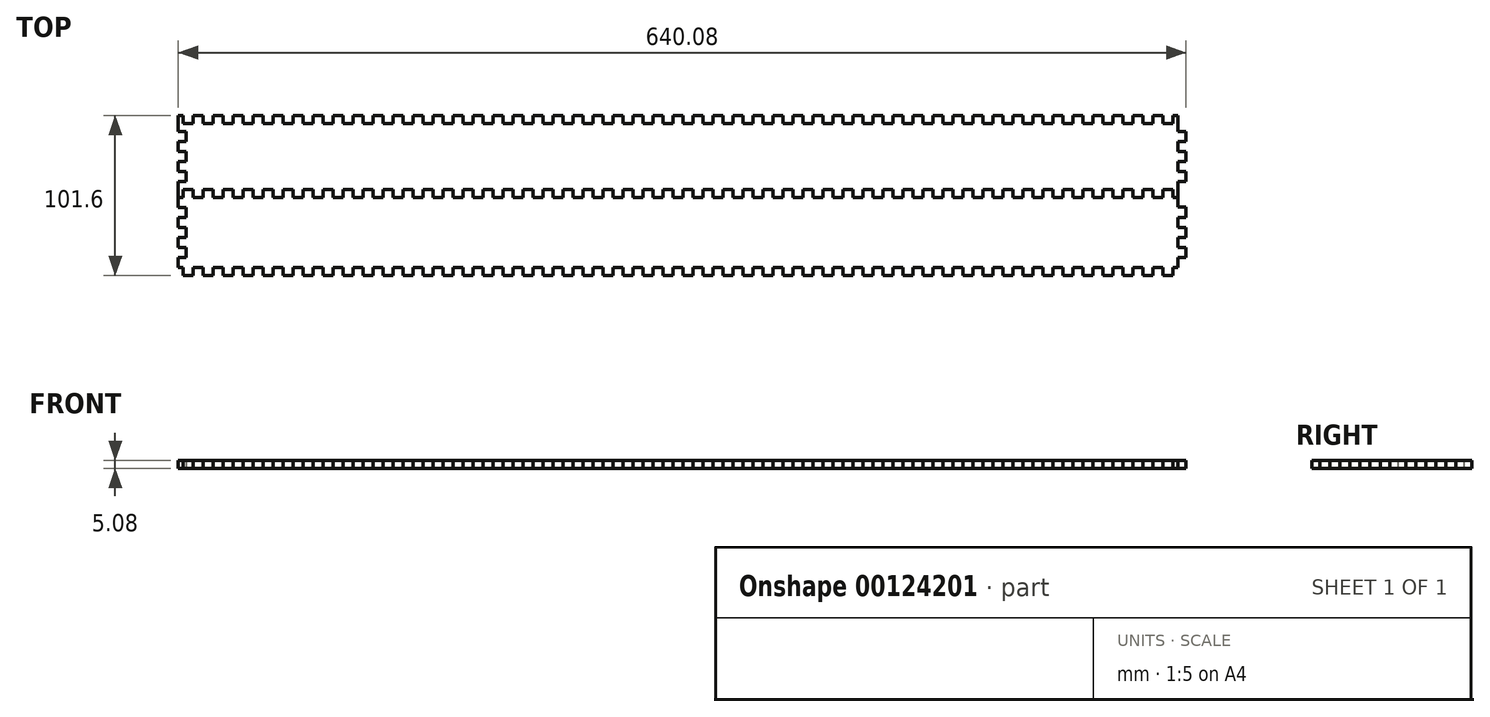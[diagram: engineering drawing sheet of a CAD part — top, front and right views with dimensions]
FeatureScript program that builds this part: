
annotation { "Feature Type Name" : "Feature", "Feature Type Description" : "" }
export const myFeature = defineFeature(function(context is Context, id is Id, definition is map)
    precondition{}
    {
        {
            var Q0;
            Q0=qCreatedBy(makeId("Top.planeOp"),FACE);
            var sketch = newSketch(context, id + "F0", { "sketchPlane" : qUnion([Q0])});
            skLineSegment(sketch, "E0.bottom", {"start": v(-432.26, 259.44) * mm, "end": v(380.54, 259.44) * mm});
            skLineSegment(sketch, "E0.top", {"start": v(-432.26, -197.76) * mm, "end": v(380.54, -197.76) * mm});
            skLineSegment(sketch, "E0.right", {"start": v(380.54, 259.44) * mm, "end": v(380.54, -197.76) * mm});
            skLineSegment(sketch, "E1.bottom", {"start": v(-418.93, 255.63) * mm, "end": v(-412.58, 255.63) * mm});
            skLineSegment(sketch, "E1.left", {"start": v(-418.93, 255.63) * mm, "end": v(-418.93, 250.55) * mm});
            skLineSegment(sketch, "E1.right", {"start": v(-412.58, 255.63) * mm, "end": v(-412.58, 250.55) * mm});
            skLineSegment(sketch, "E2", {"start": v(-412.58, 250.55) * mm, "end": v(-406.23, 250.55) * mm});
            skLineSegment(sketch, "E3.1.0.0", {"start": v(-406.23, 255.63) * mm, "end": v(-406.23, 250.55) * mm});
            skLineSegment(sketch, "E3.1.0.1", {"start": v(-406.23, 255.63) * mm, "end": v(-399.88, 255.63) * mm});
            skLineSegment(sketch, "E3.1.0.2", {"start": v(-399.88, 255.63) * mm, "end": v(-399.88, 250.55) * mm});
            skLineSegment(sketch, "E3.1.0.3", {"start": v(-399.88, 250.55) * mm, "end": v(-393.53, 250.55) * mm});
            skLineSegment(sketch, "E3.2.0.0", {"start": v(-393.53, 255.63) * mm, "end": v(-393.53, 250.55) * mm});
            skLineSegment(sketch, "E3.2.0.1", {"start": v(-393.53, 255.63) * mm, "end": v(-387.18, 255.63) * mm});
            skLineSegment(sketch, "E3.2.0.2", {"start": v(-387.18, 255.63) * mm, "end": v(-387.18, 250.55) * mm});
            skLineSegment(sketch, "E3.2.0.3", {"start": v(-387.18, 250.55) * mm, "end": v(-380.83, 250.55) * mm});
            skLineSegment(sketch, "E3.3.0.0", {"start": v(-380.83, 255.63) * mm, "end": v(-380.83, 250.55) * mm});
            skLineSegment(sketch, "E3.3.0.1", {"start": v(-380.83, 255.63) * mm, "end": v(-374.48, 255.63) * mm});
            skLineSegment(sketch, "E3.3.0.2", {"start": v(-374.48, 255.63) * mm, "end": v(-374.48, 250.55) * mm});
            skLineSegment(sketch, "E3.3.0.3", {"start": v(-374.48, 250.55) * mm, "end": v(-368.13, 250.55) * mm});
            skLineSegment(sketch, "E3.4.0.0", {"start": v(-368.13, 255.63) * mm, "end": v(-368.13, 250.55) * mm});
            skLineSegment(sketch, "E3.4.0.1", {"start": v(-368.13, 255.63) * mm, "end": v(-361.78, 255.63) * mm});
            skLineSegment(sketch, "E3.4.0.2", {"start": v(-361.78, 255.63) * mm, "end": v(-361.78, 250.55) * mm});
            skLineSegment(sketch, "E3.4.0.3", {"start": v(-361.78, 250.55) * mm, "end": v(-355.43, 250.55) * mm});
            skLineSegment(sketch, "E3.5.0.0", {"start": v(-355.43, 255.63) * mm, "end": v(-355.43, 250.55) * mm});
            skLineSegment(sketch, "E3.5.0.1", {"start": v(-355.43, 255.63) * mm, "end": v(-349.08, 255.63) * mm});
            skLineSegment(sketch, "E3.5.0.2", {"start": v(-349.08, 255.63) * mm, "end": v(-349.08, 250.55) * mm});
            skLineSegment(sketch, "E3.5.0.3", {"start": v(-349.08, 250.55) * mm, "end": v(-342.73, 250.55) * mm});
            skLineSegment(sketch, "E3.6.0.0", {"start": v(-342.73, 255.63) * mm, "end": v(-342.73, 250.55) * mm});
            skLineSegment(sketch, "E3.6.0.1", {"start": v(-342.73, 255.63) * mm, "end": v(-336.38, 255.63) * mm});
            skLineSegment(sketch, "E3.6.0.2", {"start": v(-336.38, 255.63) * mm, "end": v(-336.38, 250.55) * mm});
            skLineSegment(sketch, "E3.6.0.3", {"start": v(-336.38, 250.55) * mm, "end": v(-330.03, 250.55) * mm});
            skLineSegment(sketch, "E3.7.0.0", {"start": v(-330.03, 255.63) * mm, "end": v(-330.03, 250.55) * mm});
            skLineSegment(sketch, "E3.7.0.1", {"start": v(-330.03, 255.63) * mm, "end": v(-323.68, 255.63) * mm});
            skLineSegment(sketch, "E3.7.0.2", {"start": v(-323.68, 255.63) * mm, "end": v(-323.68, 250.55) * mm});
            skLineSegment(sketch, "E3.7.0.3", {"start": v(-323.68, 250.55) * mm, "end": v(-317.33, 250.55) * mm});
            skLineSegment(sketch, "E3.8.0.0", {"start": v(-317.33, 255.63) * mm, "end": v(-317.33, 250.55) * mm});
            skLineSegment(sketch, "E3.8.0.1", {"start": v(-317.33, 255.63) * mm, "end": v(-310.98, 255.63) * mm});
            skLineSegment(sketch, "E3.8.0.2", {"start": v(-310.98, 255.63) * mm, "end": v(-310.98, 250.55) * mm});
            skLineSegment(sketch, "E3.8.0.3", {"start": v(-310.98, 250.55) * mm, "end": v(-304.63, 250.55) * mm});
            skLineSegment(sketch, "E3.9.0.0", {"start": v(-304.63, 255.63) * mm, "end": v(-304.63, 250.55) * mm});
            skLineSegment(sketch, "E3.9.0.1", {"start": v(-304.63, 255.63) * mm, "end": v(-298.28, 255.63) * mm});
            skLineSegment(sketch, "E3.9.0.2", {"start": v(-298.28, 255.63) * mm, "end": v(-298.28, 250.55) * mm});
            skLineSegment(sketch, "E3.9.0.3", {"start": v(-298.28, 250.55) * mm, "end": v(-291.93, 250.55) * mm});
            skLineSegment(sketch, "E3.10.0.0", {"start": v(-291.93, 255.63) * mm, "end": v(-291.93, 250.55) * mm});
            skLineSegment(sketch, "E3.10.0.1", {"start": v(-291.93, 255.63) * mm, "end": v(-285.58, 255.63) * mm});
            skLineSegment(sketch, "E3.10.0.2", {"start": v(-285.58, 255.63) * mm, "end": v(-285.58, 250.55) * mm});
            skLineSegment(sketch, "E3.10.0.3", {"start": v(-285.58, 250.55) * mm, "end": v(-279.23, 250.55) * mm});
            skLineSegment(sketch, "E3.11.0.0", {"start": v(-279.23, 255.63) * mm, "end": v(-279.23, 250.55) * mm});
            skLineSegment(sketch, "E3.11.0.1", {"start": v(-279.23, 255.63) * mm, "end": v(-272.88, 255.63) * mm});
            skLineSegment(sketch, "E3.11.0.2", {"start": v(-272.88, 255.63) * mm, "end": v(-272.88, 250.55) * mm});
            skLineSegment(sketch, "E3.11.0.3", {"start": v(-272.88, 250.55) * mm, "end": v(-266.53, 250.55) * mm});
            skLineSegment(sketch, "E3.12.0.0", {"start": v(-266.53, 255.63) * mm, "end": v(-266.53, 250.55) * mm});
            skLineSegment(sketch, "E3.12.0.1", {"start": v(-266.53, 255.63) * mm, "end": v(-260.18, 255.63) * mm});
            skLineSegment(sketch, "E3.12.0.2", {"start": v(-260.18, 255.63) * mm, "end": v(-260.18, 250.55) * mm});
            skLineSegment(sketch, "E3.12.0.3", {"start": v(-260.18, 250.55) * mm, "end": v(-253.83, 250.55) * mm});
            skLineSegment(sketch, "E3.13.0.0", {"start": v(-253.83, 255.63) * mm, "end": v(-253.83, 250.55) * mm});
            skLineSegment(sketch, "E3.13.0.1", {"start": v(-253.83, 255.63) * mm, "end": v(-247.48, 255.63) * mm});
            skLineSegment(sketch, "E3.13.0.2", {"start": v(-247.48, 255.63) * mm, "end": v(-247.48, 250.55) * mm});
            skLineSegment(sketch, "E3.13.0.3", {"start": v(-247.48, 250.55) * mm, "end": v(-241.13, 250.55) * mm});
            skLineSegment(sketch, "E3.14.0.0", {"start": v(-241.13, 255.63) * mm, "end": v(-241.13, 250.55) * mm});
            skLineSegment(sketch, "E3.14.0.1", {"start": v(-241.13, 255.63) * mm, "end": v(-234.78, 255.63) * mm});
            skLineSegment(sketch, "E3.14.0.2", {"start": v(-234.78, 255.63) * mm, "end": v(-234.78, 250.55) * mm});
            skLineSegment(sketch, "E3.14.0.3", {"start": v(-234.78, 250.55) * mm, "end": v(-228.43, 250.55) * mm});
            skLineSegment(sketch, "E3.15.0.0", {"start": v(-228.43, 255.63) * mm, "end": v(-228.43, 250.55) * mm});
            skLineSegment(sketch, "E3.15.0.1", {"start": v(-228.43, 255.63) * mm, "end": v(-222.08, 255.63) * mm});
            skLineSegment(sketch, "E3.15.0.2", {"start": v(-222.08, 255.63) * mm, "end": v(-222.08, 250.55) * mm});
            skLineSegment(sketch, "E3.15.0.3", {"start": v(-222.08, 250.55) * mm, "end": v(-215.73, 250.55) * mm});
            skLineSegment(sketch, "E3.16.0.0", {"start": v(-215.73, 255.63) * mm, "end": v(-215.73, 250.55) * mm});
            skLineSegment(sketch, "E3.16.0.1", {"start": v(-215.73, 255.63) * mm, "end": v(-209.38, 255.63) * mm});
            skLineSegment(sketch, "E3.16.0.2", {"start": v(-209.38, 255.63) * mm, "end": v(-209.38, 250.55) * mm});
            skLineSegment(sketch, "E3.16.0.3", {"start": v(-209.38, 250.55) * mm, "end": v(-203.03, 250.55) * mm});
            skLineSegment(sketch, "E3.17.0.0", {"start": v(-203.03, 255.63) * mm, "end": v(-203.03, 250.55) * mm});
            skLineSegment(sketch, "E3.17.0.1", {"start": v(-203.03, 255.63) * mm, "end": v(-196.68, 255.63) * mm});
            skLineSegment(sketch, "E3.17.0.2", {"start": v(-196.68, 255.63) * mm, "end": v(-196.68, 250.55) * mm});
            skLineSegment(sketch, "E3.17.0.3", {"start": v(-196.68, 250.55) * mm, "end": v(-190.33, 250.55) * mm});
            skLineSegment(sketch, "E3.18.0.0", {"start": v(-190.33, 255.63) * mm, "end": v(-190.33, 250.55) * mm});
            skLineSegment(sketch, "E3.18.0.1", {"start": v(-190.33, 255.63) * mm, "end": v(-183.98, 255.63) * mm});
            skLineSegment(sketch, "E3.18.0.2", {"start": v(-183.98, 255.63) * mm, "end": v(-183.98, 250.55) * mm});
            skLineSegment(sketch, "E3.18.0.3", {"start": v(-183.98, 250.55) * mm, "end": v(-177.63, 250.55) * mm});
            skLineSegment(sketch, "E3.19.0.0", {"start": v(-177.63, 255.63) * mm, "end": v(-177.63, 250.55) * mm});
            skLineSegment(sketch, "E3.19.0.1", {"start": v(-177.63, 255.63) * mm, "end": v(-171.28, 255.63) * mm});
            skLineSegment(sketch, "E3.19.0.2", {"start": v(-171.28, 255.63) * mm, "end": v(-171.28, 250.55) * mm});
            skLineSegment(sketch, "E3.19.0.3", {"start": v(-171.28, 250.55) * mm, "end": v(-164.93, 250.55) * mm});
            skLineSegment(sketch, "E3.20.0.0", {"start": v(-164.93, 255.63) * mm, "end": v(-164.93, 250.55) * mm});
            skLineSegment(sketch, "E3.20.0.1", {"start": v(-164.93, 255.63) * mm, "end": v(-158.58, 255.63) * mm});
            skLineSegment(sketch, "E3.20.0.2", {"start": v(-158.58, 255.63) * mm, "end": v(-158.58, 250.55) * mm});
            skLineSegment(sketch, "E3.20.0.3", {"start": v(-158.58, 250.55) * mm, "end": v(-152.23, 250.55) * mm});
            skLineSegment(sketch, "E3.21.0.0", {"start": v(-152.23, 255.63) * mm, "end": v(-152.23, 250.55) * mm});
            skLineSegment(sketch, "E3.21.0.1", {"start": v(-152.23, 255.63) * mm, "end": v(-145.88, 255.63) * mm});
            skLineSegment(sketch, "E3.21.0.2", {"start": v(-145.88, 255.63) * mm, "end": v(-145.88, 250.55) * mm});
            skLineSegment(sketch, "E3.21.0.3", {"start": v(-145.88, 250.55) * mm, "end": v(-139.53, 250.55) * mm});
            skLineSegment(sketch, "E3.22.0.0", {"start": v(-139.53, 255.63) * mm, "end": v(-139.53, 250.55) * mm});
            skLineSegment(sketch, "E3.22.0.1", {"start": v(-139.53, 255.63) * mm, "end": v(-133.18, 255.63) * mm});
            skLineSegment(sketch, "E3.22.0.2", {"start": v(-133.18, 255.63) * mm, "end": v(-133.18, 250.55) * mm});
            skLineSegment(sketch, "E3.22.0.3", {"start": v(-133.18, 250.55) * mm, "end": v(-126.83, 250.55) * mm});
            skLineSegment(sketch, "E3.23.0.0", {"start": v(-126.83, 255.63) * mm, "end": v(-126.83, 250.55) * mm});
            skLineSegment(sketch, "E3.23.0.1", {"start": v(-126.83, 255.63) * mm, "end": v(-120.48, 255.63) * mm});
            skLineSegment(sketch, "E3.23.0.2", {"start": v(-120.48, 255.63) * mm, "end": v(-120.48, 250.55) * mm});
            skLineSegment(sketch, "E3.23.0.3", {"start": v(-120.48, 250.55) * mm, "end": v(-114.13, 250.55) * mm});
            skLineSegment(sketch, "E3.24.0.0", {"start": v(-114.13, 255.63) * mm, "end": v(-114.13, 250.55) * mm});
            skLineSegment(sketch, "E3.24.0.1", {"start": v(-114.13, 255.63) * mm, "end": v(-107.78, 255.63) * mm});
            skLineSegment(sketch, "E3.24.0.2", {"start": v(-107.78, 255.63) * mm, "end": v(-107.78, 250.55) * mm});
            skLineSegment(sketch, "E3.24.0.3", {"start": v(-107.78, 250.55) * mm, "end": v(-101.43, 250.55) * mm});
            skLineSegment(sketch, "E3.25.0.0", {"start": v(-101.43, 255.63) * mm, "end": v(-101.43, 250.55) * mm});
            skLineSegment(sketch, "E3.25.0.1", {"start": v(-101.43, 255.63) * mm, "end": v(-95.08, 255.63) * mm});
            skLineSegment(sketch, "E3.25.0.2", {"start": v(-95.08, 255.63) * mm, "end": v(-95.08, 250.55) * mm});
            skLineSegment(sketch, "E3.25.0.3", {"start": v(-95.08, 250.55) * mm, "end": v(-88.73, 250.55) * mm});
            skLineSegment(sketch, "E3.26.0.0", {"start": v(-88.73, 255.63) * mm, "end": v(-88.73, 250.55) * mm});
            skLineSegment(sketch, "E3.26.0.1", {"start": v(-88.73, 255.63) * mm, "end": v(-82.38, 255.63) * mm});
            skLineSegment(sketch, "E3.26.0.2", {"start": v(-82.38, 255.63) * mm, "end": v(-82.38, 250.55) * mm});
            skLineSegment(sketch, "E3.26.0.3", {"start": v(-82.38, 250.55) * mm, "end": v(-76.03, 250.55) * mm});
            skLineSegment(sketch, "E3.27.0.0", {"start": v(-76.03, 255.63) * mm, "end": v(-76.03, 250.55) * mm});
            skLineSegment(sketch, "E3.27.0.1", {"start": v(-76.03, 255.63) * mm, "end": v(-69.68, 255.63) * mm});
            skLineSegment(sketch, "E3.27.0.2", {"start": v(-69.68, 255.63) * mm, "end": v(-69.68, 250.55) * mm});
            skLineSegment(sketch, "E3.27.0.3", {"start": v(-69.68, 250.55) * mm, "end": v(-63.33, 250.55) * mm});
            skLineSegment(sketch, "E3.28.0.0", {"start": v(-63.33, 255.63) * mm, "end": v(-63.33, 250.55) * mm});
            skLineSegment(sketch, "E3.28.0.1", {"start": v(-63.33, 255.63) * mm, "end": v(-56.98, 255.63) * mm});
            skLineSegment(sketch, "E3.28.0.2", {"start": v(-56.98, 255.63) * mm, "end": v(-56.98, 250.55) * mm});
            skLineSegment(sketch, "E3.28.0.3", {"start": v(-56.98, 250.55) * mm, "end": v(-50.63, 250.55) * mm});
            skLineSegment(sketch, "E3.29.0.0", {"start": v(-50.63, 255.63) * mm, "end": v(-50.63, 250.55) * mm});
            skLineSegment(sketch, "E3.29.0.1", {"start": v(-50.63, 255.63) * mm, "end": v(-44.28, 255.63) * mm});
            skLineSegment(sketch, "E3.29.0.2", {"start": v(-44.28, 255.63) * mm, "end": v(-44.28, 250.55) * mm});
            skLineSegment(sketch, "E3.29.0.3", {"start": v(-44.28, 250.55) * mm, "end": v(-37.93, 250.55) * mm});
            skLineSegment(sketch, "E3.30.0.0", {"start": v(-37.93, 255.63) * mm, "end": v(-37.93, 250.55) * mm});
            skLineSegment(sketch, "E3.30.0.1", {"start": v(-37.93, 255.63) * mm, "end": v(-31.58, 255.63) * mm});
            skLineSegment(sketch, "E3.30.0.2", {"start": v(-31.58, 255.63) * mm, "end": v(-31.58, 250.55) * mm});
            skLineSegment(sketch, "E3.30.0.3", {"start": v(-31.58, 250.55) * mm, "end": v(-25.23, 250.55) * mm});
            skLineSegment(sketch, "E3.31.0.0", {"start": v(-25.23, 255.63) * mm, "end": v(-25.23, 250.55) * mm});
            skLineSegment(sketch, "E3.31.0.1", {"start": v(-25.23, 255.63) * mm, "end": v(-18.88, 255.63) * mm});
            skLineSegment(sketch, "E3.31.0.2", {"start": v(-18.88, 255.63) * mm, "end": v(-18.88, 250.55) * mm});
            skLineSegment(sketch, "E3.31.0.3", {"start": v(-18.88, 250.55) * mm, "end": v(-12.53, 250.55) * mm});
            skLineSegment(sketch, "E3.32.0.0", {"start": v(-12.53, 255.63) * mm, "end": v(-12.53, 250.55) * mm});
            skLineSegment(sketch, "E3.32.0.1", {"start": v(-12.53, 255.63) * mm, "end": v(-6.18, 255.63) * mm});
            skLineSegment(sketch, "E3.32.0.2", {"start": v(-6.18, 255.63) * mm, "end": v(-6.18, 250.55) * mm});
            skLineSegment(sketch, "E3.32.0.3", {"start": v(-6.18, 250.55) * mm, "end": v(0.17, 250.55) * mm});
            skLineSegment(sketch, "E3.33.0.0", {"start": v(0.17, 255.63) * mm, "end": v(0.17, 250.55) * mm});
            skLineSegment(sketch, "E3.33.0.1", {"start": v(0.17, 255.63) * mm, "end": v(6.52, 255.63) * mm});
            skLineSegment(sketch, "E3.33.0.2", {"start": v(6.52, 255.63) * mm, "end": v(6.52, 250.55) * mm});
            skLineSegment(sketch, "E3.33.0.3", {"start": v(6.52, 250.55) * mm, "end": v(12.87, 250.55) * mm});
            skLineSegment(sketch, "E3.34.0.0", {"start": v(12.87, 255.63) * mm, "end": v(12.87, 250.55) * mm});
            skLineSegment(sketch, "E3.34.0.1", {"start": v(12.87, 255.63) * mm, "end": v(19.22, 255.63) * mm});
            skLineSegment(sketch, "E3.34.0.2", {"start": v(19.22, 255.63) * mm, "end": v(19.22, 250.55) * mm});
            skLineSegment(sketch, "E3.34.0.3", {"start": v(19.22, 250.55) * mm, "end": v(25.57, 250.55) * mm});
            skLineSegment(sketch, "E3.35.0.0", {"start": v(25.57, 255.63) * mm, "end": v(25.57, 250.55) * mm});
            skLineSegment(sketch, "E3.35.0.1", {"start": v(25.57, 255.63) * mm, "end": v(31.92, 255.63) * mm});
            skLineSegment(sketch, "E3.35.0.2", {"start": v(31.92, 255.63) * mm, "end": v(31.92, 250.55) * mm});
            skLineSegment(sketch, "E3.35.0.3", {"start": v(31.92, 250.55) * mm, "end": v(38.27, 250.55) * mm});
            skLineSegment(sketch, "E3.36.0.0", {"start": v(38.27, 255.63) * mm, "end": v(38.27, 250.55) * mm});
            skLineSegment(sketch, "E3.36.0.1", {"start": v(38.27, 255.63) * mm, "end": v(44.62, 255.63) * mm});
            skLineSegment(sketch, "E3.36.0.2", {"start": v(44.62, 255.63) * mm, "end": v(44.62, 250.55) * mm});
            skLineSegment(sketch, "E3.36.0.3", {"start": v(44.62, 250.55) * mm, "end": v(50.97, 250.55) * mm});
            skLineSegment(sketch, "E3.37.0.0", {"start": v(50.97, 255.63) * mm, "end": v(50.97, 250.55) * mm});
            skLineSegment(sketch, "E3.37.0.1", {"start": v(50.97, 255.63) * mm, "end": v(57.32, 255.63) * mm});
            skLineSegment(sketch, "E3.37.0.2", {"start": v(57.32, 255.63) * mm, "end": v(57.32, 250.55) * mm});
            skLineSegment(sketch, "E3.37.0.3", {"start": v(57.32, 250.55) * mm, "end": v(63.67, 250.55) * mm});
            skLineSegment(sketch, "E3.38.0.0", {"start": v(63.67, 255.63) * mm, "end": v(63.67, 250.55) * mm});
            skLineSegment(sketch, "E3.38.0.1", {"start": v(63.67, 255.63) * mm, "end": v(70.02, 255.63) * mm});
            skLineSegment(sketch, "E3.38.0.2", {"start": v(70.02, 255.63) * mm, "end": v(70.02, 250.55) * mm});
            skLineSegment(sketch, "E3.38.0.3", {"start": v(70.02, 250.55) * mm, "end": v(76.37, 250.55) * mm});
            skLineSegment(sketch, "E3.39.0.0", {"start": v(76.37, 255.63) * mm, "end": v(76.37, 250.55) * mm});
            skLineSegment(sketch, "E3.39.0.1", {"start": v(76.37, 255.63) * mm, "end": v(82.72, 255.63) * mm});
            skLineSegment(sketch, "E3.39.0.2", {"start": v(82.72, 255.63) * mm, "end": v(82.72, 250.55) * mm});
            skLineSegment(sketch, "E3.39.0.3", {"start": v(82.72, 250.55) * mm, "end": v(89.07, 250.55) * mm});
            skLineSegment(sketch, "E3.40.0.0", {"start": v(89.07, 255.63) * mm, "end": v(89.07, 250.55) * mm});
            skLineSegment(sketch, "E3.40.0.1", {"start": v(89.07, 255.63) * mm, "end": v(95.42, 255.63) * mm});
            skLineSegment(sketch, "E3.40.0.2", {"start": v(95.42, 255.63) * mm, "end": v(95.42, 250.55) * mm});
            skLineSegment(sketch, "E3.40.0.3", {"start": v(95.42, 250.55) * mm, "end": v(101.77, 250.55) * mm});
            skLineSegment(sketch, "E3.41.0.0", {"start": v(101.77, 255.63) * mm, "end": v(101.77, 250.55) * mm});
            skLineSegment(sketch, "E3.41.0.1", {"start": v(101.77, 255.63) * mm, "end": v(108.12, 255.63) * mm});
            skLineSegment(sketch, "E3.41.0.2", {"start": v(108.12, 255.63) * mm, "end": v(108.12, 250.55) * mm});
            skLineSegment(sketch, "E3.41.0.3", {"start": v(108.12, 250.55) * mm, "end": v(114.47, 250.55) * mm});
            skLineSegment(sketch, "E3.42.0.0", {"start": v(114.47, 255.63) * mm, "end": v(114.47, 250.55) * mm});
            skLineSegment(sketch, "E3.42.0.1", {"start": v(114.47, 255.63) * mm, "end": v(120.82, 255.63) * mm});
            skLineSegment(sketch, "E3.42.0.2", {"start": v(120.82, 255.63) * mm, "end": v(120.82, 250.55) * mm});
            skLineSegment(sketch, "E3.42.0.3", {"start": v(120.82, 250.55) * mm, "end": v(127.17, 250.55) * mm});
            skLineSegment(sketch, "E3.43.0.0", {"start": v(127.17, 255.63) * mm, "end": v(127.17, 250.55) * mm});
            skLineSegment(sketch, "E3.43.0.1", {"start": v(127.17, 255.63) * mm, "end": v(133.52, 255.63) * mm});
            skLineSegment(sketch, "E3.43.0.2", {"start": v(133.52, 255.63) * mm, "end": v(133.52, 250.55) * mm});
            skLineSegment(sketch, "E3.43.0.3", {"start": v(133.52, 250.55) * mm, "end": v(139.87, 250.55) * mm});
            skLineSegment(sketch, "E3.44.0.0", {"start": v(139.87, 255.63) * mm, "end": v(139.87, 250.55) * mm});
            skLineSegment(sketch, "E3.44.0.1", {"start": v(139.87, 255.63) * mm, "end": v(146.22, 255.63) * mm});
            skLineSegment(sketch, "E3.44.0.2", {"start": v(146.22, 255.63) * mm, "end": v(146.22, 250.55) * mm});
            skLineSegment(sketch, "E3.44.0.3", {"start": v(146.22, 250.55) * mm, "end": v(152.57, 250.55) * mm});
            skLineSegment(sketch, "E3.45.0.0", {"start": v(152.57, 255.63) * mm, "end": v(152.57, 250.55) * mm});
            skLineSegment(sketch, "E3.45.0.1", {"start": v(152.57, 255.63) * mm, "end": v(158.92, 255.63) * mm});
            skLineSegment(sketch, "E3.45.0.2", {"start": v(158.92, 255.63) * mm, "end": v(158.92, 250.55) * mm});
            skLineSegment(sketch, "E3.45.0.3", {"start": v(158.92, 250.55) * mm, "end": v(165.27, 250.55) * mm});
            skLineSegment(sketch, "E3.46.0.0", {"start": v(165.27, 255.63) * mm, "end": v(165.27, 250.55) * mm});
            skLineSegment(sketch, "E3.46.0.1", {"start": v(165.27, 255.63) * mm, "end": v(171.62, 255.63) * mm});
            skLineSegment(sketch, "E3.46.0.2", {"start": v(171.62, 255.63) * mm, "end": v(171.62, 250.55) * mm});
            skLineSegment(sketch, "E3.46.0.3", {"start": v(171.62, 250.55) * mm, "end": v(177.97, 250.55) * mm});
            skLineSegment(sketch, "E3.47.0.0", {"start": v(177.97, 255.63) * mm, "end": v(177.97, 250.55) * mm});
            skLineSegment(sketch, "E3.47.0.1", {"start": v(177.97, 255.63) * mm, "end": v(184.32, 255.63) * mm});
            skLineSegment(sketch, "E3.47.0.2", {"start": v(184.32, 255.63) * mm, "end": v(184.32, 250.55) * mm});
            skLineSegment(sketch, "E3.47.0.3", {"start": v(184.32, 250.55) * mm, "end": v(190.67, 250.55) * mm});
            skLineSegment(sketch, "E3.48.0.0", {"start": v(190.67, 255.63) * mm, "end": v(190.67, 250.55) * mm});
            skLineSegment(sketch, "E3.48.0.1", {"start": v(190.67, 255.63) * mm, "end": v(197.02, 255.63) * mm});
            skLineSegment(sketch, "E3.48.0.2", {"start": v(197.02, 255.63) * mm, "end": v(197.02, 250.55) * mm});
            skLineSegment(sketch, "E3.48.0.3", {"start": v(197.02, 250.55) * mm, "end": v(203.37, 250.55) * mm});
            skLineSegment(sketch, "E3.49.0.0", {"start": v(203.37, 255.63) * mm, "end": v(203.37, 250.55) * mm});
            skLineSegment(sketch, "E3.direction1", {"start": v(-418.93, 250.55) * mm, "end": v(-406.23, 250.55) * mm, "construction": true});
            skLineSegment(sketch, "E4.bottom", {"start": v(-418.93, 203.56) * mm, "end": v(-412.58, 203.56) * mm});
            skLineSegment(sketch, "E4.left", {"start": v(-418.93, 208.64) * mm, "end": v(-418.93, 203.56) * mm});
            skLineSegment(sketch, "E4.right", {"start": v(-412.58, 208.64) * mm, "end": v(-412.58, 203.56) * mm});
            skLineSegment(sketch, "E5", {"start": v(-412.58, 208.64) * mm, "end": v(-406.23, 208.64) * mm});
            skLineSegment(sketch, "E6.1.0.0", {"start": v(-406.23, 208.64) * mm, "end": v(-406.23, 203.56) * mm});
            skLineSegment(sketch, "E6.1.0.1", {"start": v(-406.23, 203.56) * mm, "end": v(-399.88, 203.56) * mm});
            skLineSegment(sketch, "E6.1.0.2", {"start": v(-399.88, 208.64) * mm, "end": v(-399.88, 203.56) * mm});
            skLineSegment(sketch, "E6.1.0.3", {"start": v(-399.88, 208.64) * mm, "end": v(-393.53, 208.64) * mm});
            skLineSegment(sketch, "E6.2.0.0", {"start": v(-393.53, 208.64) * mm, "end": v(-393.53, 203.56) * mm});
            skLineSegment(sketch, "E6.2.0.1", {"start": v(-393.53, 203.56) * mm, "end": v(-387.18, 203.56) * mm});
            skLineSegment(sketch, "E6.2.0.2", {"start": v(-387.18, 208.64) * mm, "end": v(-387.18, 203.56) * mm});
            skLineSegment(sketch, "E6.2.0.3", {"start": v(-387.18, 208.64) * mm, "end": v(-380.83, 208.64) * mm});
            skLineSegment(sketch, "E6.3.0.0", {"start": v(-380.83, 208.64) * mm, "end": v(-380.83, 203.56) * mm});
            skLineSegment(sketch, "E6.3.0.1", {"start": v(-380.83, 203.56) * mm, "end": v(-374.48, 203.56) * mm});
            skLineSegment(sketch, "E6.3.0.2", {"start": v(-374.48, 208.64) * mm, "end": v(-374.48, 203.56) * mm});
            skLineSegment(sketch, "E6.3.0.3", {"start": v(-374.48, 208.64) * mm, "end": v(-368.13, 208.64) * mm});
            skLineSegment(sketch, "E6.4.0.0", {"start": v(-368.13, 208.64) * mm, "end": v(-368.13, 203.56) * mm});
            skLineSegment(sketch, "E6.4.0.1", {"start": v(-368.13, 203.56) * mm, "end": v(-361.78, 203.56) * mm});
            skLineSegment(sketch, "E6.4.0.2", {"start": v(-361.78, 208.64) * mm, "end": v(-361.78, 203.56) * mm});
            skLineSegment(sketch, "E6.4.0.3", {"start": v(-361.78, 208.64) * mm, "end": v(-355.43, 208.64) * mm});
            skLineSegment(sketch, "E6.5.0.0", {"start": v(-355.43, 208.64) * mm, "end": v(-355.43, 203.56) * mm});
            skLineSegment(sketch, "E6.5.0.1", {"start": v(-355.43, 203.56) * mm, "end": v(-349.08, 203.56) * mm});
            skLineSegment(sketch, "E6.5.0.2", {"start": v(-349.08, 208.64) * mm, "end": v(-349.08, 203.56) * mm});
            skLineSegment(sketch, "E6.5.0.3", {"start": v(-349.08, 208.64) * mm, "end": v(-342.73, 208.64) * mm});
            skLineSegment(sketch, "E6.6.0.0", {"start": v(-342.73, 208.64) * mm, "end": v(-342.73, 203.56) * mm});
            skLineSegment(sketch, "E6.6.0.1", {"start": v(-342.73, 203.56) * mm, "end": v(-336.38, 203.56) * mm});
            skLineSegment(sketch, "E6.6.0.2", {"start": v(-336.38, 208.64) * mm, "end": v(-336.38, 203.56) * mm});
            skLineSegment(sketch, "E6.6.0.3", {"start": v(-336.38, 208.64) * mm, "end": v(-330.03, 208.64) * mm});
            skLineSegment(sketch, "E6.7.0.0", {"start": v(-330.03, 208.64) * mm, "end": v(-330.03, 203.56) * mm});
            skLineSegment(sketch, "E6.7.0.1", {"start": v(-330.03, 203.56) * mm, "end": v(-323.68, 203.56) * mm});
            skLineSegment(sketch, "E6.7.0.2", {"start": v(-323.68, 208.64) * mm, "end": v(-323.68, 203.56) * mm});
            skLineSegment(sketch, "E6.7.0.3", {"start": v(-323.68, 208.64) * mm, "end": v(-317.33, 208.64) * mm});
            skLineSegment(sketch, "E6.8.0.0", {"start": v(-317.33, 208.64) * mm, "end": v(-317.33, 203.56) * mm});
            skLineSegment(sketch, "E6.8.0.1", {"start": v(-317.33, 203.56) * mm, "end": v(-310.98, 203.56) * mm});
            skLineSegment(sketch, "E6.8.0.2", {"start": v(-310.98, 208.64) * mm, "end": v(-310.98, 203.56) * mm});
            skLineSegment(sketch, "E6.8.0.3", {"start": v(-310.98, 208.64) * mm, "end": v(-304.63, 208.64) * mm});
            skLineSegment(sketch, "E6.9.0.0", {"start": v(-304.63, 208.64) * mm, "end": v(-304.63, 203.56) * mm});
            skLineSegment(sketch, "E6.9.0.1", {"start": v(-304.63, 203.56) * mm, "end": v(-298.28, 203.56) * mm});
            skLineSegment(sketch, "E6.9.0.2", {"start": v(-298.28, 208.64) * mm, "end": v(-298.28, 203.56) * mm});
            skLineSegment(sketch, "E6.9.0.3", {"start": v(-298.28, 208.64) * mm, "end": v(-291.93, 208.64) * mm});
            skLineSegment(sketch, "E6.10.0.0", {"start": v(-291.93, 208.64) * mm, "end": v(-291.93, 203.56) * mm});
            skLineSegment(sketch, "E6.10.0.1", {"start": v(-291.93, 203.56) * mm, "end": v(-285.58, 203.56) * mm});
            skLineSegment(sketch, "E6.10.0.2", {"start": v(-285.58, 208.64) * mm, "end": v(-285.58, 203.56) * mm});
            skLineSegment(sketch, "E6.10.0.3", {"start": v(-285.58, 208.64) * mm, "end": v(-279.23, 208.64) * mm});
            skLineSegment(sketch, "E6.11.0.0", {"start": v(-279.23, 208.64) * mm, "end": v(-279.23, 203.56) * mm});
            skLineSegment(sketch, "E6.11.0.1", {"start": v(-279.23, 203.56) * mm, "end": v(-272.88, 203.56) * mm});
            skLineSegment(sketch, "E6.11.0.2", {"start": v(-272.88, 208.64) * mm, "end": v(-272.88, 203.56) * mm});
            skLineSegment(sketch, "E6.11.0.3", {"start": v(-272.88, 208.64) * mm, "end": v(-266.53, 208.64) * mm});
            skLineSegment(sketch, "E6.12.0.0", {"start": v(-266.53, 208.64) * mm, "end": v(-266.53, 203.56) * mm});
            skLineSegment(sketch, "E6.12.0.1", {"start": v(-266.53, 203.56) * mm, "end": v(-260.18, 203.56) * mm});
            skLineSegment(sketch, "E6.12.0.2", {"start": v(-260.18, 208.64) * mm, "end": v(-260.18, 203.56) * mm});
            skLineSegment(sketch, "E6.12.0.3", {"start": v(-260.18, 208.64) * mm, "end": v(-253.83, 208.64) * mm});
            skLineSegment(sketch, "E6.13.0.0", {"start": v(-253.83, 208.64) * mm, "end": v(-253.83, 203.56) * mm});
            skLineSegment(sketch, "E6.13.0.1", {"start": v(-253.83, 203.56) * mm, "end": v(-247.48, 203.56) * mm});
            skLineSegment(sketch, "E6.13.0.2", {"start": v(-247.48, 208.64) * mm, "end": v(-247.48, 203.56) * mm});
            skLineSegment(sketch, "E6.13.0.3", {"start": v(-247.48, 208.64) * mm, "end": v(-241.13, 208.64) * mm});
            skLineSegment(sketch, "E6.14.0.0", {"start": v(-241.13, 208.64) * mm, "end": v(-241.13, 203.56) * mm});
            skLineSegment(sketch, "E6.14.0.1", {"start": v(-241.13, 203.56) * mm, "end": v(-234.78, 203.56) * mm});
            skLineSegment(sketch, "E6.14.0.2", {"start": v(-234.78, 208.64) * mm, "end": v(-234.78, 203.56) * mm});
            skLineSegment(sketch, "E6.14.0.3", {"start": v(-234.78, 208.64) * mm, "end": v(-228.43, 208.64) * mm});
            skLineSegment(sketch, "E6.15.0.0", {"start": v(-228.43, 208.64) * mm, "end": v(-228.43, 203.56) * mm});
            skLineSegment(sketch, "E6.15.0.1", {"start": v(-228.43, 203.56) * mm, "end": v(-222.08, 203.56) * mm});
            skLineSegment(sketch, "E6.15.0.2", {"start": v(-222.08, 208.64) * mm, "end": v(-222.08, 203.56) * mm});
            skLineSegment(sketch, "E6.15.0.3", {"start": v(-222.08, 208.64) * mm, "end": v(-215.73, 208.64) * mm});
            skLineSegment(sketch, "E6.16.0.0", {"start": v(-215.73, 208.64) * mm, "end": v(-215.73, 203.56) * mm});
            skLineSegment(sketch, "E6.16.0.1", {"start": v(-215.73, 203.56) * mm, "end": v(-209.38, 203.56) * mm});
            skLineSegment(sketch, "E6.16.0.2", {"start": v(-209.38, 208.64) * mm, "end": v(-209.38, 203.56) * mm});
            skLineSegment(sketch, "E6.16.0.3", {"start": v(-209.38, 208.64) * mm, "end": v(-203.03, 208.64) * mm});
            skLineSegment(sketch, "E6.17.0.0", {"start": v(-203.03, 208.64) * mm, "end": v(-203.03, 203.56) * mm});
            skLineSegment(sketch, "E6.17.0.1", {"start": v(-203.03, 203.56) * mm, "end": v(-196.68, 203.56) * mm});
            skLineSegment(sketch, "E6.17.0.2", {"start": v(-196.68, 208.64) * mm, "end": v(-196.68, 203.56) * mm});
            skLineSegment(sketch, "E6.17.0.3", {"start": v(-196.68, 208.64) * mm, "end": v(-190.33, 208.64) * mm});
            skLineSegment(sketch, "E6.18.0.0", {"start": v(-190.33, 208.64) * mm, "end": v(-190.33, 203.56) * mm});
            skLineSegment(sketch, "E6.18.0.1", {"start": v(-190.33, 203.56) * mm, "end": v(-183.98, 203.56) * mm});
            skLineSegment(sketch, "E6.18.0.2", {"start": v(-183.98, 208.64) * mm, "end": v(-183.98, 203.56) * mm});
            skLineSegment(sketch, "E6.18.0.3", {"start": v(-183.98, 208.64) * mm, "end": v(-177.63, 208.64) * mm});
            skLineSegment(sketch, "E6.19.0.0", {"start": v(-177.63, 208.64) * mm, "end": v(-177.63, 203.56) * mm});
            skLineSegment(sketch, "E6.19.0.1", {"start": v(-177.63, 203.56) * mm, "end": v(-171.28, 203.56) * mm});
            skLineSegment(sketch, "E6.19.0.2", {"start": v(-171.28, 208.64) * mm, "end": v(-171.28, 203.56) * mm});
            skLineSegment(sketch, "E6.19.0.3", {"start": v(-171.28, 208.64) * mm, "end": v(-164.93, 208.64) * mm});
            skLineSegment(sketch, "E6.20.0.0", {"start": v(-164.93, 208.64) * mm, "end": v(-164.93, 203.56) * mm});
            skLineSegment(sketch, "E6.20.0.1", {"start": v(-164.93, 203.56) * mm, "end": v(-158.58, 203.56) * mm});
            skLineSegment(sketch, "E6.20.0.2", {"start": v(-158.58, 208.64) * mm, "end": v(-158.58, 203.56) * mm});
            skLineSegment(sketch, "E6.20.0.3", {"start": v(-158.58, 208.64) * mm, "end": v(-152.23, 208.64) * mm});
            skLineSegment(sketch, "E6.21.0.0", {"start": v(-152.23, 208.64) * mm, "end": v(-152.23, 203.56) * mm});
            skLineSegment(sketch, "E6.21.0.1", {"start": v(-152.23, 203.56) * mm, "end": v(-145.88, 203.56) * mm});
            skLineSegment(sketch, "E6.21.0.2", {"start": v(-145.88, 208.64) * mm, "end": v(-145.88, 203.56) * mm});
            skLineSegment(sketch, "E6.21.0.3", {"start": v(-145.88, 208.64) * mm, "end": v(-139.53, 208.64) * mm});
            skLineSegment(sketch, "E6.22.0.0", {"start": v(-139.53, 208.64) * mm, "end": v(-139.53, 203.56) * mm});
            skLineSegment(sketch, "E6.22.0.1", {"start": v(-139.53, 203.56) * mm, "end": v(-133.18, 203.56) * mm});
            skLineSegment(sketch, "E6.22.0.2", {"start": v(-133.18, 208.64) * mm, "end": v(-133.18, 203.56) * mm});
            skLineSegment(sketch, "E6.22.0.3", {"start": v(-133.18, 208.64) * mm, "end": v(-126.83, 208.64) * mm});
            skLineSegment(sketch, "E6.23.0.0", {"start": v(-126.83, 208.64) * mm, "end": v(-126.83, 203.56) * mm});
            skLineSegment(sketch, "E6.23.0.1", {"start": v(-126.83, 203.56) * mm, "end": v(-120.48, 203.56) * mm});
            skLineSegment(sketch, "E6.23.0.2", {"start": v(-120.48, 208.64) * mm, "end": v(-120.48, 203.56) * mm});
            skLineSegment(sketch, "E6.23.0.3", {"start": v(-120.48, 208.64) * mm, "end": v(-114.13, 208.64) * mm});
            skLineSegment(sketch, "E6.24.0.0", {"start": v(-114.13, 208.64) * mm, "end": v(-114.13, 203.56) * mm});
            skLineSegment(sketch, "E6.24.0.1", {"start": v(-114.13, 203.56) * mm, "end": v(-107.78, 203.56) * mm});
            skLineSegment(sketch, "E6.24.0.2", {"start": v(-107.78, 208.64) * mm, "end": v(-107.78, 203.56) * mm});
            skLineSegment(sketch, "E6.24.0.3", {"start": v(-107.78, 208.64) * mm, "end": v(-101.43, 208.64) * mm});
            skLineSegment(sketch, "E6.25.0.0", {"start": v(-101.43, 208.64) * mm, "end": v(-101.43, 203.56) * mm});
            skLineSegment(sketch, "E6.25.0.1", {"start": v(-101.43, 203.56) * mm, "end": v(-95.08, 203.56) * mm});
            skLineSegment(sketch, "E6.25.0.2", {"start": v(-95.08, 208.64) * mm, "end": v(-95.08, 203.56) * mm});
            skLineSegment(sketch, "E6.25.0.3", {"start": v(-95.08, 208.64) * mm, "end": v(-88.73, 208.64) * mm});
            skLineSegment(sketch, "E6.26.0.0", {"start": v(-88.73, 208.64) * mm, "end": v(-88.73, 203.56) * mm});
            skLineSegment(sketch, "E6.26.0.1", {"start": v(-88.73, 203.56) * mm, "end": v(-82.38, 203.56) * mm});
            skLineSegment(sketch, "E6.26.0.2", {"start": v(-82.38, 208.64) * mm, "end": v(-82.38, 203.56) * mm});
            skLineSegment(sketch, "E6.26.0.3", {"start": v(-82.38, 208.64) * mm, "end": v(-76.03, 208.64) * mm});
            skLineSegment(sketch, "E6.27.0.0", {"start": v(-76.03, 208.64) * mm, "end": v(-76.03, 203.56) * mm});
            skLineSegment(sketch, "E6.27.0.1", {"start": v(-76.03, 203.56) * mm, "end": v(-69.68, 203.56) * mm});
            skLineSegment(sketch, "E6.27.0.2", {"start": v(-69.68, 208.64) * mm, "end": v(-69.68, 203.56) * mm});
            skLineSegment(sketch, "E6.27.0.3", {"start": v(-69.68, 208.64) * mm, "end": v(-63.33, 208.64) * mm});
            skLineSegment(sketch, "E6.28.0.0", {"start": v(-63.33, 208.64) * mm, "end": v(-63.33, 203.56) * mm});
            skLineSegment(sketch, "E6.28.0.1", {"start": v(-63.33, 203.56) * mm, "end": v(-56.98, 203.56) * mm});
            skLineSegment(sketch, "E6.28.0.2", {"start": v(-56.98, 208.64) * mm, "end": v(-56.98, 203.56) * mm});
            skLineSegment(sketch, "E6.28.0.3", {"start": v(-56.98, 208.64) * mm, "end": v(-50.63, 208.64) * mm});
            skLineSegment(sketch, "E6.29.0.0", {"start": v(-50.63, 208.64) * mm, "end": v(-50.63, 203.56) * mm});
            skLineSegment(sketch, "E6.29.0.1", {"start": v(-50.63, 203.56) * mm, "end": v(-44.28, 203.56) * mm});
            skLineSegment(sketch, "E6.29.0.2", {"start": v(-44.28, 208.64) * mm, "end": v(-44.28, 203.56) * mm});
            skLineSegment(sketch, "E6.29.0.3", {"start": v(-44.28, 208.64) * mm, "end": v(-37.93, 208.64) * mm});
            skLineSegment(sketch, "E6.30.0.0", {"start": v(-37.93, 208.64) * mm, "end": v(-37.93, 203.56) * mm});
            skLineSegment(sketch, "E6.30.0.1", {"start": v(-37.93, 203.56) * mm, "end": v(-31.58, 203.56) * mm});
            skLineSegment(sketch, "E6.30.0.2", {"start": v(-31.58, 208.64) * mm, "end": v(-31.58, 203.56) * mm});
            skLineSegment(sketch, "E6.30.0.3", {"start": v(-31.58, 208.64) * mm, "end": v(-25.23, 208.64) * mm});
            skLineSegment(sketch, "E6.31.0.0", {"start": v(-25.23, 208.64) * mm, "end": v(-25.23, 203.56) * mm});
            skLineSegment(sketch, "E6.31.0.1", {"start": v(-25.23, 203.56) * mm, "end": v(-18.88, 203.56) * mm});
            skLineSegment(sketch, "E6.31.0.2", {"start": v(-18.88, 208.64) * mm, "end": v(-18.88, 203.56) * mm});
            skLineSegment(sketch, "E6.31.0.3", {"start": v(-18.88, 208.64) * mm, "end": v(-12.53, 208.64) * mm});
            skLineSegment(sketch, "E6.32.0.0", {"start": v(-12.53, 208.64) * mm, "end": v(-12.53, 203.56) * mm});
            skLineSegment(sketch, "E6.32.0.1", {"start": v(-12.53, 203.56) * mm, "end": v(-6.18, 203.56) * mm});
            skLineSegment(sketch, "E6.32.0.2", {"start": v(-6.18, 208.64) * mm, "end": v(-6.18, 203.56) * mm});
            skLineSegment(sketch, "E6.32.0.3", {"start": v(-6.18, 208.64) * mm, "end": v(0.17, 208.64) * mm});
            skLineSegment(sketch, "E6.33.0.0", {"start": v(0.17, 208.64) * mm, "end": v(0.17, 203.56) * mm});
            skLineSegment(sketch, "E6.33.0.1", {"start": v(0.17, 203.56) * mm, "end": v(6.52, 203.56) * mm});
            skLineSegment(sketch, "E6.33.0.2", {"start": v(6.52, 208.64) * mm, "end": v(6.52, 203.56) * mm});
            skLineSegment(sketch, "E6.33.0.3", {"start": v(6.52, 208.64) * mm, "end": v(12.87, 208.64) * mm});
            skLineSegment(sketch, "E6.34.0.0", {"start": v(12.87, 208.64) * mm, "end": v(12.87, 203.56) * mm});
            skLineSegment(sketch, "E6.34.0.1", {"start": v(12.87, 203.56) * mm, "end": v(19.22, 203.56) * mm});
            skLineSegment(sketch, "E6.34.0.2", {"start": v(19.22, 208.64) * mm, "end": v(19.22, 203.56) * mm});
            skLineSegment(sketch, "E6.34.0.3", {"start": v(19.22, 208.64) * mm, "end": v(25.57, 208.64) * mm});
            skLineSegment(sketch, "E6.35.0.0", {"start": v(25.57, 208.64) * mm, "end": v(25.57, 203.56) * mm});
            skLineSegment(sketch, "E6.35.0.1", {"start": v(25.57, 203.56) * mm, "end": v(31.92, 203.56) * mm});
            skLineSegment(sketch, "E6.35.0.2", {"start": v(31.92, 208.64) * mm, "end": v(31.92, 203.56) * mm});
            skLineSegment(sketch, "E6.35.0.3", {"start": v(31.92, 208.64) * mm, "end": v(38.27, 208.64) * mm});
            skLineSegment(sketch, "E6.36.0.0", {"start": v(38.27, 208.64) * mm, "end": v(38.27, 203.56) * mm});
            skLineSegment(sketch, "E6.36.0.1", {"start": v(38.27, 203.56) * mm, "end": v(44.62, 203.56) * mm});
            skLineSegment(sketch, "E6.36.0.2", {"start": v(44.62, 208.64) * mm, "end": v(44.62, 203.56) * mm});
            skLineSegment(sketch, "E6.36.0.3", {"start": v(44.62, 208.64) * mm, "end": v(50.97, 208.64) * mm});
            skLineSegment(sketch, "E6.37.0.0", {"start": v(50.97, 208.64) * mm, "end": v(50.97, 203.56) * mm});
            skLineSegment(sketch, "E6.37.0.1", {"start": v(50.97, 203.56) * mm, "end": v(57.32, 203.56) * mm});
            skLineSegment(sketch, "E6.37.0.2", {"start": v(57.32, 208.64) * mm, "end": v(57.32, 203.56) * mm});
            skLineSegment(sketch, "E6.37.0.3", {"start": v(57.32, 208.64) * mm, "end": v(63.67, 208.64) * mm});
            skLineSegment(sketch, "E6.38.0.0", {"start": v(63.67, 208.64) * mm, "end": v(63.67, 203.56) * mm});
            skLineSegment(sketch, "E6.38.0.1", {"start": v(63.67, 203.56) * mm, "end": v(70.02, 203.56) * mm});
            skLineSegment(sketch, "E6.38.0.2", {"start": v(70.02, 208.64) * mm, "end": v(70.02, 203.56) * mm});
            skLineSegment(sketch, "E6.38.0.3", {"start": v(70.02, 208.64) * mm, "end": v(76.37, 208.64) * mm});
            skLineSegment(sketch, "E6.39.0.0", {"start": v(76.37, 208.64) * mm, "end": v(76.37, 203.56) * mm});
            skLineSegment(sketch, "E6.39.0.1", {"start": v(76.37, 203.56) * mm, "end": v(82.72, 203.56) * mm});
            skLineSegment(sketch, "E6.39.0.2", {"start": v(82.72, 208.64) * mm, "end": v(82.72, 203.56) * mm});
            skLineSegment(sketch, "E6.39.0.3", {"start": v(82.72, 208.64) * mm, "end": v(89.07, 208.64) * mm});
            skLineSegment(sketch, "E6.40.0.0", {"start": v(89.07, 208.64) * mm, "end": v(89.07, 203.56) * mm});
            skLineSegment(sketch, "E6.40.0.1", {"start": v(89.07, 203.56) * mm, "end": v(95.42, 203.56) * mm});
            skLineSegment(sketch, "E6.40.0.2", {"start": v(95.42, 208.64) * mm, "end": v(95.42, 203.56) * mm});
            skLineSegment(sketch, "E6.40.0.3", {"start": v(95.42, 208.64) * mm, "end": v(101.77, 208.64) * mm});
            skLineSegment(sketch, "E6.41.0.0", {"start": v(101.77, 208.64) * mm, "end": v(101.77, 203.56) * mm});
            skLineSegment(sketch, "E6.41.0.1", {"start": v(101.77, 203.56) * mm, "end": v(108.12, 203.56) * mm});
            skLineSegment(sketch, "E6.41.0.2", {"start": v(108.12, 208.64) * mm, "end": v(108.12, 203.56) * mm});
            skLineSegment(sketch, "E6.41.0.3", {"start": v(108.12, 208.64) * mm, "end": v(114.47, 208.64) * mm});
            skLineSegment(sketch, "E6.42.0.0", {"start": v(114.47, 208.64) * mm, "end": v(114.47, 203.56) * mm});
            skLineSegment(sketch, "E6.42.0.1", {"start": v(114.47, 203.56) * mm, "end": v(120.82, 203.56) * mm});
            skLineSegment(sketch, "E6.42.0.2", {"start": v(120.82, 208.64) * mm, "end": v(120.82, 203.56) * mm});
            skLineSegment(sketch, "E6.42.0.3", {"start": v(120.82, 208.64) * mm, "end": v(127.17, 208.64) * mm});
            skLineSegment(sketch, "E6.43.0.0", {"start": v(127.17, 208.64) * mm, "end": v(127.17, 203.56) * mm});
            skLineSegment(sketch, "E6.43.0.1", {"start": v(127.17, 203.56) * mm, "end": v(133.52, 203.56) * mm});
            skLineSegment(sketch, "E6.43.0.2", {"start": v(133.52, 208.64) * mm, "end": v(133.52, 203.56) * mm});
            skLineSegment(sketch, "E6.43.0.3", {"start": v(133.52, 208.64) * mm, "end": v(139.87, 208.64) * mm});
            skLineSegment(sketch, "E6.44.0.0", {"start": v(139.87, 208.64) * mm, "end": v(139.87, 203.56) * mm});
            skLineSegment(sketch, "E6.44.0.1", {"start": v(139.87, 203.56) * mm, "end": v(146.22, 203.56) * mm});
            skLineSegment(sketch, "E6.44.0.2", {"start": v(146.22, 208.64) * mm, "end": v(146.22, 203.56) * mm});
            skLineSegment(sketch, "E6.44.0.3", {"start": v(146.22, 208.64) * mm, "end": v(152.57, 208.64) * mm});
            skLineSegment(sketch, "E6.45.0.0", {"start": v(152.57, 208.64) * mm, "end": v(152.57, 203.56) * mm});
            skLineSegment(sketch, "E6.45.0.1", {"start": v(152.57, 203.56) * mm, "end": v(158.92, 203.56) * mm});
            skLineSegment(sketch, "E6.45.0.2", {"start": v(158.92, 208.64) * mm, "end": v(158.92, 203.56) * mm});
            skLineSegment(sketch, "E6.45.0.3", {"start": v(158.92, 208.64) * mm, "end": v(165.27, 208.64) * mm});
            skLineSegment(sketch, "E6.46.0.0", {"start": v(165.27, 208.64) * mm, "end": v(165.27, 203.56) * mm});
            skLineSegment(sketch, "E6.46.0.1", {"start": v(165.27, 203.56) * mm, "end": v(171.62, 203.56) * mm});
            skLineSegment(sketch, "E6.46.0.2", {"start": v(171.62, 208.64) * mm, "end": v(171.62, 203.56) * mm});
            skLineSegment(sketch, "E6.46.0.3", {"start": v(171.62, 208.64) * mm, "end": v(177.97, 208.64) * mm});
            skLineSegment(sketch, "E6.47.0.0", {"start": v(177.97, 208.64) * mm, "end": v(177.97, 203.56) * mm});
            skLineSegment(sketch, "E6.47.0.1", {"start": v(177.97, 203.56) * mm, "end": v(184.32, 203.56) * mm});
            skLineSegment(sketch, "E6.47.0.2", {"start": v(184.32, 208.64) * mm, "end": v(184.32, 203.56) * mm});
            skLineSegment(sketch, "E6.47.0.3", {"start": v(184.32, 208.64) * mm, "end": v(190.67, 208.64) * mm});
            skLineSegment(sketch, "E6.48.0.0", {"start": v(190.67, 208.64) * mm, "end": v(190.67, 203.56) * mm});
            skLineSegment(sketch, "E6.48.0.1", {"start": v(190.67, 203.56) * mm, "end": v(197.02, 203.56) * mm});
            skLineSegment(sketch, "E6.48.0.2", {"start": v(197.02, 208.64) * mm, "end": v(197.02, 203.56) * mm});
            skLineSegment(sketch, "E6.48.0.3", {"start": v(197.02, 208.64) * mm, "end": v(203.37, 208.64) * mm});
            skLineSegment(sketch, "E6.49.0.0", {"start": v(203.37, 208.64) * mm, "end": v(203.37, 203.56) * mm});
            skLineSegment(sketch, "E6.direction1", {"start": v(-418.93, 208.64) * mm, "end": v(-406.23, 208.64) * mm, "construction": true});
            skLineSegment(sketch, "E7", {"start": v(206.55, 245.47) * mm, "end": v(211.63, 245.47) * mm});
            skLineSegment(sketch, "E8", {"start": v(211.63, 245.47) * mm, "end": v(211.63, 239.12) * mm});
            skLineSegment(sketch, "E9", {"start": v(206.55, 239.12) * mm, "end": v(211.63, 239.12) * mm});
            skLineSegment(sketch, "E10", {"start": v(206.55, 239.12) * mm, "end": v(206.55, 232.77) * mm});
            skLineSegment(sketch, "E11", {"start": v(211.63, 232.77) * mm, "end": v(206.55, 232.77) * mm});
            skLineSegment(sketch, "E12", {"start": v(211.63, 232.77) * mm, "end": v(211.63, 226.42) * mm});
            skLineSegment(sketch, "E13", {"start": v(206.55, 226.42) * mm, "end": v(211.63, 226.42) * mm});
            skLineSegment(sketch, "E14", {"start": v(206.55, 226.42) * mm, "end": v(206.55, 220.07) * mm});
            skLineSegment(sketch, "E15", {"start": v(211.63, 220.07) * mm, "end": v(206.55, 220.07) * mm});
            skLineSegment(sketch, "E16", {"start": v(211.63, 220.07) * mm, "end": v(211.63, 213.72) * mm});
            skLineSegment(sketch, "E17", {"start": v(206.55, 213.72) * mm, "end": v(211.63, 213.72) * mm});
            skLineSegment(sketch, "E18", {"start": v(206.55, 213.72) * mm, "end": v(206.55, 203.56) * mm});
            skLineSegment(sketch, "E19", {"start": v(-423.37, 245.47) * mm, "end": v(-428.45, 245.47) * mm});
            skLineSegment(sketch, "E20", {"start": v(-423.37, 245.47) * mm, "end": v(-423.37, 239.12) * mm});
            skLineSegment(sketch, "E21", {"start": v(-428.45, 239.12) * mm, "end": v(-423.37, 239.12) * mm});
            skLineSegment(sketch, "E22", {"start": v(-428.45, 239.12) * mm, "end": v(-428.45, 232.77) * mm});
            skLineSegment(sketch, "E23", {"start": v(-423.37, 232.77) * mm, "end": v(-428.45, 232.77) * mm});
            skLineSegment(sketch, "E24", {"start": v(-423.37, 232.77) * mm, "end": v(-423.37, 226.42) * mm});
            skLineSegment(sketch, "E25", {"start": v(-428.45, 226.42) * mm, "end": v(-423.37, 226.42) * mm});
            skLineSegment(sketch, "E26", {"start": v(-428.45, 226.42) * mm, "end": v(-428.45, 220.07) * mm});
            skLineSegment(sketch, "E27", {"start": v(-423.37, 220.07) * mm, "end": v(-428.45, 220.07) * mm});
            skLineSegment(sketch, "E28", {"start": v(-423.37, 220.07) * mm, "end": v(-423.37, 213.72) * mm});
            skLineSegment(sketch, "E29", {"start": v(-428.45, 213.72) * mm, "end": v(-423.37, 213.72) * mm});
            skLineSegment(sketch, "E30", {"start": v(206.55, 255.63) * mm, "end": v(206.55, 245.47) * mm});
            skLineSegment(sketch, "E31", {"start": v(-428.45, 213.72) * mm, "end": v(-428.45, 203.56) * mm});
            skLineSegment(sketch, "E32", {"start": v(203.37, 255.63) * mm, "end": v(206.55, 255.63) * mm});
            skLineSegment(sketch, "E33", {"start": v(203.37, 203.56) * mm, "end": v(206.55, 203.56) * mm});
            skLineSegment(sketch, "E34", {"start": v(-418.93, 250.55) * mm, "end": v(-425.28, 250.55) * mm});
            skLineSegment(sketch, "E35", {"start": v(-425.28, 250.55) * mm, "end": v(-425.28, 255.63) * mm});
            skLineSegment(sketch, "E36", {"start": v(-425.28, 255.63) * mm, "end": v(-428.45, 255.63) * mm});
            skLineSegment(sketch, "E37", {"start": v(-428.45, 255.63) * mm, "end": v(-428.45, 245.47) * mm});
            skLineSegment(sketch, "E38", {"start": v(-428.45, 203.56) * mm, "end": v(-425.28, 203.56) * mm});
            skLineSegment(sketch, "E39", {"start": v(-425.28, 203.56) * mm, "end": v(-425.28, 208.64) * mm});
            skLineSegment(sketch, "E40", {"start": v(-425.28, 208.64) * mm, "end": v(-418.93, 208.64) * mm});
            skLineSegment(sketch, "E41", {"start": v(-428.45, 203.56) * mm, "end": v(-428.45, 197.2) * mm});
            skLineSegment(sketch, "E42", {"start": v(-428.45, 197.2) * mm, "end": v(-423.37, 197.2) * mm});
            skLineSegment(sketch, "E43", {"start": v(-423.37, 197.2) * mm, "end": v(-423.37, 190.86) * mm});
            skLineSegment(sketch, "E44", {"start": v(-423.37, 190.86) * mm, "end": v(-428.45, 190.86) * mm});
            skLineSegment(sketch, "E45", {"start": v(-428.45, 190.86) * mm, "end": v(-428.45, 184.5) * mm});
            skLineSegment(sketch, "E46", {"start": v(-428.45, 184.5) * mm, "end": v(-423.37, 184.5) * mm});
            skLineSegment(sketch, "E47", {"start": v(-423.37, 184.5) * mm, "end": v(-423.37, 178.16) * mm});
            skLineSegment(sketch, "E48", {"start": v(-423.37, 178.16) * mm, "end": v(-428.45, 178.16) * mm});
            skLineSegment(sketch, "E49", {"start": v(-428.45, 178.16) * mm, "end": v(-428.45, 171.8) * mm});
            skLineSegment(sketch, "E50", {"start": v(-428.45, 171.8) * mm, "end": v(-423.37, 171.8) * mm});
            skLineSegment(sketch, "E51", {"start": v(-423.37, 171.8) * mm, "end": v(-423.37, 165.46) * mm});
            skLineSegment(sketch, "E52", {"start": v(-423.37, 165.46) * mm, "end": v(-428.45, 165.46) * mm});
            skLineSegment(sketch, "E53", {"start": v(-428.45, 165.46) * mm, "end": v(-428.45, 159.1) * mm});
            skLineSegment(sketch, "E54", {"start": v(-428.45, 159.1) * mm, "end": v(-425.28, 159.1) * mm});
            skLineSegment(sketch, "E55", {"start": v(-425.28, 159.1) * mm, "end": v(-425.28, 154.03) * mm});
            skLineSegment(sketch, "E56", {"start": v(-425.28, 154.03) * mm, "end": v(-418.93, 154.03) * mm});
            skLineSegment(sketch, "E57", {"start": v(-418.93, 154.03) * mm, "end": v(-418.93, 159.1) * mm});
            skLineSegment(sketch, "E58", {"start": v(-418.93, 159.1) * mm, "end": v(-412.58, 159.1) * mm});
            skLineSegment(sketch, "E59.1.0.0", {"start": v(-412.58, 159.1) * mm, "end": v(-412.58, 154.03) * mm});
            skLineSegment(sketch, "E59.1.0.1", {"start": v(-412.58, 154.03) * mm, "end": v(-406.23, 154.03) * mm});
            skLineSegment(sketch, "E59.1.0.2", {"start": v(-406.23, 154.03) * mm, "end": v(-406.23, 159.1) * mm});
            skLineSegment(sketch, "E59.1.0.3", {"start": v(-406.23, 159.1) * mm, "end": v(-399.88, 159.1) * mm});
            skLineSegment(sketch, "E59.2.0.0", {"start": v(-399.88, 159.1) * mm, "end": v(-399.88, 154.03) * mm});
            skLineSegment(sketch, "E59.2.0.1", {"start": v(-399.88, 154.03) * mm, "end": v(-393.53, 154.03) * mm});
            skLineSegment(sketch, "E59.2.0.2", {"start": v(-393.53, 154.03) * mm, "end": v(-393.53, 159.1) * mm});
            skLineSegment(sketch, "E59.2.0.3", {"start": v(-393.53, 159.1) * mm, "end": v(-387.18, 159.1) * mm});
            skLineSegment(sketch, "E59.3.0.0", {"start": v(-387.18, 159.1) * mm, "end": v(-387.18, 154.03) * mm});
            skLineSegment(sketch, "E59.3.0.1", {"start": v(-387.18, 154.03) * mm, "end": v(-380.83, 154.03) * mm});
            skLineSegment(sketch, "E59.3.0.2", {"start": v(-380.83, 154.03) * mm, "end": v(-380.83, 159.1) * mm});
            skLineSegment(sketch, "E59.3.0.3", {"start": v(-380.83, 159.1) * mm, "end": v(-374.48, 159.1) * mm});
            skLineSegment(sketch, "E59.4.0.0", {"start": v(-374.48, 159.1) * mm, "end": v(-374.48, 154.03) * mm});
            skLineSegment(sketch, "E59.4.0.1", {"start": v(-374.48, 154.03) * mm, "end": v(-368.13, 154.03) * mm});
            skLineSegment(sketch, "E59.4.0.2", {"start": v(-368.13, 154.03) * mm, "end": v(-368.13, 159.1) * mm});
            skLineSegment(sketch, "E59.4.0.3", {"start": v(-368.13, 159.1) * mm, "end": v(-361.78, 159.1) * mm});
            skLineSegment(sketch, "E59.5.0.0", {"start": v(-361.78, 159.1) * mm, "end": v(-361.78, 154.03) * mm});
            skLineSegment(sketch, "E59.5.0.1", {"start": v(-361.78, 154.03) * mm, "end": v(-355.43, 154.03) * mm});
            skLineSegment(sketch, "E59.5.0.2", {"start": v(-355.43, 154.03) * mm, "end": v(-355.43, 159.1) * mm});
            skLineSegment(sketch, "E59.5.0.3", {"start": v(-355.43, 159.1) * mm, "end": v(-349.08, 159.1) * mm});
            skLineSegment(sketch, "E59.6.0.0", {"start": v(-349.08, 159.1) * mm, "end": v(-349.08, 154.03) * mm});
            skLineSegment(sketch, "E59.6.0.1", {"start": v(-349.08, 154.03) * mm, "end": v(-342.73, 154.03) * mm});
            skLineSegment(sketch, "E59.6.0.2", {"start": v(-342.73, 154.03) * mm, "end": v(-342.73, 159.1) * mm});
            skLineSegment(sketch, "E59.6.0.3", {"start": v(-342.73, 159.1) * mm, "end": v(-336.38, 159.1) * mm});
            skLineSegment(sketch, "E59.7.0.0", {"start": v(-336.38, 159.1) * mm, "end": v(-336.38, 154.03) * mm});
            skLineSegment(sketch, "E59.7.0.1", {"start": v(-336.38, 154.03) * mm, "end": v(-330.03, 154.03) * mm});
            skLineSegment(sketch, "E59.7.0.2", {"start": v(-330.03, 154.03) * mm, "end": v(-330.03, 159.1) * mm});
            skLineSegment(sketch, "E59.7.0.3", {"start": v(-330.03, 159.1) * mm, "end": v(-323.68, 159.1) * mm});
            skLineSegment(sketch, "E59.8.0.0", {"start": v(-323.68, 159.1) * mm, "end": v(-323.68, 154.03) * mm});
            skLineSegment(sketch, "E59.8.0.1", {"start": v(-323.68, 154.03) * mm, "end": v(-317.33, 154.03) * mm});
            skLineSegment(sketch, "E59.8.0.2", {"start": v(-317.33, 154.03) * mm, "end": v(-317.33, 159.1) * mm});
            skLineSegment(sketch, "E59.8.0.3", {"start": v(-317.33, 159.1) * mm, "end": v(-310.98, 159.1) * mm});
            skLineSegment(sketch, "E59.9.0.0", {"start": v(-310.98, 159.1) * mm, "end": v(-310.98, 154.03) * mm});
            skLineSegment(sketch, "E59.9.0.1", {"start": v(-310.98, 154.03) * mm, "end": v(-304.63, 154.03) * mm});
            skLineSegment(sketch, "E59.9.0.2", {"start": v(-304.63, 154.03) * mm, "end": v(-304.63, 159.1) * mm});
            skLineSegment(sketch, "E59.9.0.3", {"start": v(-304.63, 159.1) * mm, "end": v(-298.28, 159.1) * mm});
            skLineSegment(sketch, "E59.10.0.0", {"start": v(-298.28, 159.1) * mm, "end": v(-298.28, 154.03) * mm});
            skLineSegment(sketch, "E59.10.0.1", {"start": v(-298.28, 154.03) * mm, "end": v(-291.93, 154.03) * mm});
            skLineSegment(sketch, "E59.10.0.2", {"start": v(-291.93, 154.03) * mm, "end": v(-291.93, 159.1) * mm});
            skLineSegment(sketch, "E59.10.0.3", {"start": v(-291.93, 159.1) * mm, "end": v(-285.58, 159.1) * mm});
            skLineSegment(sketch, "E59.11.0.0", {"start": v(-285.58, 159.1) * mm, "end": v(-285.58, 154.03) * mm});
            skLineSegment(sketch, "E59.11.0.1", {"start": v(-285.58, 154.03) * mm, "end": v(-279.23, 154.03) * mm});
            skLineSegment(sketch, "E59.11.0.2", {"start": v(-279.23, 154.03) * mm, "end": v(-279.23, 159.1) * mm});
            skLineSegment(sketch, "E59.11.0.3", {"start": v(-279.23, 159.1) * mm, "end": v(-272.88, 159.1) * mm});
            skLineSegment(sketch, "E59.12.0.0", {"start": v(-272.88, 159.1) * mm, "end": v(-272.88, 154.03) * mm});
            skLineSegment(sketch, "E59.12.0.1", {"start": v(-272.88, 154.03) * mm, "end": v(-266.53, 154.03) * mm});
            skLineSegment(sketch, "E59.12.0.2", {"start": v(-266.53, 154.03) * mm, "end": v(-266.53, 159.1) * mm});
            skLineSegment(sketch, "E59.12.0.3", {"start": v(-266.53, 159.1) * mm, "end": v(-260.18, 159.1) * mm});
            skLineSegment(sketch, "E59.13.0.0", {"start": v(-260.18, 159.1) * mm, "end": v(-260.18, 154.03) * mm});
            skLineSegment(sketch, "E59.13.0.1", {"start": v(-260.18, 154.03) * mm, "end": v(-253.83, 154.03) * mm});
            skLineSegment(sketch, "E59.13.0.2", {"start": v(-253.83, 154.03) * mm, "end": v(-253.83, 159.1) * mm});
            skLineSegment(sketch, "E59.13.0.3", {"start": v(-253.83, 159.1) * mm, "end": v(-247.48, 159.1) * mm});
            skLineSegment(sketch, "E59.14.0.0", {"start": v(-247.48, 159.1) * mm, "end": v(-247.48, 154.03) * mm});
            skLineSegment(sketch, "E59.14.0.1", {"start": v(-247.48, 154.03) * mm, "end": v(-241.13, 154.03) * mm});
            skLineSegment(sketch, "E59.14.0.2", {"start": v(-241.13, 154.03) * mm, "end": v(-241.13, 159.1) * mm});
            skLineSegment(sketch, "E59.14.0.3", {"start": v(-241.13, 159.1) * mm, "end": v(-234.78, 159.1) * mm});
            skLineSegment(sketch, "E59.15.0.0", {"start": v(-234.78, 159.1) * mm, "end": v(-234.78, 154.03) * mm});
            skLineSegment(sketch, "E59.15.0.1", {"start": v(-234.78, 154.03) * mm, "end": v(-228.43, 154.03) * mm});
            skLineSegment(sketch, "E59.15.0.2", {"start": v(-228.43, 154.03) * mm, "end": v(-228.43, 159.1) * mm});
            skLineSegment(sketch, "E59.15.0.3", {"start": v(-228.43, 159.1) * mm, "end": v(-222.08, 159.1) * mm});
            skLineSegment(sketch, "E59.16.0.0", {"start": v(-222.08, 159.1) * mm, "end": v(-222.08, 154.03) * mm});
            skLineSegment(sketch, "E59.16.0.1", {"start": v(-222.08, 154.03) * mm, "end": v(-215.73, 154.03) * mm});
            skLineSegment(sketch, "E59.16.0.2", {"start": v(-215.73, 154.03) * mm, "end": v(-215.73, 159.1) * mm});
            skLineSegment(sketch, "E59.16.0.3", {"start": v(-215.73, 159.1) * mm, "end": v(-209.38, 159.1) * mm});
            skLineSegment(sketch, "E59.17.0.0", {"start": v(-209.38, 159.1) * mm, "end": v(-209.38, 154.03) * mm});
            skLineSegment(sketch, "E59.17.0.1", {"start": v(-209.38, 154.03) * mm, "end": v(-203.03, 154.03) * mm});
            skLineSegment(sketch, "E59.17.0.2", {"start": v(-203.03, 154.03) * mm, "end": v(-203.03, 159.1) * mm});
            skLineSegment(sketch, "E59.17.0.3", {"start": v(-203.03, 159.1) * mm, "end": v(-196.68, 159.1) * mm});
            skLineSegment(sketch, "E59.18.0.0", {"start": v(-196.68, 159.1) * mm, "end": v(-196.68, 154.03) * mm});
            skLineSegment(sketch, "E59.18.0.1", {"start": v(-196.68, 154.03) * mm, "end": v(-190.33, 154.03) * mm});
            skLineSegment(sketch, "E59.18.0.2", {"start": v(-190.33, 154.03) * mm, "end": v(-190.33, 159.1) * mm});
            skLineSegment(sketch, "E59.18.0.3", {"start": v(-190.33, 159.1) * mm, "end": v(-183.98, 159.1) * mm});
            skLineSegment(sketch, "E59.19.0.0", {"start": v(-183.98, 159.1) * mm, "end": v(-183.98, 154.03) * mm});
            skLineSegment(sketch, "E59.19.0.1", {"start": v(-183.98, 154.03) * mm, "end": v(-177.63, 154.03) * mm});
            skLineSegment(sketch, "E59.19.0.2", {"start": v(-177.63, 154.03) * mm, "end": v(-177.63, 159.1) * mm});
            skLineSegment(sketch, "E59.19.0.3", {"start": v(-177.63, 159.1) * mm, "end": v(-171.28, 159.1) * mm});
            skLineSegment(sketch, "E59.20.0.0", {"start": v(-171.28, 159.1) * mm, "end": v(-171.28, 154.03) * mm});
            skLineSegment(sketch, "E59.20.0.1", {"start": v(-171.28, 154.03) * mm, "end": v(-164.93, 154.03) * mm});
            skLineSegment(sketch, "E59.20.0.2", {"start": v(-164.93, 154.03) * mm, "end": v(-164.93, 159.1) * mm});
            skLineSegment(sketch, "E59.20.0.3", {"start": v(-164.93, 159.1) * mm, "end": v(-158.58, 159.1) * mm});
            skLineSegment(sketch, "E59.21.0.0", {"start": v(-158.58, 159.1) * mm, "end": v(-158.58, 154.03) * mm});
            skLineSegment(sketch, "E59.21.0.1", {"start": v(-158.58, 154.03) * mm, "end": v(-152.23, 154.03) * mm});
            skLineSegment(sketch, "E59.21.0.2", {"start": v(-152.23, 154.03) * mm, "end": v(-152.23, 159.1) * mm});
            skLineSegment(sketch, "E59.21.0.3", {"start": v(-152.23, 159.1) * mm, "end": v(-145.88, 159.1) * mm});
            skLineSegment(sketch, "E59.22.0.0", {"start": v(-145.88, 159.1) * mm, "end": v(-145.88, 154.03) * mm});
            skLineSegment(sketch, "E59.22.0.1", {"start": v(-145.88, 154.03) * mm, "end": v(-139.53, 154.03) * mm});
            skLineSegment(sketch, "E59.22.0.2", {"start": v(-139.53, 154.03) * mm, "end": v(-139.53, 159.1) * mm});
            skLineSegment(sketch, "E59.22.0.3", {"start": v(-139.53, 159.1) * mm, "end": v(-133.18, 159.1) * mm});
            skLineSegment(sketch, "E59.23.0.0", {"start": v(-133.18, 159.1) * mm, "end": v(-133.18, 154.03) * mm});
            skLineSegment(sketch, "E59.23.0.1", {"start": v(-133.18, 154.03) * mm, "end": v(-126.83, 154.03) * mm});
            skLineSegment(sketch, "E59.23.0.2", {"start": v(-126.83, 154.03) * mm, "end": v(-126.83, 159.1) * mm});
            skLineSegment(sketch, "E59.23.0.3", {"start": v(-126.83, 159.1) * mm, "end": v(-120.48, 159.1) * mm});
            skLineSegment(sketch, "E59.24.0.0", {"start": v(-120.48, 159.1) * mm, "end": v(-120.48, 154.03) * mm});
            skLineSegment(sketch, "E59.24.0.1", {"start": v(-120.48, 154.03) * mm, "end": v(-114.13, 154.03) * mm});
            skLineSegment(sketch, "E59.24.0.2", {"start": v(-114.13, 154.03) * mm, "end": v(-114.13, 159.1) * mm});
            skLineSegment(sketch, "E59.24.0.3", {"start": v(-114.13, 159.1) * mm, "end": v(-107.78, 159.1) * mm});
            skLineSegment(sketch, "E59.25.0.0", {"start": v(-107.78, 159.1) * mm, "end": v(-107.78, 154.03) * mm});
            skLineSegment(sketch, "E59.25.0.1", {"start": v(-107.78, 154.03) * mm, "end": v(-101.43, 154.03) * mm});
            skLineSegment(sketch, "E59.25.0.2", {"start": v(-101.43, 154.03) * mm, "end": v(-101.43, 159.1) * mm});
            skLineSegment(sketch, "E59.25.0.3", {"start": v(-101.43, 159.1) * mm, "end": v(-95.08, 159.1) * mm});
            skLineSegment(sketch, "E59.26.0.0", {"start": v(-95.08, 159.1) * mm, "end": v(-95.08, 154.03) * mm});
            skLineSegment(sketch, "E59.26.0.1", {"start": v(-95.08, 154.03) * mm, "end": v(-88.73, 154.03) * mm});
            skLineSegment(sketch, "E59.26.0.2", {"start": v(-88.73, 154.03) * mm, "end": v(-88.73, 159.1) * mm});
            skLineSegment(sketch, "E59.26.0.3", {"start": v(-88.73, 159.1) * mm, "end": v(-82.38, 159.1) * mm});
            skLineSegment(sketch, "E59.27.0.0", {"start": v(-82.38, 159.1) * mm, "end": v(-82.38, 154.03) * mm});
            skLineSegment(sketch, "E59.27.0.1", {"start": v(-82.38, 154.03) * mm, "end": v(-76.03, 154.03) * mm});
            skLineSegment(sketch, "E59.27.0.2", {"start": v(-76.03, 154.03) * mm, "end": v(-76.03, 159.1) * mm});
            skLineSegment(sketch, "E59.27.0.3", {"start": v(-76.03, 159.1) * mm, "end": v(-69.68, 159.1) * mm});
            skLineSegment(sketch, "E59.28.0.0", {"start": v(-69.68, 159.1) * mm, "end": v(-69.68, 154.03) * mm});
            skLineSegment(sketch, "E59.28.0.1", {"start": v(-69.68, 154.03) * mm, "end": v(-63.33, 154.03) * mm});
            skLineSegment(sketch, "E59.28.0.2", {"start": v(-63.33, 154.03) * mm, "end": v(-63.33, 159.1) * mm});
            skLineSegment(sketch, "E59.28.0.3", {"start": v(-63.33, 159.1) * mm, "end": v(-56.98, 159.1) * mm});
            skLineSegment(sketch, "E59.29.0.0", {"start": v(-56.98, 159.1) * mm, "end": v(-56.98, 154.03) * mm});
            skLineSegment(sketch, "E59.29.0.1", {"start": v(-56.98, 154.03) * mm, "end": v(-50.63, 154.03) * mm});
            skLineSegment(sketch, "E59.29.0.2", {"start": v(-50.63, 154.03) * mm, "end": v(-50.63, 159.1) * mm});
            skLineSegment(sketch, "E59.29.0.3", {"start": v(-50.63, 159.1) * mm, "end": v(-44.28, 159.1) * mm});
            skLineSegment(sketch, "E59.30.0.0", {"start": v(-44.28, 159.1) * mm, "end": v(-44.28, 154.03) * mm});
            skLineSegment(sketch, "E59.30.0.1", {"start": v(-44.28, 154.03) * mm, "end": v(-37.93, 154.03) * mm});
            skLineSegment(sketch, "E59.30.0.2", {"start": v(-37.93, 154.03) * mm, "end": v(-37.93, 159.1) * mm});
            skLineSegment(sketch, "E59.30.0.3", {"start": v(-37.93, 159.1) * mm, "end": v(-31.58, 159.1) * mm});
            skLineSegment(sketch, "E59.31.0.0", {"start": v(-31.58, 159.1) * mm, "end": v(-31.58, 154.03) * mm});
            skLineSegment(sketch, "E59.31.0.1", {"start": v(-31.58, 154.03) * mm, "end": v(-25.23, 154.03) * mm});
            skLineSegment(sketch, "E59.31.0.2", {"start": v(-25.23, 154.03) * mm, "end": v(-25.23, 159.1) * mm});
            skLineSegment(sketch, "E59.31.0.3", {"start": v(-25.23, 159.1) * mm, "end": v(-18.88, 159.1) * mm});
            skLineSegment(sketch, "E59.32.0.0", {"start": v(-18.88, 159.1) * mm, "end": v(-18.88, 154.03) * mm});
            skLineSegment(sketch, "E59.32.0.1", {"start": v(-18.88, 154.03) * mm, "end": v(-12.53, 154.03) * mm});
            skLineSegment(sketch, "E59.32.0.2", {"start": v(-12.53, 154.03) * mm, "end": v(-12.53, 159.1) * mm});
            skLineSegment(sketch, "E59.32.0.3", {"start": v(-12.53, 159.1) * mm, "end": v(-6.18, 159.1) * mm});
            skLineSegment(sketch, "E59.33.0.0", {"start": v(-6.18, 159.1) * mm, "end": v(-6.18, 154.03) * mm});
            skLineSegment(sketch, "E59.33.0.1", {"start": v(-6.18, 154.03) * mm, "end": v(0.17, 154.03) * mm});
            skLineSegment(sketch, "E59.33.0.2", {"start": v(0.17, 154.03) * mm, "end": v(0.17, 159.1) * mm});
            skLineSegment(sketch, "E59.33.0.3", {"start": v(0.17, 159.1) * mm, "end": v(6.52, 159.1) * mm});
            skLineSegment(sketch, "E59.34.0.0", {"start": v(6.52, 159.1) * mm, "end": v(6.52, 154.03) * mm});
            skLineSegment(sketch, "E59.34.0.1", {"start": v(6.52, 154.03) * mm, "end": v(12.87, 154.03) * mm});
            skLineSegment(sketch, "E59.34.0.2", {"start": v(12.87, 154.03) * mm, "end": v(12.87, 159.1) * mm});
            skLineSegment(sketch, "E59.34.0.3", {"start": v(12.87, 159.1) * mm, "end": v(19.22, 159.1) * mm});
            skLineSegment(sketch, "E59.35.0.0", {"start": v(19.22, 159.1) * mm, "end": v(19.22, 154.03) * mm});
            skLineSegment(sketch, "E59.35.0.1", {"start": v(19.22, 154.03) * mm, "end": v(25.57, 154.03) * mm});
            skLineSegment(sketch, "E59.35.0.2", {"start": v(25.57, 154.03) * mm, "end": v(25.57, 159.1) * mm});
            skLineSegment(sketch, "E59.35.0.3", {"start": v(25.57, 159.1) * mm, "end": v(31.92, 159.1) * mm});
            skLineSegment(sketch, "E59.36.0.0", {"start": v(31.92, 159.1) * mm, "end": v(31.92, 154.03) * mm});
            skLineSegment(sketch, "E59.36.0.1", {"start": v(31.92, 154.03) * mm, "end": v(38.27, 154.03) * mm});
            skLineSegment(sketch, "E59.36.0.2", {"start": v(38.27, 154.03) * mm, "end": v(38.27, 159.1) * mm});
            skLineSegment(sketch, "E59.36.0.3", {"start": v(38.27, 159.1) * mm, "end": v(44.62, 159.1) * mm});
            skLineSegment(sketch, "E59.37.0.0", {"start": v(44.62, 159.1) * mm, "end": v(44.62, 154.03) * mm});
            skLineSegment(sketch, "E59.37.0.1", {"start": v(44.62, 154.03) * mm, "end": v(50.97, 154.03) * mm});
            skLineSegment(sketch, "E59.37.0.2", {"start": v(50.97, 154.03) * mm, "end": v(50.97, 159.1) * mm});
            skLineSegment(sketch, "E59.37.0.3", {"start": v(50.97, 159.1) * mm, "end": v(57.32, 159.1) * mm});
            skLineSegment(sketch, "E59.38.0.0", {"start": v(57.32, 159.1) * mm, "end": v(57.32, 154.03) * mm});
            skLineSegment(sketch, "E59.38.0.1", {"start": v(57.32, 154.03) * mm, "end": v(63.67, 154.03) * mm});
            skLineSegment(sketch, "E59.38.0.2", {"start": v(63.67, 154.03) * mm, "end": v(63.67, 159.1) * mm});
            skLineSegment(sketch, "E59.38.0.3", {"start": v(63.67, 159.1) * mm, "end": v(70.02, 159.1) * mm});
            skLineSegment(sketch, "E59.39.0.0", {"start": v(70.02, 159.1) * mm, "end": v(70.02, 154.03) * mm});
            skLineSegment(sketch, "E59.39.0.1", {"start": v(70.02, 154.03) * mm, "end": v(76.37, 154.03) * mm});
            skLineSegment(sketch, "E59.39.0.2", {"start": v(76.37, 154.03) * mm, "end": v(76.37, 159.1) * mm});
            skLineSegment(sketch, "E59.39.0.3", {"start": v(76.37, 159.1) * mm, "end": v(82.72, 159.1) * mm});
            skLineSegment(sketch, "E59.40.0.0", {"start": v(82.72, 159.1) * mm, "end": v(82.72, 154.03) * mm});
            skLineSegment(sketch, "E59.40.0.1", {"start": v(82.72, 154.03) * mm, "end": v(89.07, 154.03) * mm});
            skLineSegment(sketch, "E59.40.0.2", {"start": v(89.07, 154.03) * mm, "end": v(89.07, 159.1) * mm});
            skLineSegment(sketch, "E59.40.0.3", {"start": v(89.07, 159.1) * mm, "end": v(95.42, 159.1) * mm});
            skLineSegment(sketch, "E59.41.0.0", {"start": v(95.42, 159.1) * mm, "end": v(95.42, 154.03) * mm});
            skLineSegment(sketch, "E59.41.0.1", {"start": v(95.42, 154.03) * mm, "end": v(101.77, 154.03) * mm});
            skLineSegment(sketch, "E59.41.0.2", {"start": v(101.77, 154.03) * mm, "end": v(101.77, 159.1) * mm});
            skLineSegment(sketch, "E59.41.0.3", {"start": v(101.77, 159.1) * mm, "end": v(108.12, 159.1) * mm});
            skLineSegment(sketch, "E59.42.0.0", {"start": v(108.12, 159.1) * mm, "end": v(108.12, 154.03) * mm});
            skLineSegment(sketch, "E59.42.0.1", {"start": v(108.12, 154.03) * mm, "end": v(114.47, 154.03) * mm});
            skLineSegment(sketch, "E59.42.0.2", {"start": v(114.47, 154.03) * mm, "end": v(114.47, 159.1) * mm});
            skLineSegment(sketch, "E59.42.0.3", {"start": v(114.47, 159.1) * mm, "end": v(120.82, 159.1) * mm});
            skLineSegment(sketch, "E59.43.0.0", {"start": v(120.82, 159.1) * mm, "end": v(120.82, 154.03) * mm});
            skLineSegment(sketch, "E59.43.0.1", {"start": v(120.82, 154.03) * mm, "end": v(127.17, 154.03) * mm});
            skLineSegment(sketch, "E59.43.0.2", {"start": v(127.17, 154.03) * mm, "end": v(127.17, 159.1) * mm});
            skLineSegment(sketch, "E59.43.0.3", {"start": v(127.17, 159.1) * mm, "end": v(133.52, 159.1) * mm});
            skLineSegment(sketch, "E59.44.0.0", {"start": v(133.52, 159.1) * mm, "end": v(133.52, 154.03) * mm});
            skLineSegment(sketch, "E59.44.0.1", {"start": v(133.52, 154.03) * mm, "end": v(139.87, 154.03) * mm});
            skLineSegment(sketch, "E59.44.0.2", {"start": v(139.87, 154.03) * mm, "end": v(139.87, 159.1) * mm});
            skLineSegment(sketch, "E59.44.0.3", {"start": v(139.87, 159.1) * mm, "end": v(146.22, 159.1) * mm});
            skLineSegment(sketch, "E59.45.0.0", {"start": v(146.22, 159.1) * mm, "end": v(146.22, 154.03) * mm});
            skLineSegment(sketch, "E59.45.0.1", {"start": v(146.22, 154.03) * mm, "end": v(152.57, 154.03) * mm});
            skLineSegment(sketch, "E59.45.0.2", {"start": v(152.57, 154.03) * mm, "end": v(152.57, 159.1) * mm});
            skLineSegment(sketch, "E59.45.0.3", {"start": v(152.57, 159.1) * mm, "end": v(158.92, 159.1) * mm});
            skLineSegment(sketch, "E59.46.0.0", {"start": v(158.92, 159.1) * mm, "end": v(158.92, 154.03) * mm});
            skLineSegment(sketch, "E59.46.0.1", {"start": v(158.92, 154.03) * mm, "end": v(165.27, 154.03) * mm});
            skLineSegment(sketch, "E59.46.0.2", {"start": v(165.27, 154.03) * mm, "end": v(165.27, 159.1) * mm});
            skLineSegment(sketch, "E59.46.0.3", {"start": v(165.27, 159.1) * mm, "end": v(171.62, 159.1) * mm});
            skLineSegment(sketch, "E59.47.0.0", {"start": v(171.62, 159.1) * mm, "end": v(171.62, 154.03) * mm});
            skLineSegment(sketch, "E59.47.0.1", {"start": v(171.62, 154.03) * mm, "end": v(177.97, 154.03) * mm});
            skLineSegment(sketch, "E59.47.0.2", {"start": v(177.97, 154.03) * mm, "end": v(177.97, 159.1) * mm});
            skLineSegment(sketch, "E59.47.0.3", {"start": v(177.97, 159.1) * mm, "end": v(184.32, 159.1) * mm});
            skLineSegment(sketch, "E59.48.0.0", {"start": v(184.32, 159.1) * mm, "end": v(184.32, 154.03) * mm});
            skLineSegment(sketch, "E59.48.0.1", {"start": v(184.32, 154.03) * mm, "end": v(190.67, 154.03) * mm});
            skLineSegment(sketch, "E59.48.0.2", {"start": v(190.67, 154.03) * mm, "end": v(190.67, 159.1) * mm});
            skLineSegment(sketch, "E59.48.0.3", {"start": v(190.67, 159.1) * mm, "end": v(197.02, 159.1) * mm});
            skLineSegment(sketch, "E59.direction1", {"start": v(-425.28, 154.03) * mm, "end": v(-412.58, 154.03) * mm, "construction": true});
            skLineSegment(sketch, "E60", {"start": v(197.02, 159.1) * mm, "end": v(197.02, 154.03) * mm});
            skLineSegment(sketch, "E61", {"start": v(197.02, 154.03) * mm, "end": v(203.37, 154.03) * mm});
            skLineSegment(sketch, "E62", {"start": v(203.37, 154.03) * mm, "end": v(203.37, 159.1) * mm});
            skLineSegment(sketch, "E63", {"start": v(203.37, 159.1) * mm, "end": v(206.55, 159.1) * mm});
            skLineSegment(sketch, "E64", {"start": v(206.55, 159.1) * mm, "end": v(206.55, 165.46) * mm});
            skLineSegment(sketch, "E65", {"start": v(206.55, 165.46) * mm, "end": v(211.63, 165.46) * mm});
            skLineSegment(sketch, "E66", {"start": v(211.63, 165.46) * mm, "end": v(211.63, 171.8) * mm});
            skLineSegment(sketch, "E67", {"start": v(211.63, 171.8) * mm, "end": v(206.55, 171.8) * mm});
            skLineSegment(sketch, "E68", {"start": v(206.55, 171.8) * mm, "end": v(206.55, 178.16) * mm});
            skLineSegment(sketch, "E69", {"start": v(206.55, 178.16) * mm, "end": v(211.63, 178.16) * mm});
            skLineSegment(sketch, "E70", {"start": v(211.63, 178.16) * mm, "end": v(211.63, 184.5) * mm});
            skLineSegment(sketch, "E71", {"start": v(211.63, 184.5) * mm, "end": v(206.55, 184.5) * mm});
            skLineSegment(sketch, "E72", {"start": v(206.55, 184.5) * mm, "end": v(206.55, 190.86) * mm});
            skLineSegment(sketch, "E73", {"start": v(206.55, 190.86) * mm, "end": v(211.63, 190.86) * mm});
            skLineSegment(sketch, "E74", {"start": v(211.63, 190.86) * mm, "end": v(211.63, 197.42) * mm});
            skLineSegment(sketch, "E75", {"start": v(211.63, 197.42) * mm, "end": v(206.55, 197.42) * mm});
            skLineSegment(sketch, "E76", {"start": v(206.55, 197.42) * mm, "end": v(206.55, 204) * mm});
            skLineSegment(sketch, "E77.1.0.1", {"start": v(-705.64, 74.3) * mm, "end": v(-699.3, 74.3) * mm});
            skLineSegment(sketch, "E77.1.0.2", {"start": v(-699.3, 79.38) * mm, "end": v(-699.3, 74.3) * mm});
            skLineSegment(sketch, "E77.1.0.3", {"start": v(-699.3, 79.38) * mm, "end": v(-692.94, 79.38) * mm});
            skLineSegment(sketch, "E77.2.0.0", {"start": v(-692.94, 79.38) * mm, "end": v(-692.94, 74.3) * mm});
            skLineSegment(sketch, "E77.2.0.1", {"start": v(-692.94, 74.3) * mm, "end": v(-686.6, 74.3) * mm});
            skLineSegment(sketch, "E77.2.0.2", {"start": v(-686.6, 79.38) * mm, "end": v(-686.6, 74.3) * mm});
            skLineSegment(sketch, "E77.2.0.3", {"start": v(-686.6, 79.38) * mm, "end": v(-680.24, 79.38) * mm});
            skLineSegment(sketch, "E77.3.0.0", {"start": v(-680.24, 79.38) * mm, "end": v(-680.24, 74.3) * mm});
            skLineSegment(sketch, "E77.3.0.1", {"start": v(-680.24, 74.3) * mm, "end": v(-673.9, 74.3) * mm});
            skLineSegment(sketch, "E77.3.0.2", {"start": v(-673.9, 79.38) * mm, "end": v(-673.9, 74.3) * mm});
            skLineSegment(sketch, "E77.3.0.3", {"start": v(-673.9, 79.38) * mm, "end": v(-667.54, 79.38) * mm});
            skLineSegment(sketch, "E77.4.0.0", {"start": v(-667.54, 79.38) * mm, "end": v(-667.54, 74.3) * mm});
            skLineSegment(sketch, "E77.4.0.1", {"start": v(-667.54, 74.3) * mm, "end": v(-661.2, 74.3) * mm});
            skLineSegment(sketch, "E77.4.0.2", {"start": v(-661.2, 79.38) * mm, "end": v(-661.2, 74.3) * mm});
            skLineSegment(sketch, "E77.4.0.3", {"start": v(-661.2, 79.38) * mm, "end": v(-654.84, 79.38) * mm});
            skLineSegment(sketch, "E77.5.0.0", {"start": v(-654.84, 79.38) * mm, "end": v(-654.84, 74.3) * mm});
            skLineSegment(sketch, "E77.5.0.1", {"start": v(-654.84, 74.3) * mm, "end": v(-648.5, 74.3) * mm});
            skLineSegment(sketch, "E77.5.0.2", {"start": v(-648.5, 79.38) * mm, "end": v(-648.5, 74.3) * mm});
            skLineSegment(sketch, "E77.5.0.3", {"start": v(-648.5, 79.38) * mm, "end": v(-642.14, 79.38) * mm});
            skLineSegment(sketch, "E77.6.0.0", {"start": v(-642.14, 79.38) * mm, "end": v(-642.14, 74.3) * mm});
            skLineSegment(sketch, "E77.6.0.1", {"start": v(-642.14, 74.3) * mm, "end": v(-635.8, 74.3) * mm});
            skLineSegment(sketch, "E77.6.0.2", {"start": v(-635.8, 79.38) * mm, "end": v(-635.8, 74.3) * mm});
            skLineSegment(sketch, "E77.6.0.3", {"start": v(-635.8, 79.38) * mm, "end": v(-629.44, 79.38) * mm});
            skLineSegment(sketch, "E77.7.0.0", {"start": v(-629.44, 79.38) * mm, "end": v(-629.44, 74.3) * mm});
            skLineSegment(sketch, "E77.7.0.1", {"start": v(-629.44, 74.3) * mm, "end": v(-623.1, 74.3) * mm});
            skLineSegment(sketch, "E77.7.0.2", {"start": v(-623.1, 79.38) * mm, "end": v(-623.1, 74.3) * mm});
            skLineSegment(sketch, "E77.7.0.3", {"start": v(-623.1, 79.38) * mm, "end": v(-616.74, 79.38) * mm});
            skLineSegment(sketch, "E77.8.0.0", {"start": v(-616.74, 79.38) * mm, "end": v(-616.74, 74.3) * mm});
            skLineSegment(sketch, "E77.8.0.1", {"start": v(-616.74, 74.3) * mm, "end": v(-610.4, 74.3) * mm});
            skLineSegment(sketch, "E77.8.0.2", {"start": v(-610.4, 79.38) * mm, "end": v(-610.4, 74.3) * mm});
            skLineSegment(sketch, "E77.8.0.3", {"start": v(-610.4, 79.38) * mm, "end": v(-604.04, 79.38) * mm});
            skLineSegment(sketch, "E77.9.0.0", {"start": v(-604.04, 79.38) * mm, "end": v(-604.04, 74.3) * mm});
            skLineSegment(sketch, "E77.9.0.1", {"start": v(-604.04, 74.3) * mm, "end": v(-597.7, 74.3) * mm});
            skLineSegment(sketch, "E77.9.0.2", {"start": v(-597.7, 79.38) * mm, "end": v(-597.7, 74.3) * mm});
            skLineSegment(sketch, "E77.9.0.3", {"start": v(-597.7, 79.38) * mm, "end": v(-591.34, 79.38) * mm});
            skLineSegment(sketch, "E77.10.0.0", {"start": v(-591.34, 79.38) * mm, "end": v(-591.34, 74.3) * mm});
            skLineSegment(sketch, "E77.10.0.1", {"start": v(-591.34, 74.3) * mm, "end": v(-585, 74.3) * mm});
            skLineSegment(sketch, "E77.10.0.2", {"start": v(-585, 79.38) * mm, "end": v(-585, 74.3) * mm});
            skLineSegment(sketch, "E77.10.0.3", {"start": v(-585, 79.38) * mm, "end": v(-578.64, 79.38) * mm});
            skLineSegment(sketch, "E77.11.0.0", {"start": v(-578.64, 79.38) * mm, "end": v(-578.64, 74.3) * mm});
            skLineSegment(sketch, "E77.11.0.1", {"start": v(-578.64, 74.3) * mm, "end": v(-572.3, 74.3) * mm});
            skLineSegment(sketch, "E77.11.0.2", {"start": v(-572.3, 79.38) * mm, "end": v(-572.3, 74.3) * mm});
            skLineSegment(sketch, "E77.11.0.3", {"start": v(-572.3, 79.38) * mm, "end": v(-565.94, 79.38) * mm});
            skLineSegment(sketch, "E77.12.0.0", {"start": v(-565.94, 79.38) * mm, "end": v(-565.94, 74.3) * mm});
            skLineSegment(sketch, "E77.12.0.1", {"start": v(-565.94, 74.3) * mm, "end": v(-559.6, 74.3) * mm});
            skLineSegment(sketch, "E77.12.0.2", {"start": v(-559.6, 79.38) * mm, "end": v(-559.6, 74.3) * mm});
            skLineSegment(sketch, "E77.12.0.3", {"start": v(-559.6, 79.38) * mm, "end": v(-553.24, 79.38) * mm});
            skLineSegment(sketch, "E77.13.0.0", {"start": v(-553.24, 79.38) * mm, "end": v(-553.24, 74.3) * mm});
            skLineSegment(sketch, "E77.13.0.1", {"start": v(-553.24, 74.3) * mm, "end": v(-546.9, 74.3) * mm});
            skLineSegment(sketch, "E77.13.0.2", {"start": v(-546.9, 79.38) * mm, "end": v(-546.9, 74.3) * mm});
            skLineSegment(sketch, "E77.13.0.3", {"start": v(-546.9, 79.38) * mm, "end": v(-540.54, 79.38) * mm});
            skLineSegment(sketch, "E77.14.0.0", {"start": v(-540.54, 79.38) * mm, "end": v(-540.54, 74.3) * mm});
            skLineSegment(sketch, "E77.14.0.1", {"start": v(-540.54, 74.3) * mm, "end": v(-534.2, 74.3) * mm});
            skLineSegment(sketch, "E77.14.0.2", {"start": v(-534.2, 79.38) * mm, "end": v(-534.2, 74.3) * mm});
            skLineSegment(sketch, "E77.14.0.3", {"start": v(-534.2, 79.38) * mm, "end": v(-527.84, 79.38) * mm});
            skLineSegment(sketch, "E77.15.0.0", {"start": v(-527.84, 79.38) * mm, "end": v(-527.84, 74.3) * mm});
            skLineSegment(sketch, "E77.15.0.1", {"start": v(-527.84, 74.3) * mm, "end": v(-521.5, 74.3) * mm});
            skLineSegment(sketch, "E77.15.0.2", {"start": v(-521.5, 79.38) * mm, "end": v(-521.5, 74.3) * mm});
            skLineSegment(sketch, "E77.15.0.3", {"start": v(-521.5, 79.38) * mm, "end": v(-515.14, 79.38) * mm});
            skLineSegment(sketch, "E77.16.0.0", {"start": v(-515.14, 79.38) * mm, "end": v(-515.14, 74.3) * mm});
            skLineSegment(sketch, "E77.16.0.1", {"start": v(-515.14, 74.3) * mm, "end": v(-508.8, 74.3) * mm});
            skLineSegment(sketch, "E77.16.0.2", {"start": v(-508.8, 79.38) * mm, "end": v(-508.8, 74.3) * mm});
            skLineSegment(sketch, "E77.16.0.3", {"start": v(-508.8, 79.38) * mm, "end": v(-502.44, 79.38) * mm});
            skLineSegment(sketch, "E77.17.0.0", {"start": v(-502.44, 79.38) * mm, "end": v(-502.44, 74.3) * mm});
            skLineSegment(sketch, "E77.17.0.1", {"start": v(-502.44, 74.3) * mm, "end": v(-496.1, 74.3) * mm});
            skLineSegment(sketch, "E77.17.0.2", {"start": v(-496.1, 79.38) * mm, "end": v(-496.1, 74.3) * mm});
            skLineSegment(sketch, "E77.17.0.3", {"start": v(-496.1, 79.38) * mm, "end": v(-489.74, 79.38) * mm});
            skLineSegment(sketch, "E77.18.0.0", {"start": v(-489.74, 79.38) * mm, "end": v(-489.74, 74.3) * mm});
            skLineSegment(sketch, "E77.18.0.1", {"start": v(-489.74, 74.3) * mm, "end": v(-483.4, 74.3) * mm});
            skLineSegment(sketch, "E77.18.0.2", {"start": v(-483.4, 79.38) * mm, "end": v(-483.4, 74.3) * mm});
            skLineSegment(sketch, "E77.18.0.3", {"start": v(-483.4, 79.38) * mm, "end": v(-477.04, 79.38) * mm});
            skLineSegment(sketch, "E77.19.0.0", {"start": v(-477.04, 79.38) * mm, "end": v(-477.04, 74.3) * mm});
            skLineSegment(sketch, "E77.19.0.1", {"start": v(-477.04, 74.3) * mm, "end": v(-470.7, 74.3) * mm});
            skLineSegment(sketch, "E77.19.0.2", {"start": v(-470.7, 79.38) * mm, "end": v(-470.7, 74.3) * mm});
            skLineSegment(sketch, "E77.19.0.3", {"start": v(-470.7, 79.38) * mm, "end": v(-464.34, 79.38) * mm});
            skLineSegment(sketch, "E77.20.0.0", {"start": v(-464.34, 79.38) * mm, "end": v(-464.34, 74.3) * mm});
            skLineSegment(sketch, "E77.20.0.1", {"start": v(-464.34, 74.3) * mm, "end": v(-458, 74.3) * mm});
            skLineSegment(sketch, "E77.20.0.2", {"start": v(-458, 79.38) * mm, "end": v(-458, 74.3) * mm});
            skLineSegment(sketch, "E77.20.0.3", {"start": v(-458, 79.38) * mm, "end": v(-451.64, 79.38) * mm});
            skLineSegment(sketch, "E77.21.0.0", {"start": v(-451.64, 79.38) * mm, "end": v(-451.64, 74.3) * mm});
            skLineSegment(sketch, "E77.21.0.1", {"start": v(-451.64, 74.3) * mm, "end": v(-445.3, 74.3) * mm});
            skLineSegment(sketch, "E77.21.0.2", {"start": v(-445.3, 79.38) * mm, "end": v(-445.3, 74.3) * mm});
            skLineSegment(sketch, "E77.21.0.3", {"start": v(-445.3, 79.38) * mm, "end": v(-438.94, 79.38) * mm});
            skLineSegment(sketch, "E77.22.0.0", {"start": v(-438.94, 79.38) * mm, "end": v(-438.94, 74.3) * mm});
            skLineSegment(sketch, "E77.22.0.1", {"start": v(-438.94, 74.3) * mm, "end": v(-432.6, 74.3) * mm});
            skLineSegment(sketch, "E77.22.0.2", {"start": v(-432.6, 79.38) * mm, "end": v(-432.6, 74.3) * mm});
            skLineSegment(sketch, "E77.22.0.3", {"start": v(-432.6, 79.38) * mm, "end": v(-426.24, 79.38) * mm});
            skLineSegment(sketch, "E77.23.0.0", {"start": v(-426.24, 79.38) * mm, "end": v(-426.24, 74.3) * mm});
            skLineSegment(sketch, "E77.23.0.1", {"start": v(-426.24, 74.3) * mm, "end": v(-419.9, 74.3) * mm});
            skLineSegment(sketch, "E77.23.0.2", {"start": v(-419.9, 79.38) * mm, "end": v(-419.9, 74.3) * mm});
            skLineSegment(sketch, "E77.23.0.3", {"start": v(-419.9, 79.38) * mm, "end": v(-413.54, 79.38) * mm});
            skLineSegment(sketch, "E77.24.0.0", {"start": v(-413.54, 79.38) * mm, "end": v(-413.54, 74.3) * mm});
            skLineSegment(sketch, "E77.24.0.1", {"start": v(-413.54, 74.3) * mm, "end": v(-407.2, 74.3) * mm});
            skLineSegment(sketch, "E77.24.0.2", {"start": v(-407.2, 79.38) * mm, "end": v(-407.2, 74.3) * mm});
            skLineSegment(sketch, "E77.24.0.3", {"start": v(-407.2, 79.38) * mm, "end": v(-400.84, 79.38) * mm});
            skLineSegment(sketch, "E77.25.0.0", {"start": v(-400.84, 79.38) * mm, "end": v(-400.84, 74.3) * mm});
            skLineSegment(sketch, "E77.25.0.1", {"start": v(-400.84, 74.3) * mm, "end": v(-394.5, 74.3) * mm});
            skLineSegment(sketch, "E77.25.0.2", {"start": v(-394.5, 79.38) * mm, "end": v(-394.5, 74.3) * mm});
            skLineSegment(sketch, "E77.25.0.3", {"start": v(-394.5, 79.38) * mm, "end": v(-388.14, 79.38) * mm});
            skLineSegment(sketch, "E77.26.0.0", {"start": v(-388.14, 79.38) * mm, "end": v(-388.14, 74.3) * mm});
            skLineSegment(sketch, "E77.26.0.1", {"start": v(-388.14, 74.3) * mm, "end": v(-381.8, 74.3) * mm});
            skLineSegment(sketch, "E77.26.0.2", {"start": v(-381.8, 79.38) * mm, "end": v(-381.8, 74.3) * mm});
            skLineSegment(sketch, "E77.26.0.3", {"start": v(-381.8, 79.38) * mm, "end": v(-375.44, 79.38) * mm});
            skLineSegment(sketch, "E77.27.0.0", {"start": v(-375.44, 79.38) * mm, "end": v(-375.44, 74.3) * mm});
            skLineSegment(sketch, "E77.27.0.1", {"start": v(-375.44, 74.3) * mm, "end": v(-369.1, 74.3) * mm});
            skLineSegment(sketch, "E77.27.0.2", {"start": v(-369.1, 79.38) * mm, "end": v(-369.1, 74.3) * mm});
            skLineSegment(sketch, "E77.27.0.3", {"start": v(-369.1, 79.38) * mm, "end": v(-362.74, 79.38) * mm});
            skLineSegment(sketch, "E77.28.0.0", {"start": v(-362.74, 79.38) * mm, "end": v(-362.74, 74.3) * mm});
            skLineSegment(sketch, "E77.28.0.1", {"start": v(-362.74, 74.3) * mm, "end": v(-356.4, 74.3) * mm});
            skLineSegment(sketch, "E77.28.0.2", {"start": v(-356.4, 79.38) * mm, "end": v(-356.4, 74.3) * mm});
            skLineSegment(sketch, "E77.28.0.3", {"start": v(-356.4, 79.38) * mm, "end": v(-350.04, 79.38) * mm});
            skLineSegment(sketch, "E77.29.0.0", {"start": v(-350.04, 79.38) * mm, "end": v(-350.04, 74.3) * mm});
            skLineSegment(sketch, "E77.29.0.1", {"start": v(-350.04, 74.3) * mm, "end": v(-343.7, 74.3) * mm});
            skLineSegment(sketch, "E77.29.0.2", {"start": v(-343.7, 79.38) * mm, "end": v(-343.7, 74.3) * mm});
            skLineSegment(sketch, "E77.29.0.3", {"start": v(-343.7, 79.38) * mm, "end": v(-337.34, 79.38) * mm});
            skLineSegment(sketch, "E77.30.0.0", {"start": v(-337.34, 79.38) * mm, "end": v(-337.34, 74.3) * mm});
            skLineSegment(sketch, "E77.30.0.1", {"start": v(-337.34, 74.3) * mm, "end": v(-331, 74.3) * mm});
            skLineSegment(sketch, "E77.30.0.2", {"start": v(-331, 79.38) * mm, "end": v(-331, 74.3) * mm});
            skLineSegment(sketch, "E77.30.0.3", {"start": v(-331, 79.38) * mm, "end": v(-324.64, 79.38) * mm});
            skLineSegment(sketch, "E77.31.0.0", {"start": v(-324.64, 79.38) * mm, "end": v(-324.64, 74.3) * mm});
            skLineSegment(sketch, "E77.31.0.1", {"start": v(-324.64, 74.3) * mm, "end": v(-318.3, 74.3) * mm});
            skLineSegment(sketch, "E77.31.0.2", {"start": v(-318.3, 79.38) * mm, "end": v(-318.3, 74.3) * mm});
            skLineSegment(sketch, "E77.31.0.3", {"start": v(-318.3, 79.38) * mm, "end": v(-311.94, 79.38) * mm});
            skLineSegment(sketch, "E77.32.0.0", {"start": v(-311.94, 79.38) * mm, "end": v(-311.94, 74.3) * mm});
            skLineSegment(sketch, "E77.32.0.1", {"start": v(-311.94, 74.3) * mm, "end": v(-305.6, 74.3) * mm});
            skLineSegment(sketch, "E77.32.0.2", {"start": v(-305.6, 79.38) * mm, "end": v(-305.6, 74.3) * mm});
            skLineSegment(sketch, "E77.32.0.3", {"start": v(-305.6, 79.38) * mm, "end": v(-299.24, 79.38) * mm});
            skLineSegment(sketch, "E77.33.0.0", {"start": v(-299.24, 79.38) * mm, "end": v(-299.24, 74.3) * mm});
            skLineSegment(sketch, "E77.33.0.1", {"start": v(-299.24, 74.3) * mm, "end": v(-292.9, 74.3) * mm});
            skLineSegment(sketch, "E77.33.0.2", {"start": v(-292.9, 79.38) * mm, "end": v(-292.9, 74.3) * mm});
            skLineSegment(sketch, "E77.33.0.3", {"start": v(-292.9, 79.38) * mm, "end": v(-286.54, 79.38) * mm});
            skLineSegment(sketch, "E77.34.0.0", {"start": v(-286.54, 79.38) * mm, "end": v(-286.54, 74.3) * mm});
            skLineSegment(sketch, "E77.34.0.1", {"start": v(-286.54, 74.3) * mm, "end": v(-280.2, 74.3) * mm});
            skLineSegment(sketch, "E77.34.0.2", {"start": v(-280.2, 79.38) * mm, "end": v(-280.2, 74.3) * mm});
            skLineSegment(sketch, "E77.34.0.3", {"start": v(-280.2, 79.38) * mm, "end": v(-273.84, 79.38) * mm});
            skLineSegment(sketch, "E77.35.0.0", {"start": v(-273.84, 79.38) * mm, "end": v(-273.84, 74.3) * mm});
            skLineSegment(sketch, "E77.35.0.1", {"start": v(-273.84, 74.3) * mm, "end": v(-267.5, 74.3) * mm});
            skLineSegment(sketch, "E77.35.0.2", {"start": v(-267.5, 79.38) * mm, "end": v(-267.5, 74.3) * mm});
            skLineSegment(sketch, "E77.35.0.3", {"start": v(-267.5, 79.38) * mm, "end": v(-261.14, 79.38) * mm});
            skLineSegment(sketch, "E77.36.0.0", {"start": v(-261.14, 79.38) * mm, "end": v(-261.14, 74.3) * mm});
            skLineSegment(sketch, "E77.36.0.1", {"start": v(-261.14, 74.3) * mm, "end": v(-254.8, 74.3) * mm});
            skLineSegment(sketch, "E77.36.0.2", {"start": v(-254.8, 79.38) * mm, "end": v(-254.8, 74.3) * mm});
            skLineSegment(sketch, "E77.36.0.3", {"start": v(-254.8, 79.38) * mm, "end": v(-248.44, 79.38) * mm});
            skLineSegment(sketch, "E77.37.0.0", {"start": v(-248.44, 79.38) * mm, "end": v(-248.44, 74.3) * mm});
            skLineSegment(sketch, "E77.37.0.1", {"start": v(-248.44, 74.3) * mm, "end": v(-242.1, 74.3) * mm});
            skLineSegment(sketch, "E77.37.0.2", {"start": v(-242.1, 79.38) * mm, "end": v(-242.1, 74.3) * mm});
            skLineSegment(sketch, "E77.37.0.3", {"start": v(-242.1, 79.38) * mm, "end": v(-235.74, 79.38) * mm});
            skLineSegment(sketch, "E77.38.0.0", {"start": v(-235.74, 79.38) * mm, "end": v(-235.74, 74.3) * mm});
            skLineSegment(sketch, "E77.38.0.1", {"start": v(-235.74, 74.3) * mm, "end": v(-229.4, 74.3) * mm});
            skLineSegment(sketch, "E77.38.0.2", {"start": v(-229.4, 79.38) * mm, "end": v(-229.4, 74.3) * mm});
            skLineSegment(sketch, "E77.38.0.3", {"start": v(-229.4, 79.38) * mm, "end": v(-223.04, 79.38) * mm});
            skLineSegment(sketch, "E77.39.0.0", {"start": v(-223.04, 79.38) * mm, "end": v(-223.04, 74.3) * mm});
            skLineSegment(sketch, "E77.39.0.1", {"start": v(-223.04, 74.3) * mm, "end": v(-216.7, 74.3) * mm});
            skLineSegment(sketch, "E77.39.0.2", {"start": v(-216.7, 79.38) * mm, "end": v(-216.7, 74.3) * mm});
            skLineSegment(sketch, "E77.39.0.3", {"start": v(-216.7, 79.38) * mm, "end": v(-210.34, 79.38) * mm});
            skLineSegment(sketch, "E77.40.0.0", {"start": v(-210.34, 79.38) * mm, "end": v(-210.34, 74.3) * mm});
            skLineSegment(sketch, "E77.40.0.1", {"start": v(-210.34, 74.3) * mm, "end": v(-204, 74.3) * mm});
            skLineSegment(sketch, "E77.40.0.2", {"start": v(-204, 79.38) * mm, "end": v(-204, 74.3) * mm});
            skLineSegment(sketch, "E77.40.0.3", {"start": v(-204, 79.38) * mm, "end": v(-197.64, 79.38) * mm});
            skLineSegment(sketch, "E77.41.0.0", {"start": v(-197.64, 79.38) * mm, "end": v(-197.64, 74.3) * mm});
            skLineSegment(sketch, "E77.41.0.1", {"start": v(-197.64, 74.3) * mm, "end": v(-191.3, 74.3) * mm});
            skLineSegment(sketch, "E77.41.0.2", {"start": v(-191.3, 79.38) * mm, "end": v(-191.3, 74.3) * mm});
            skLineSegment(sketch, "E77.41.0.3", {"start": v(-191.3, 79.38) * mm, "end": v(-184.94, 79.38) * mm});
            skLineSegment(sketch, "E77.42.0.0", {"start": v(-184.94, 79.38) * mm, "end": v(-184.94, 74.3) * mm});
            skLineSegment(sketch, "E77.42.0.1", {"start": v(-184.94, 74.3) * mm, "end": v(-178.6, 74.3) * mm});
            skLineSegment(sketch, "E77.42.0.2", {"start": v(-178.6, 79.38) * mm, "end": v(-178.6, 74.3) * mm});
            skLineSegment(sketch, "E77.42.0.3", {"start": v(-178.6, 79.38) * mm, "end": v(-172.24, 79.38) * mm});
            skLineSegment(sketch, "E77.43.0.0", {"start": v(-172.24, 79.38) * mm, "end": v(-172.24, 74.3) * mm});
            skLineSegment(sketch, "E77.43.0.1", {"start": v(-172.24, 74.3) * mm, "end": v(-165.9, 74.3) * mm});
            skLineSegment(sketch, "E77.43.0.2", {"start": v(-165.9, 79.38) * mm, "end": v(-165.9, 74.3) * mm});
            skLineSegment(sketch, "E77.43.0.3", {"start": v(-165.9, 79.38) * mm, "end": v(-159.54, 79.38) * mm});
            skLineSegment(sketch, "E77.44.0.0", {"start": v(-159.54, 79.38) * mm, "end": v(-159.54, 74.3) * mm});
            skLineSegment(sketch, "E77.44.0.1", {"start": v(-159.54, 74.3) * mm, "end": v(-153.2, 74.3) * mm});
            skLineSegment(sketch, "E77.44.0.2", {"start": v(-153.2, 79.38) * mm, "end": v(-153.2, 74.3) * mm});
            skLineSegment(sketch, "E77.44.0.3", {"start": v(-153.2, 79.38) * mm, "end": v(-146.84, 79.38) * mm});
            skLineSegment(sketch, "E77.45.0.0", {"start": v(-146.84, 79.38) * mm, "end": v(-146.84, 74.3) * mm});
            skLineSegment(sketch, "E77.45.0.1", {"start": v(-146.84, 74.3) * mm, "end": v(-140.5, 74.3) * mm});
            skLineSegment(sketch, "E77.45.0.2", {"start": v(-140.5, 79.38) * mm, "end": v(-140.5, 74.3) * mm});
            skLineSegment(sketch, "E77.45.0.3", {"start": v(-140.5, 79.38) * mm, "end": v(-134.14, 79.38) * mm});
            skLineSegment(sketch, "E77.46.0.0", {"start": v(-134.14, 79.38) * mm, "end": v(-134.14, 74.3) * mm});
            skLineSegment(sketch, "E77.46.0.1", {"start": v(-134.14, 74.3) * mm, "end": v(-127.8, 74.3) * mm});
            skLineSegment(sketch, "E77.46.0.2", {"start": v(-127.8, 79.38) * mm, "end": v(-127.8, 74.3) * mm});
            skLineSegment(sketch, "E77.46.0.3", {"start": v(-127.8, 79.38) * mm, "end": v(-121.44, 79.38) * mm});
            skLineSegment(sketch, "E77.47.0.0", {"start": v(-121.44, 79.38) * mm, "end": v(-121.44, 74.3) * mm});
            skLineSegment(sketch, "E77.47.0.1", {"start": v(-121.44, 74.3) * mm, "end": v(-115.1, 74.3) * mm});
            skLineSegment(sketch, "E77.47.0.2", {"start": v(-115.1, 79.38) * mm, "end": v(-115.1, 74.3) * mm});
            skLineSegment(sketch, "E77.47.0.3", {"start": v(-115.1, 79.38) * mm, "end": v(-108.74, 79.38) * mm});
            skLineSegment(sketch, "E77.48.0.0", {"start": v(-108.74, 79.38) * mm, "end": v(-108.74, 74.3) * mm});
            skLineSegment(sketch, "E77.48.0.1", {"start": v(-108.74, 74.3) * mm, "end": v(-102.4, 74.3) * mm});
            skLineSegment(sketch, "E77.48.0.2", {"start": v(-102.4, 79.38) * mm, "end": v(-102.4, 74.3) * mm});
            skLineSegment(sketch, "E77.48.0.3", {"start": v(-102.4, 79.38) * mm, "end": v(-96.04, 79.38) * mm});
            skLineSegment(sketch, "E78", {"start": v(206.55, 148.95) * mm, "end": v(211.63, 148.95) * mm});
            skLineSegment(sketch, "E79", {"start": v(211.63, 148.95) * mm, "end": v(211.63, 142.6) * mm});
            skLineSegment(sketch, "E80", {"start": v(206.55, 142.6) * mm, "end": v(211.63, 142.6) * mm});
            skLineSegment(sketch, "E81", {"start": v(206.55, 142.6) * mm, "end": v(206.55, 136.25) * mm});
            skLineSegment(sketch, "E82", {"start": v(211.63, 136.25) * mm, "end": v(206.55, 136.25) * mm});
            skLineSegment(sketch, "E83", {"start": v(211.63, 136.25) * mm, "end": v(211.63, 129.9) * mm});
            skLineSegment(sketch, "E84", {"start": v(206.55, 129.9) * mm, "end": v(211.63, 129.9) * mm});
            skLineSegment(sketch, "E85", {"start": v(206.55, 129.9) * mm, "end": v(206.55, 123.55) * mm});
            skLineSegment(sketch, "E86", {"start": v(211.63, 123.55) * mm, "end": v(206.55, 123.55) * mm});
            skLineSegment(sketch, "E87", {"start": v(211.63, 123.55) * mm, "end": v(211.63, 117.2) * mm});
            skLineSegment(sketch, "E88", {"start": v(206.55, 117.2) * mm, "end": v(211.63, 117.2) * mm});
            skLineSegment(sketch, "E89", {"start": v(206.55, 117.2) * mm, "end": v(206.55, 110.85) * mm});
            skLineSegment(sketch, "E90", {"start": v(-423.37, 148.95) * mm, "end": v(-428.45, 148.95) * mm});
            skLineSegment(sketch, "E91", {"start": v(-423.37, 148.95) * mm, "end": v(-423.37, 142.6) * mm});
            skLineSegment(sketch, "E92", {"start": v(-428.45, 142.6) * mm, "end": v(-423.37, 142.6) * mm});
            skLineSegment(sketch, "E93", {"start": v(-428.45, 142.6) * mm, "end": v(-428.45, 136.25) * mm});
            skLineSegment(sketch, "E94", {"start": v(-423.37, 136.25) * mm, "end": v(-428.45, 136.25) * mm});
            skLineSegment(sketch, "E95", {"start": v(-423.37, 136.25) * mm, "end": v(-423.37, 129.9) * mm});
            skLineSegment(sketch, "E96", {"start": v(-428.45, 129.9) * mm, "end": v(-423.37, 129.9) * mm});
            skLineSegment(sketch, "E97", {"start": v(-428.45, 129.9) * mm, "end": v(-428.45, 123.55) * mm});
            skLineSegment(sketch, "E98", {"start": v(-423.37, 123.55) * mm, "end": v(-428.45, 123.55) * mm});
            skLineSegment(sketch, "E99", {"start": v(-423.37, 123.55) * mm, "end": v(-423.37, 117.2) * mm});
            skLineSegment(sketch, "E100", {"start": v(-428.45, 117.2) * mm, "end": v(-423.37, 117.2) * mm});
            skLineSegment(sketch, "E101", {"start": v(206.55, 159.1) * mm, "end": v(206.55, 148.95) * mm});
            skLineSegment(sketch, "E102", {"start": v(-428.45, 159.1) * mm, "end": v(-428.45, 148.95) * mm});
            skLineSegment(sketch, "E103", {"start": v(-428.45, 117.2) * mm, "end": v(-428.45, 110.85) * mm});
            skLineSegment(sketch, "E104", {"start": v(-428.45, 110.85) * mm, "end": v(-423.37, 110.85) * mm});
            skLineSegment(sketch, "E105", {"start": v(-423.37, 110.85) * mm, "end": v(-423.37, 104.5) * mm});
            skLineSegment(sketch, "E106", {"start": v(-423.37, 104.5) * mm, "end": v(-428.45, 104.5) * mm});
            skLineSegment(sketch, "E107", {"start": v(-428.45, 104.5) * mm, "end": v(-428.45, 98.15) * mm});
            skLineSegment(sketch, "E108", {"start": v(-428.45, 98.15) * mm, "end": v(-423.37, 98.15) * mm});
            skLineSegment(sketch, "E109", {"start": v(-423.37, 98.15) * mm, "end": v(-423.37, 91.8) * mm});
            skLineSegment(sketch, "E110", {"start": v(-423.37, 91.8) * mm, "end": v(-428.45, 91.8) * mm});
            skLineSegment(sketch, "E111", {"start": v(-425.28, 81.64) * mm, "end": v(-425.28, 86.72) * mm});
            skLineSegment(sketch, "E112", {"start": v(-425.28, 86.72) * mm, "end": v(-418.93, 86.72) * mm});
            skLineSegment(sketch, "E113.1.0.0", {"start": v(-418.93, 86.72) * mm, "end": v(-418.93, 81.64) * mm});
            skLineSegment(sketch, "E113.1.0.1", {"start": v(-418.93, 81.64) * mm, "end": v(-412.58, 81.64) * mm});
            skLineSegment(sketch, "E113.1.0.2", {"start": v(-412.58, 81.64) * mm, "end": v(-412.58, 86.72) * mm});
            skLineSegment(sketch, "E113.1.0.3", {"start": v(-412.58, 86.72) * mm, "end": v(-406.23, 86.72) * mm});
            skLineSegment(sketch, "E113.2.0.0", {"start": v(-406.23, 86.72) * mm, "end": v(-406.23, 81.64) * mm});
            skLineSegment(sketch, "E113.2.0.1", {"start": v(-406.23, 81.64) * mm, "end": v(-399.88, 81.64) * mm});
            skLineSegment(sketch, "E113.2.0.2", {"start": v(-399.88, 81.64) * mm, "end": v(-399.88, 86.72) * mm});
            skLineSegment(sketch, "E113.2.0.3", {"start": v(-399.88, 86.72) * mm, "end": v(-393.53, 86.72) * mm});
            skLineSegment(sketch, "E113.3.0.0", {"start": v(-393.53, 86.72) * mm, "end": v(-393.53, 81.64) * mm});
            skLineSegment(sketch, "E113.3.0.1", {"start": v(-393.53, 81.64) * mm, "end": v(-387.18, 81.64) * mm});
            skLineSegment(sketch, "E113.3.0.2", {"start": v(-387.18, 81.64) * mm, "end": v(-387.18, 86.72) * mm});
            skLineSegment(sketch, "E113.3.0.3", {"start": v(-387.18, 86.72) * mm, "end": v(-380.83, 86.72) * mm});
            skLineSegment(sketch, "E113.4.0.0", {"start": v(-380.83, 86.72) * mm, "end": v(-380.83, 81.64) * mm});
            skLineSegment(sketch, "E113.4.0.1", {"start": v(-380.83, 81.64) * mm, "end": v(-374.48, 81.64) * mm});
            skLineSegment(sketch, "E113.4.0.2", {"start": v(-374.48, 81.64) * mm, "end": v(-374.48, 86.72) * mm});
            skLineSegment(sketch, "E113.4.0.3", {"start": v(-374.48, 86.72) * mm, "end": v(-368.13, 86.72) * mm});
            skLineSegment(sketch, "E113.5.0.0", {"start": v(-368.13, 86.72) * mm, "end": v(-368.13, 81.64) * mm});
            skLineSegment(sketch, "E113.5.0.1", {"start": v(-368.13, 81.64) * mm, "end": v(-361.78, 81.64) * mm});
            skLineSegment(sketch, "E113.5.0.2", {"start": v(-361.78, 81.64) * mm, "end": v(-361.78, 86.72) * mm});
            skLineSegment(sketch, "E113.5.0.3", {"start": v(-361.78, 86.72) * mm, "end": v(-355.43, 86.72) * mm});
            skLineSegment(sketch, "E113.6.0.0", {"start": v(-355.43, 86.72) * mm, "end": v(-355.43, 81.64) * mm});
            skLineSegment(sketch, "E113.6.0.1", {"start": v(-355.43, 81.64) * mm, "end": v(-349.08, 81.64) * mm});
            skLineSegment(sketch, "E113.6.0.2", {"start": v(-349.08, 81.64) * mm, "end": v(-349.08, 86.72) * mm});
            skLineSegment(sketch, "E113.6.0.3", {"start": v(-349.08, 86.72) * mm, "end": v(-342.73, 86.72) * mm});
            skLineSegment(sketch, "E113.7.0.0", {"start": v(-342.73, 86.72) * mm, "end": v(-342.73, 81.64) * mm});
            skLineSegment(sketch, "E113.7.0.1", {"start": v(-342.73, 81.64) * mm, "end": v(-336.38, 81.64) * mm});
            skLineSegment(sketch, "E113.7.0.2", {"start": v(-336.38, 81.64) * mm, "end": v(-336.38, 86.72) * mm});
            skLineSegment(sketch, "E113.7.0.3", {"start": v(-336.38, 86.72) * mm, "end": v(-330.03, 86.72) * mm});
            skLineSegment(sketch, "E113.8.0.0", {"start": v(-330.03, 86.72) * mm, "end": v(-330.03, 81.64) * mm});
            skLineSegment(sketch, "E113.8.0.1", {"start": v(-330.03, 81.64) * mm, "end": v(-323.68, 81.64) * mm});
            skLineSegment(sketch, "E113.8.0.2", {"start": v(-323.68, 81.64) * mm, "end": v(-323.68, 86.72) * mm});
            skLineSegment(sketch, "E113.8.0.3", {"start": v(-323.68, 86.72) * mm, "end": v(-317.33, 86.72) * mm});
            skLineSegment(sketch, "E113.9.0.0", {"start": v(-317.33, 86.72) * mm, "end": v(-317.33, 81.64) * mm});
            skLineSegment(sketch, "E113.9.0.1", {"start": v(-317.33, 81.64) * mm, "end": v(-310.98, 81.64) * mm});
            skLineSegment(sketch, "E113.9.0.2", {"start": v(-310.98, 81.64) * mm, "end": v(-310.98, 86.72) * mm});
            skLineSegment(sketch, "E113.9.0.3", {"start": v(-310.98, 86.72) * mm, "end": v(-304.63, 86.72) * mm});
            skLineSegment(sketch, "E113.10.0.0", {"start": v(-304.63, 86.72) * mm, "end": v(-304.63, 81.64) * mm});
            skLineSegment(sketch, "E113.10.0.1", {"start": v(-304.63, 81.64) * mm, "end": v(-298.28, 81.64) * mm});
            skLineSegment(sketch, "E113.10.0.2", {"start": v(-298.28, 81.64) * mm, "end": v(-298.28, 86.72) * mm});
            skLineSegment(sketch, "E113.10.0.3", {"start": v(-298.28, 86.72) * mm, "end": v(-291.93, 86.72) * mm});
            skLineSegment(sketch, "E113.11.0.0", {"start": v(-291.93, 86.72) * mm, "end": v(-291.93, 81.64) * mm});
            skLineSegment(sketch, "E113.11.0.1", {"start": v(-291.93, 81.64) * mm, "end": v(-285.58, 81.64) * mm});
            skLineSegment(sketch, "E113.11.0.2", {"start": v(-285.58, 81.64) * mm, "end": v(-285.58, 86.72) * mm});
            skLineSegment(sketch, "E113.11.0.3", {"start": v(-285.58, 86.72) * mm, "end": v(-279.23, 86.72) * mm});
            skLineSegment(sketch, "E113.12.0.0", {"start": v(-279.23, 86.72) * mm, "end": v(-279.23, 81.64) * mm});
            skLineSegment(sketch, "E113.12.0.1", {"start": v(-279.23, 81.64) * mm, "end": v(-272.88, 81.64) * mm});
            skLineSegment(sketch, "E113.12.0.2", {"start": v(-272.88, 81.64) * mm, "end": v(-272.88, 86.72) * mm});
            skLineSegment(sketch, "E113.12.0.3", {"start": v(-272.88, 86.72) * mm, "end": v(-266.53, 86.72) * mm});
            skLineSegment(sketch, "E113.13.0.0", {"start": v(-266.53, 86.72) * mm, "end": v(-266.53, 81.64) * mm});
            skLineSegment(sketch, "E113.13.0.1", {"start": v(-266.53, 81.64) * mm, "end": v(-260.18, 81.64) * mm});
            skLineSegment(sketch, "E113.13.0.2", {"start": v(-260.18, 81.64) * mm, "end": v(-260.18, 86.72) * mm});
            skLineSegment(sketch, "E113.13.0.3", {"start": v(-260.18, 86.72) * mm, "end": v(-253.83, 86.72) * mm});
            skLineSegment(sketch, "E113.14.0.0", {"start": v(-253.83, 86.72) * mm, "end": v(-253.83, 81.64) * mm});
            skLineSegment(sketch, "E113.14.0.1", {"start": v(-253.83, 81.64) * mm, "end": v(-247.48, 81.64) * mm});
            skLineSegment(sketch, "E113.14.0.2", {"start": v(-247.48, 81.64) * mm, "end": v(-247.48, 86.72) * mm});
            skLineSegment(sketch, "E113.14.0.3", {"start": v(-247.48, 86.72) * mm, "end": v(-241.13, 86.72) * mm});
            skLineSegment(sketch, "E113.15.0.0", {"start": v(-241.13, 86.72) * mm, "end": v(-241.13, 81.64) * mm});
            skLineSegment(sketch, "E113.15.0.1", {"start": v(-241.13, 81.64) * mm, "end": v(-234.78, 81.64) * mm});
            skLineSegment(sketch, "E113.15.0.2", {"start": v(-234.78, 81.64) * mm, "end": v(-234.78, 86.72) * mm});
            skLineSegment(sketch, "E113.15.0.3", {"start": v(-234.78, 86.72) * mm, "end": v(-228.43, 86.72) * mm});
            skLineSegment(sketch, "E113.16.0.0", {"start": v(-228.43, 86.72) * mm, "end": v(-228.43, 81.64) * mm});
            skLineSegment(sketch, "E113.16.0.1", {"start": v(-228.43, 81.64) * mm, "end": v(-222.08, 81.64) * mm});
            skLineSegment(sketch, "E113.16.0.2", {"start": v(-222.08, 81.64) * mm, "end": v(-222.08, 86.72) * mm});
            skLineSegment(sketch, "E113.16.0.3", {"start": v(-222.08, 86.72) * mm, "end": v(-215.73, 86.72) * mm});
            skLineSegment(sketch, "E113.17.0.0", {"start": v(-215.73, 86.72) * mm, "end": v(-215.73, 81.64) * mm});
            skLineSegment(sketch, "E113.17.0.1", {"start": v(-215.73, 81.64) * mm, "end": v(-209.38, 81.64) * mm});
            skLineSegment(sketch, "E113.17.0.2", {"start": v(-209.38, 81.64) * mm, "end": v(-209.38, 86.72) * mm});
            skLineSegment(sketch, "E113.17.0.3", {"start": v(-209.38, 86.72) * mm, "end": v(-203.03, 86.72) * mm});
            skLineSegment(sketch, "E113.18.0.0", {"start": v(-203.03, 86.72) * mm, "end": v(-203.03, 81.64) * mm});
            skLineSegment(sketch, "E113.18.0.1", {"start": v(-203.03, 81.64) * mm, "end": v(-196.68, 81.64) * mm});
            skLineSegment(sketch, "E113.18.0.2", {"start": v(-196.68, 81.64) * mm, "end": v(-196.68, 86.72) * mm});
            skLineSegment(sketch, "E113.18.0.3", {"start": v(-196.68, 86.72) * mm, "end": v(-190.33, 86.72) * mm});
            skLineSegment(sketch, "E113.19.0.0", {"start": v(-190.33, 86.72) * mm, "end": v(-190.33, 81.64) * mm});
            skLineSegment(sketch, "E113.19.0.1", {"start": v(-190.33, 81.64) * mm, "end": v(-183.98, 81.64) * mm});
            skLineSegment(sketch, "E113.19.0.2", {"start": v(-183.98, 81.64) * mm, "end": v(-183.98, 86.72) * mm});
            skLineSegment(sketch, "E113.19.0.3", {"start": v(-183.98, 86.72) * mm, "end": v(-177.63, 86.72) * mm});
            skLineSegment(sketch, "E113.20.0.0", {"start": v(-177.63, 86.72) * mm, "end": v(-177.63, 81.64) * mm});
            skLineSegment(sketch, "E113.20.0.1", {"start": v(-177.63, 81.64) * mm, "end": v(-171.28, 81.64) * mm});
            skLineSegment(sketch, "E113.20.0.2", {"start": v(-171.28, 81.64) * mm, "end": v(-171.28, 86.72) * mm});
            skLineSegment(sketch, "E113.20.0.3", {"start": v(-171.28, 86.72) * mm, "end": v(-164.93, 86.72) * mm});
            skLineSegment(sketch, "E113.21.0.0", {"start": v(-164.93, 86.72) * mm, "end": v(-164.93, 81.64) * mm});
            skLineSegment(sketch, "E113.21.0.1", {"start": v(-164.93, 81.64) * mm, "end": v(-158.58, 81.64) * mm});
            skLineSegment(sketch, "E113.21.0.2", {"start": v(-158.58, 81.64) * mm, "end": v(-158.58, 86.72) * mm});
            skLineSegment(sketch, "E113.21.0.3", {"start": v(-158.58, 86.72) * mm, "end": v(-152.23, 86.72) * mm});
            skLineSegment(sketch, "E113.22.0.0", {"start": v(-152.23, 86.72) * mm, "end": v(-152.23, 81.64) * mm});
            skLineSegment(sketch, "E113.22.0.1", {"start": v(-152.23, 81.64) * mm, "end": v(-145.88, 81.64) * mm});
            skLineSegment(sketch, "E113.22.0.2", {"start": v(-145.88, 81.64) * mm, "end": v(-145.88, 86.72) * mm});
            skLineSegment(sketch, "E113.22.0.3", {"start": v(-145.88, 86.72) * mm, "end": v(-139.53, 86.72) * mm});
            skLineSegment(sketch, "E113.23.0.0", {"start": v(-139.53, 86.72) * mm, "end": v(-139.53, 81.64) * mm});
            skLineSegment(sketch, "E113.23.0.1", {"start": v(-139.53, 81.64) * mm, "end": v(-133.18, 81.64) * mm});
            skLineSegment(sketch, "E113.23.0.2", {"start": v(-133.18, 81.64) * mm, "end": v(-133.18, 86.72) * mm});
            skLineSegment(sketch, "E113.23.0.3", {"start": v(-133.18, 86.72) * mm, "end": v(-126.83, 86.72) * mm});
            skLineSegment(sketch, "E113.24.0.0", {"start": v(-126.83, 86.72) * mm, "end": v(-126.83, 81.64) * mm});
            skLineSegment(sketch, "E113.24.0.1", {"start": v(-126.83, 81.64) * mm, "end": v(-120.48, 81.64) * mm});
            skLineSegment(sketch, "E113.24.0.2", {"start": v(-120.48, 81.64) * mm, "end": v(-120.48, 86.72) * mm});
            skLineSegment(sketch, "E113.24.0.3", {"start": v(-120.48, 86.72) * mm, "end": v(-114.13, 86.72) * mm});
            skLineSegment(sketch, "E113.25.0.0", {"start": v(-114.13, 86.72) * mm, "end": v(-114.13, 81.64) * mm});
            skLineSegment(sketch, "E113.25.0.1", {"start": v(-114.13, 81.64) * mm, "end": v(-107.78, 81.64) * mm});
            skLineSegment(sketch, "E113.25.0.2", {"start": v(-107.78, 81.64) * mm, "end": v(-107.78, 86.72) * mm});
            skLineSegment(sketch, "E113.25.0.3", {"start": v(-107.78, 86.72) * mm, "end": v(-101.43, 86.72) * mm});
            skLineSegment(sketch, "E113.26.0.0", {"start": v(-101.43, 86.72) * mm, "end": v(-101.43, 81.64) * mm});
            skLineSegment(sketch, "E113.26.0.1", {"start": v(-101.43, 81.64) * mm, "end": v(-95.08, 81.64) * mm});
            skLineSegment(sketch, "E113.26.0.2", {"start": v(-95.08, 81.64) * mm, "end": v(-95.08, 86.72) * mm});
            skLineSegment(sketch, "E113.26.0.3", {"start": v(-95.08, 86.72) * mm, "end": v(-88.73, 86.72) * mm});
            skLineSegment(sketch, "E113.27.0.0", {"start": v(-88.73, 86.72) * mm, "end": v(-88.73, 81.64) * mm});
            skLineSegment(sketch, "E113.27.0.1", {"start": v(-88.73, 81.64) * mm, "end": v(-82.38, 81.64) * mm});
            skLineSegment(sketch, "E113.27.0.2", {"start": v(-82.38, 81.64) * mm, "end": v(-82.38, 86.72) * mm});
            skLineSegment(sketch, "E113.27.0.3", {"start": v(-82.38, 86.72) * mm, "end": v(-76.03, 86.72) * mm});
            skLineSegment(sketch, "E113.28.0.0", {"start": v(-76.03, 86.72) * mm, "end": v(-76.03, 81.64) * mm});
            skLineSegment(sketch, "E113.28.0.1", {"start": v(-76.03, 81.64) * mm, "end": v(-69.68, 81.64) * mm});
            skLineSegment(sketch, "E113.28.0.2", {"start": v(-69.68, 81.64) * mm, "end": v(-69.68, 86.72) * mm});
            skLineSegment(sketch, "E113.28.0.3", {"start": v(-69.68, 86.72) * mm, "end": v(-63.33, 86.72) * mm});
            skLineSegment(sketch, "E113.29.0.0", {"start": v(-63.33, 86.72) * mm, "end": v(-63.33, 81.64) * mm});
            skLineSegment(sketch, "E113.29.0.1", {"start": v(-63.33, 81.64) * mm, "end": v(-56.98, 81.64) * mm});
            skLineSegment(sketch, "E113.29.0.2", {"start": v(-56.98, 81.64) * mm, "end": v(-56.98, 86.72) * mm});
            skLineSegment(sketch, "E113.29.0.3", {"start": v(-56.98, 86.72) * mm, "end": v(-50.63, 86.72) * mm});
            skLineSegment(sketch, "E113.30.0.0", {"start": v(-50.63, 86.72) * mm, "end": v(-50.63, 81.64) * mm});
            skLineSegment(sketch, "E113.30.0.1", {"start": v(-50.63, 81.64) * mm, "end": v(-44.28, 81.64) * mm});
            skLineSegment(sketch, "E113.30.0.2", {"start": v(-44.28, 81.64) * mm, "end": v(-44.28, 86.72) * mm});
            skLineSegment(sketch, "E113.30.0.3", {"start": v(-44.28, 86.72) * mm, "end": v(-37.93, 86.72) * mm});
            skLineSegment(sketch, "E113.31.0.0", {"start": v(-37.93, 86.72) * mm, "end": v(-37.93, 81.64) * mm});
            skLineSegment(sketch, "E113.31.0.1", {"start": v(-37.93, 81.64) * mm, "end": v(-31.58, 81.64) * mm});
            skLineSegment(sketch, "E113.31.0.2", {"start": v(-31.58, 81.64) * mm, "end": v(-31.58, 86.72) * mm});
            skLineSegment(sketch, "E113.31.0.3", {"start": v(-31.58, 86.72) * mm, "end": v(-25.23, 86.72) * mm});
            skLineSegment(sketch, "E113.32.0.0", {"start": v(-25.23, 86.72) * mm, "end": v(-25.23, 81.64) * mm});
            skLineSegment(sketch, "E113.32.0.1", {"start": v(-25.23, 81.64) * mm, "end": v(-18.88, 81.64) * mm});
            skLineSegment(sketch, "E113.32.0.2", {"start": v(-18.88, 81.64) * mm, "end": v(-18.88, 86.72) * mm});
            skLineSegment(sketch, "E113.32.0.3", {"start": v(-18.88, 86.72) * mm, "end": v(-12.53, 86.72) * mm});
            skLineSegment(sketch, "E113.33.0.0", {"start": v(-12.53, 86.72) * mm, "end": v(-12.53, 81.64) * mm});
            skLineSegment(sketch, "E113.33.0.1", {"start": v(-12.53, 81.64) * mm, "end": v(-6.18, 81.64) * mm});
            skLineSegment(sketch, "E113.33.0.2", {"start": v(-6.18, 81.64) * mm, "end": v(-6.18, 86.72) * mm});
            skLineSegment(sketch, "E113.33.0.3", {"start": v(-6.18, 86.72) * mm, "end": v(0.17, 86.72) * mm});
            skLineSegment(sketch, "E113.34.0.0", {"start": v(0.17, 86.72) * mm, "end": v(0.17, 81.64) * mm});
            skLineSegment(sketch, "E113.34.0.1", {"start": v(0.17, 81.64) * mm, "end": v(6.52, 81.64) * mm});
            skLineSegment(sketch, "E113.34.0.2", {"start": v(6.52, 81.64) * mm, "end": v(6.52, 86.72) * mm});
            skLineSegment(sketch, "E113.34.0.3", {"start": v(6.52, 86.72) * mm, "end": v(12.87, 86.72) * mm});
            skLineSegment(sketch, "E113.35.0.0", {"start": v(12.87, 86.72) * mm, "end": v(12.87, 81.64) * mm});
            skLineSegment(sketch, "E113.35.0.1", {"start": v(12.87, 81.64) * mm, "end": v(19.22, 81.64) * mm});
            skLineSegment(sketch, "E113.35.0.2", {"start": v(19.22, 81.64) * mm, "end": v(19.22, 86.72) * mm});
            skLineSegment(sketch, "E113.35.0.3", {"start": v(19.22, 86.72) * mm, "end": v(25.57, 86.72) * mm});
            skLineSegment(sketch, "E113.36.0.0", {"start": v(25.57, 86.72) * mm, "end": v(25.57, 81.64) * mm});
            skLineSegment(sketch, "E113.36.0.1", {"start": v(25.57, 81.64) * mm, "end": v(31.92, 81.64) * mm});
            skLineSegment(sketch, "E113.36.0.2", {"start": v(31.92, 81.64) * mm, "end": v(31.92, 86.72) * mm});
            skLineSegment(sketch, "E113.36.0.3", {"start": v(31.92, 86.72) * mm, "end": v(38.27, 86.72) * mm});
            skLineSegment(sketch, "E113.37.0.0", {"start": v(38.27, 86.72) * mm, "end": v(38.27, 81.64) * mm});
            skLineSegment(sketch, "E113.37.0.1", {"start": v(38.27, 81.64) * mm, "end": v(44.62, 81.64) * mm});
            skLineSegment(sketch, "E113.37.0.2", {"start": v(44.62, 81.64) * mm, "end": v(44.62, 86.72) * mm});
            skLineSegment(sketch, "E113.37.0.3", {"start": v(44.62, 86.72) * mm, "end": v(50.97, 86.72) * mm});
            skLineSegment(sketch, "E113.38.0.0", {"start": v(50.97, 86.72) * mm, "end": v(50.97, 81.64) * mm});
            skLineSegment(sketch, "E113.38.0.1", {"start": v(50.97, 81.64) * mm, "end": v(57.32, 81.64) * mm});
            skLineSegment(sketch, "E113.38.0.2", {"start": v(57.32, 81.64) * mm, "end": v(57.32, 86.72) * mm});
            skLineSegment(sketch, "E113.38.0.3", {"start": v(57.32, 86.72) * mm, "end": v(63.67, 86.72) * mm});
            skLineSegment(sketch, "E113.39.0.0", {"start": v(63.67, 86.72) * mm, "end": v(63.67, 81.64) * mm});
            skLineSegment(sketch, "E113.39.0.1", {"start": v(63.67, 81.64) * mm, "end": v(70.02, 81.64) * mm});
            skLineSegment(sketch, "E113.39.0.2", {"start": v(70.02, 81.64) * mm, "end": v(70.02, 86.72) * mm});
            skLineSegment(sketch, "E113.39.0.3", {"start": v(70.02, 86.72) * mm, "end": v(76.37, 86.72) * mm});
            skLineSegment(sketch, "E113.40.0.0", {"start": v(76.37, 86.72) * mm, "end": v(76.37, 81.64) * mm});
            skLineSegment(sketch, "E113.40.0.1", {"start": v(76.37, 81.64) * mm, "end": v(82.72, 81.64) * mm});
            skLineSegment(sketch, "E113.40.0.2", {"start": v(82.72, 81.64) * mm, "end": v(82.72, 86.72) * mm});
            skLineSegment(sketch, "E113.40.0.3", {"start": v(82.72, 86.72) * mm, "end": v(89.07, 86.72) * mm});
            skLineSegment(sketch, "E113.41.0.0", {"start": v(89.07, 86.72) * mm, "end": v(89.07, 81.64) * mm});
            skLineSegment(sketch, "E113.41.0.1", {"start": v(89.07, 81.64) * mm, "end": v(95.42, 81.64) * mm});
            skLineSegment(sketch, "E113.41.0.2", {"start": v(95.42, 81.64) * mm, "end": v(95.42, 86.72) * mm});
            skLineSegment(sketch, "E113.41.0.3", {"start": v(95.42, 86.72) * mm, "end": v(101.77, 86.72) * mm});
            skLineSegment(sketch, "E113.42.0.0", {"start": v(101.77, 86.72) * mm, "end": v(101.77, 81.64) * mm});
            skLineSegment(sketch, "E113.42.0.1", {"start": v(101.77, 81.64) * mm, "end": v(108.12, 81.64) * mm});
            skLineSegment(sketch, "E113.42.0.2", {"start": v(108.12, 81.64) * mm, "end": v(108.12, 86.72) * mm});
            skLineSegment(sketch, "E113.42.0.3", {"start": v(108.12, 86.72) * mm, "end": v(114.47, 86.72) * mm});
            skLineSegment(sketch, "E113.43.0.0", {"start": v(114.47, 86.72) * mm, "end": v(114.47, 81.64) * mm});
            skLineSegment(sketch, "E113.43.0.1", {"start": v(114.47, 81.64) * mm, "end": v(120.82, 81.64) * mm});
            skLineSegment(sketch, "E113.43.0.2", {"start": v(120.82, 81.64) * mm, "end": v(120.82, 86.72) * mm});
            skLineSegment(sketch, "E113.43.0.3", {"start": v(120.82, 86.72) * mm, "end": v(127.17, 86.72) * mm});
            skLineSegment(sketch, "E113.44.0.0", {"start": v(127.17, 86.72) * mm, "end": v(127.17, 81.64) * mm});
            skLineSegment(sketch, "E113.44.0.1", {"start": v(127.17, 81.64) * mm, "end": v(133.52, 81.64) * mm});
            skLineSegment(sketch, "E113.44.0.2", {"start": v(133.52, 81.64) * mm, "end": v(133.52, 86.72) * mm});
            skLineSegment(sketch, "E113.44.0.3", {"start": v(133.52, 86.72) * mm, "end": v(139.87, 86.72) * mm});
            skLineSegment(sketch, "E113.45.0.0", {"start": v(139.87, 86.72) * mm, "end": v(139.87, 81.64) * mm});
            skLineSegment(sketch, "E113.45.0.1", {"start": v(139.87, 81.64) * mm, "end": v(146.22, 81.64) * mm});
            skLineSegment(sketch, "E113.45.0.2", {"start": v(146.22, 81.64) * mm, "end": v(146.22, 86.72) * mm});
            skLineSegment(sketch, "E113.45.0.3", {"start": v(146.22, 86.72) * mm, "end": v(152.57, 86.72) * mm});
            skLineSegment(sketch, "E113.46.0.0", {"start": v(152.57, 86.72) * mm, "end": v(152.57, 81.64) * mm});
            skLineSegment(sketch, "E113.46.0.1", {"start": v(152.57, 81.64) * mm, "end": v(158.92, 81.64) * mm});
            skLineSegment(sketch, "E113.46.0.2", {"start": v(158.92, 81.64) * mm, "end": v(158.92, 86.72) * mm});
            skLineSegment(sketch, "E113.46.0.3", {"start": v(158.92, 86.72) * mm, "end": v(165.27, 86.72) * mm});
            skLineSegment(sketch, "E113.47.0.0", {"start": v(165.27, 86.72) * mm, "end": v(165.27, 81.64) * mm});
            skLineSegment(sketch, "E113.47.0.1", {"start": v(165.27, 81.64) * mm, "end": v(171.62, 81.64) * mm});
            skLineSegment(sketch, "E113.47.0.2", {"start": v(171.62, 81.64) * mm, "end": v(171.62, 86.72) * mm});
            skLineSegment(sketch, "E113.47.0.3", {"start": v(171.62, 86.72) * mm, "end": v(177.97, 86.72) * mm});
            skLineSegment(sketch, "E113.48.0.0", {"start": v(177.97, 86.72) * mm, "end": v(177.97, 81.64) * mm});
            skLineSegment(sketch, "E113.48.0.1", {"start": v(177.97, 81.64) * mm, "end": v(184.32, 81.64) * mm});
            skLineSegment(sketch, "E113.48.0.2", {"start": v(184.32, 81.64) * mm, "end": v(184.32, 86.72) * mm});
            skLineSegment(sketch, "E113.48.0.3", {"start": v(184.32, 86.72) * mm, "end": v(190.67, 86.72) * mm});
            skLineSegment(sketch, "E114", {"start": v(190.67, 86.72) * mm, "end": v(190.67, 81.64) * mm});
            skLineSegment(sketch, "E115", {"start": v(190.67, 81.64) * mm, "end": v(197.02, 81.64) * mm});
            skLineSegment(sketch, "E116", {"start": v(197.02, 81.64) * mm, "end": v(197.02, 86.72) * mm});
            skLineSegment(sketch, "E117", {"start": v(-86.62, 79.65) * mm, "end": v(-86.62, 86) * mm});
            skLineSegment(sketch, "E118", {"start": v(-86.62, 86) * mm, "end": v(-81.54, 86) * mm});
            skLineSegment(sketch, "E119", {"start": v(-81.54, 86) * mm, "end": v(-81.54, 92.35) * mm});
            skLineSegment(sketch, "E120", {"start": v(-81.54, 92.35) * mm, "end": v(-86.62, 92.35) * mm});
            skLineSegment(sketch, "E121", {"start": v(-86.62, 92.35) * mm, "end": v(-86.62, 98.7) * mm});
            skLineSegment(sketch, "E122", {"start": v(-86.62, 98.7) * mm, "end": v(-81.54, 98.7) * mm});
            skLineSegment(sketch, "E123", {"start": v(-81.54, 98.7) * mm, "end": v(-81.54, 105.05) * mm});
            skLineSegment(sketch, "E124", {"start": v(-81.54, 105.05) * mm, "end": v(-86.62, 105.05) * mm});
            skLineSegment(sketch, "E125", {"start": v(-86.62, 105.05) * mm, "end": v(-86.62, 111.4) * mm});
            skLineSegment(sketch, "E126", {"start": v(-86.62, 111.4) * mm, "end": v(-81.54, 111.4) * mm});
            skLineSegment(sketch, "E127", {"start": v(-81.54, 62.95) * mm, "end": v(-81.54, 111.4) * mm});
            skLineSegment(sketch, "E128", {"start": v(-81.54, 62.95) * mm, "end": v(-86.62, 62.95) * mm});
            skLineSegment(sketch, "E129", {"start": v(-86.62, 62.95) * mm, "end": v(-86.62, 111.4) * mm});
            skLineSegment(sketch, "E130", {"start": v(-432.26, 259.44) * mm, "end": v(-432.26, -197.76) * mm});
            skLineSegment(sketch, "E131", {"start": v(206.55, 110.85) * mm, "end": v(211.63, 110.85) * mm});
            skLineSegment(sketch, "E132", {"start": v(211.63, 110.85) * mm, "end": v(211.63, 104.5) * mm});
            skLineSegment(sketch, "E133", {"start": v(211.63, 104.5) * mm, "end": v(206.55, 104.5) * mm});
            skLineSegment(sketch, "E134", {"start": v(206.55, 104.5) * mm, "end": v(206.55, 98.15) * mm});
            skLineSegment(sketch, "E135", {"start": v(206.55, 98.15) * mm, "end": v(211.63, 98.15) * mm});
            skLineSegment(sketch, "E136", {"start": v(211.63, 98.15) * mm, "end": v(211.63, 91.8) * mm});
            skLineSegment(sketch, "E137", {"start": v(211.63, 91.8) * mm, "end": v(206.55, 91.8) * mm});
            skLineSegment(sketch, "E138", {"start": v(206.55, 91.8) * mm, "end": v(206.55, 81.64) * mm});
            skLineSegment(sketch, "E139", {"start": v(206.55, 81.64) * mm, "end": v(203.37, 81.64) * mm});
            skLineSegment(sketch, "E140", {"start": v(203.37, 81.64) * mm, "end": v(203.37, 86.72) * mm});
            skLineSegment(sketch, "E141", {"start": v(203.37, 86.72) * mm, "end": v(197.02, 86.72) * mm});
            skLineSegment(sketch, "E142", {"start": v(-428.45, 91.8) * mm, "end": v(-428.45, 81.64) * mm});
            skLineSegment(sketch, "E143", {"start": v(-428.45, 81.64) * mm, "end": v(-425.28, 81.64) * mm});
            skSolve(sketch);
        }
        {
            var Q0;
            Q0=makeQuery(id+"F0.imprint","IMPRINT",FACE,{"disambiguationData":[TD([[makeQuery(id+"F0.imprint","IMPRINT",EDGE,{"derivedFrom":sQuery(id+"F0.wireOp",EDGE,"E1.bottom")}),-1.0]])]});
            extrude(context, id + "F1", {"entities" : qUnion([Q0]), "depth" : 5.08 * mm});
        }
        {
            var Q0;
            Q0=makeQuery(id+"F1.opExtrude","SWEPT_BODY",BODY,{"disambiguationData":[OSD([sQuery(id+"F0.wireOp",EDGE,"E1.bottom"),sQuery(id+"F0.wireOp",EDGE,"E1.left"),sQuery(id+"F0.wireOp",EDGE,"E1.right"),sQuery(id+"F0.wireOp",EDGE,"E2"),sQuery(id+"F0.wireOp",EDGE,"E3.1.0.0"),sQuery(id+"F0.wireOp",EDGE,"E3.1.0.1"),sQuery(id+"F0.wireOp",EDGE,"E3.1.0.2"),sQuery(id+"F0.wireOp",EDGE,"E3.1.0.3"),sQuery(id+"F0.wireOp",EDGE,"E3.2.0.0"),sQuery(id+"F0.wireOp",EDGE,"E3.2.0.1"),sQuery(id+"F0.wireOp",EDGE,"E3.2.0.2"),sQuery(id+"F0.wireOp",EDGE,"E3.2.0.3"),sQuery(id+"F0.wireOp",EDGE,"E3.3.0.0"),sQuery(id+"F0.wireOp",EDGE,"E3.3.0.1"),sQuery(id+"F0.wireOp",EDGE,"E3.3.0.2"),sQuery(id+"F0.wireOp",EDGE,"E3.3.0.3"),sQuery(id+"F0.wireOp",EDGE,"E3.4.0.0"),sQuery(id+"F0.wireOp",EDGE,"E3.4.0.1"),sQuery(id+"F0.wireOp",EDGE,"E3.4.0.2"),sQuery(id+"F0.wireOp",EDGE,"E3.4.0.3"),sQuery(id+"F0.wireOp",EDGE,"E3.5.0.0"),sQuery(id+"F0.wireOp",EDGE,"E3.5.0.1"),sQuery(id+"F0.wireOp",EDGE,"E3.5.0.2"),sQuery(id+"F0.wireOp",EDGE,"E3.5.0.3"),sQuery(id+"F0.wireOp",EDGE,"E3.6.0.0"),sQuery(id+"F0.wireOp",EDGE,"E3.6.0.1"),sQuery(id+"F0.wireOp",EDGE,"E3.6.0.2"),sQuery(id+"F0.wireOp",EDGE,"E3.6.0.3"),sQuery(id+"F0.wireOp",EDGE,"E3.7.0.0"),sQuery(id+"F0.wireOp",EDGE,"E3.7.0.1"),sQuery(id+"F0.wireOp",EDGE,"E3.7.0.2"),sQuery(id+"F0.wireOp",EDGE,"E3.7.0.3"),sQuery(id+"F0.wireOp",EDGE,"E3.8.0.0"),sQuery(id+"F0.wireOp",EDGE,"E3.8.0.1"),sQuery(id+"F0.wireOp",EDGE,"E3.8.0.2"),sQuery(id+"F0.wireOp",EDGE,"E3.8.0.3"),sQuery(id+"F0.wireOp",EDGE,"E3.9.0.0"),sQuery(id+"F0.wireOp",EDGE,"E3.9.0.1"),sQuery(id+"F0.wireOp",EDGE,"E3.9.0.2"),sQuery(id+"F0.wireOp",EDGE,"E3.9.0.3"),sQuery(id+"F0.wireOp",EDGE,"E3.10.0.0"),sQuery(id+"F0.wireOp",EDGE,"E3.10.0.1"),sQuery(id+"F0.wireOp",EDGE,"E3.10.0.2"),sQuery(id+"F0.wireOp",EDGE,"E3.10.0.3"),sQuery(id+"F0.wireOp",EDGE,"E3.11.0.0"),sQuery(id+"F0.wireOp",EDGE,"E3.11.0.1"),sQuery(id+"F0.wireOp",EDGE,"E3.11.0.2"),sQuery(id+"F0.wireOp",EDGE,"E3.11.0.3"),sQuery(id+"F0.wireOp",EDGE,"E3.12.0.0"),sQuery(id+"F0.wireOp",EDGE,"E3.12.0.1"),sQuery(id+"F0.wireOp",EDGE,"E3.12.0.2"),sQuery(id+"F0.wireOp",EDGE,"E3.12.0.3"),sQuery(id+"F0.wireOp",EDGE,"E3.13.0.0"),sQuery(id+"F0.wireOp",EDGE,"E3.13.0.1"),sQuery(id+"F0.wireOp",EDGE,"E3.13.0.2"),sQuery(id+"F0.wireOp",EDGE,"E3.13.0.3"),sQuery(id+"F0.wireOp",EDGE,"E3.14.0.0"),sQuery(id+"F0.wireOp",EDGE,"E3.14.0.1"),sQuery(id+"F0.wireOp",EDGE,"E3.14.0.2"),sQuery(id+"F0.wireOp",EDGE,"E3.14.0.3"),sQuery(id+"F0.wireOp",EDGE,"E3.15.0.0"),sQuery(id+"F0.wireOp",EDGE,"E3.15.0.1"),sQuery(id+"F0.wireOp",EDGE,"E3.15.0.2"),sQuery(id+"F0.wireOp",EDGE,"E3.15.0.3"),sQuery(id+"F0.wireOp",EDGE,"E3.16.0.0"),sQuery(id+"F0.wireOp",EDGE,"E3.16.0.1"),sQuery(id+"F0.wireOp",EDGE,"E3.16.0.2"),sQuery(id+"F0.wireOp",EDGE,"E3.16.0.3"),sQuery(id+"F0.wireOp",EDGE,"E3.17.0.0"),sQuery(id+"F0.wireOp",EDGE,"E3.17.0.1"),sQuery(id+"F0.wireOp",EDGE,"E3.17.0.2"),sQuery(id+"F0.wireOp",EDGE,"E3.17.0.3"),sQuery(id+"F0.wireOp",EDGE,"E3.18.0.0"),sQuery(id+"F0.wireOp",EDGE,"E3.18.0.1"),sQuery(id+"F0.wireOp",EDGE,"E3.18.0.2"),sQuery(id+"F0.wireOp",EDGE,"E3.18.0.3"),sQuery(id+"F0.wireOp",EDGE,"E3.19.0.0"),sQuery(id+"F0.wireOp",EDGE,"E3.19.0.1"),sQuery(id+"F0.wireOp",EDGE,"E3.19.0.2"),sQuery(id+"F0.wireOp",EDGE,"E3.19.0.3"),sQuery(id+"F0.wireOp",EDGE,"E3.20.0.0"),sQuery(id+"F0.wireOp",EDGE,"E3.20.0.1"),sQuery(id+"F0.wireOp",EDGE,"E3.20.0.2"),sQuery(id+"F0.wireOp",EDGE,"E3.20.0.3"),sQuery(id+"F0.wireOp",EDGE,"E3.21.0.0"),sQuery(id+"F0.wireOp",EDGE,"E3.21.0.1"),sQuery(id+"F0.wireOp",EDGE,"E3.21.0.2"),sQuery(id+"F0.wireOp",EDGE,"E3.21.0.3"),sQuery(id+"F0.wireOp",EDGE,"E3.22.0.0"),sQuery(id+"F0.wireOp",EDGE,"E3.22.0.1"),sQuery(id+"F0.wireOp",EDGE,"E3.22.0.2"),sQuery(id+"F0.wireOp",EDGE,"E3.22.0.3"),sQuery(id+"F0.wireOp",EDGE,"E3.23.0.0"),sQuery(id+"F0.wireOp",EDGE,"E3.23.0.1"),sQuery(id+"F0.wireOp",EDGE,"E3.23.0.2"),sQuery(id+"F0.wireOp",EDGE,"E3.23.0.3"),sQuery(id+"F0.wireOp",EDGE,"E3.24.0.0"),sQuery(id+"F0.wireOp",EDGE,"E3.24.0.1"),sQuery(id+"F0.wireOp",EDGE,"E3.24.0.2"),sQuery(id+"F0.wireOp",EDGE,"E3.24.0.3"),sQuery(id+"F0.wireOp",EDGE,"E3.25.0.0"),sQuery(id+"F0.wireOp",EDGE,"E3.25.0.1"),sQuery(id+"F0.wireOp",EDGE,"E3.25.0.2"),sQuery(id+"F0.wireOp",EDGE,"E3.25.0.3"),sQuery(id+"F0.wireOp",EDGE,"E3.26.0.0"),sQuery(id+"F0.wireOp",EDGE,"E3.26.0.1"),sQuery(id+"F0.wireOp",EDGE,"E3.26.0.2"),sQuery(id+"F0.wireOp",EDGE,"E3.26.0.3"),sQuery(id+"F0.wireOp",EDGE,"E3.27.0.0"),sQuery(id+"F0.wireOp",EDGE,"E3.27.0.1"),sQuery(id+"F0.wireOp",EDGE,"E3.27.0.2"),sQuery(id+"F0.wireOp",EDGE,"E3.27.0.3"),sQuery(id+"F0.wireOp",EDGE,"E3.28.0.0"),sQuery(id+"F0.wireOp",EDGE,"E3.28.0.1"),sQuery(id+"F0.wireOp",EDGE,"E3.28.0.2"),sQuery(id+"F0.wireOp",EDGE,"E3.28.0.3"),sQuery(id+"F0.wireOp",EDGE,"E3.29.0.0"),sQuery(id+"F0.wireOp",EDGE,"E3.29.0.1"),sQuery(id+"F0.wireOp",EDGE,"E3.29.0.2"),sQuery(id+"F0.wireOp",EDGE,"E3.29.0.3"),sQuery(id+"F0.wireOp",EDGE,"E3.30.0.0"),sQuery(id+"F0.wireOp",EDGE,"E3.30.0.1"),sQuery(id+"F0.wireOp",EDGE,"E3.30.0.2"),sQuery(id+"F0.wireOp",EDGE,"E3.30.0.3"),sQuery(id+"F0.wireOp",EDGE,"E3.31.0.0"),sQuery(id+"F0.wireOp",EDGE,"E3.31.0.1"),sQuery(id+"F0.wireOp",EDGE,"E3.31.0.2"),sQuery(id+"F0.wireOp",EDGE,"E3.31.0.3"),sQuery(id+"F0.wireOp",EDGE,"E3.32.0.0"),sQuery(id+"F0.wireOp",EDGE,"E3.32.0.1"),sQuery(id+"F0.wireOp",EDGE,"E3.32.0.2"),sQuery(id+"F0.wireOp",EDGE,"E3.32.0.3"),sQuery(id+"F0.wireOp",EDGE,"E3.33.0.0"),sQuery(id+"F0.wireOp",EDGE,"E3.33.0.1"),sQuery(id+"F0.wireOp",EDGE,"E3.33.0.2"),sQuery(id+"F0.wireOp",EDGE,"E3.33.0.3"),sQuery(id+"F0.wireOp",EDGE,"E3.34.0.0"),sQuery(id+"F0.wireOp",EDGE,"E3.34.0.1"),sQuery(id+"F0.wireOp",EDGE,"E3.34.0.2"),sQuery(id+"F0.wireOp",EDGE,"E3.34.0.3"),sQuery(id+"F0.wireOp",EDGE,"E3.35.0.0"),sQuery(id+"F0.wireOp",EDGE,"E3.35.0.1"),sQuery(id+"F0.wireOp",EDGE,"E3.35.0.2"),sQuery(id+"F0.wireOp",EDGE,"E3.35.0.3"),sQuery(id+"F0.wireOp",EDGE,"E3.36.0.0"),sQuery(id+"F0.wireOp",EDGE,"E3.36.0.1"),sQuery(id+"F0.wireOp",EDGE,"E3.36.0.2"),sQuery(id+"F0.wireOp",EDGE,"E3.36.0.3"),sQuery(id+"F0.wireOp",EDGE,"E3.37.0.0"),sQuery(id+"F0.wireOp",EDGE,"E3.37.0.1"),sQuery(id+"F0.wireOp",EDGE,"E3.37.0.2"),sQuery(id+"F0.wireOp",EDGE,"E3.37.0.3"),sQuery(id+"F0.wireOp",EDGE,"E3.38.0.0"),sQuery(id+"F0.wireOp",EDGE,"E3.38.0.1"),sQuery(id+"F0.wireOp",EDGE,"E3.38.0.2"),sQuery(id+"F0.wireOp",EDGE,"E3.38.0.3"),sQuery(id+"F0.wireOp",EDGE,"E3.39.0.0"),sQuery(id+"F0.wireOp",EDGE,"E3.39.0.1"),sQuery(id+"F0.wireOp",EDGE,"E3.39.0.2"),sQuery(id+"F0.wireOp",EDGE,"E3.39.0.3"),sQuery(id+"F0.wireOp",EDGE,"E3.40.0.0"),sQuery(id+"F0.wireOp",EDGE,"E3.40.0.1"),sQuery(id+"F0.wireOp",EDGE,"E3.40.0.2"),sQuery(id+"F0.wireOp",EDGE,"E3.40.0.3"),sQuery(id+"F0.wireOp",EDGE,"E3.41.0.0"),sQuery(id+"F0.wireOp",EDGE,"E3.41.0.1"),sQuery(id+"F0.wireOp",EDGE,"E3.41.0.2"),sQuery(id+"F0.wireOp",EDGE,"E3.41.0.3"),sQuery(id+"F0.wireOp",EDGE,"E3.42.0.0"),sQuery(id+"F0.wireOp",EDGE,"E3.42.0.1"),sQuery(id+"F0.wireOp",EDGE,"E3.42.0.2"),sQuery(id+"F0.wireOp",EDGE,"E3.42.0.3"),sQuery(id+"F0.wireOp",EDGE,"E3.43.0.0"),sQuery(id+"F0.wireOp",EDGE,"E3.43.0.1"),sQuery(id+"F0.wireOp",EDGE,"E3.43.0.2"),sQuery(id+"F0.wireOp",EDGE,"E3.43.0.3"),sQuery(id+"F0.wireOp",EDGE,"E3.44.0.0"),sQuery(id+"F0.wireOp",EDGE,"E3.44.0.1"),sQuery(id+"F0.wireOp",EDGE,"E3.44.0.2"),sQuery(id+"F0.wireOp",EDGE,"E3.44.0.3"),sQuery(id+"F0.wireOp",EDGE,"E3.45.0.0"),sQuery(id+"F0.wireOp",EDGE,"E3.45.0.1"),sQuery(id+"F0.wireOp",EDGE,"E3.45.0.2"),sQuery(id+"F0.wireOp",EDGE,"E3.45.0.3"),sQuery(id+"F0.wireOp",EDGE,"E3.46.0.0"),sQuery(id+"F0.wireOp",EDGE,"E3.46.0.1"),sQuery(id+"F0.wireOp",EDGE,"E3.46.0.2"),sQuery(id+"F0.wireOp",EDGE,"E3.46.0.3"),sQuery(id+"F0.wireOp",EDGE,"E3.47.0.0"),sQuery(id+"F0.wireOp",EDGE,"E3.47.0.1"),sQuery(id+"F0.wireOp",EDGE,"E3.47.0.2"),sQuery(id+"F0.wireOp",EDGE,"E3.47.0.3"),sQuery(id+"F0.wireOp",EDGE,"E3.48.0.0"),sQuery(id+"F0.wireOp",EDGE,"E3.48.0.1"),sQuery(id+"F0.wireOp",EDGE,"E3.48.0.2"),sQuery(id+"F0.wireOp",EDGE,"E3.48.0.3"),sQuery(id+"F0.wireOp",EDGE,"E3.49.0.0"),sQuery(id+"F0.wireOp",EDGE,"E3.49.0.1"),sQuery(id+"F0.wireOp",EDGE,"E3.49.0.2"),sQuery(id+"F0.wireOp",EDGE,"E4.bottom"),sQuery(id+"F0.wireOp",EDGE,"E4.left"),sQuery(id+"F0.wireOp",EDGE,"E4.right"),sQuery(id+"F0.wireOp",EDGE,"E5"),sQuery(id+"F0.wireOp",EDGE,"E6.1.0.0"),sQuery(id+"F0.wireOp",EDGE,"E6.1.0.1"),sQuery(id+"F0.wireOp",EDGE,"E6.1.0.2"),sQuery(id+"F0.wireOp",EDGE,"E6.1.0.3"),sQuery(id+"F0.wireOp",EDGE,"E6.2.0.0"),sQuery(id+"F0.wireOp",EDGE,"E6.2.0.1"),sQuery(id+"F0.wireOp",EDGE,"E6.2.0.2"),sQuery(id+"F0.wireOp",EDGE,"E6.2.0.3"),sQuery(id+"F0.wireOp",EDGE,"E6.3.0.0"),sQuery(id+"F0.wireOp",EDGE,"E6.3.0.1"),sQuery(id+"F0.wireOp",EDGE,"E6.3.0.2"),sQuery(id+"F0.wireOp",EDGE,"E6.3.0.3"),sQuery(id+"F0.wireOp",EDGE,"E6.4.0.0"),sQuery(id+"F0.wireOp",EDGE,"E6.4.0.1"),sQuery(id+"F0.wireOp",EDGE,"E6.4.0.2"),sQuery(id+"F0.wireOp",EDGE,"E6.4.0.3"),sQuery(id+"F0.wireOp",EDGE,"E6.5.0.0"),sQuery(id+"F0.wireOp",EDGE,"E6.5.0.1"),sQuery(id+"F0.wireOp",EDGE,"E6.5.0.2"),sQuery(id+"F0.wireOp",EDGE,"E6.5.0.3"),sQuery(id+"F0.wireOp",EDGE,"E6.6.0.0"),sQuery(id+"F0.wireOp",EDGE,"E6.6.0.1"),sQuery(id+"F0.wireOp",EDGE,"E6.6.0.2"),sQuery(id+"F0.wireOp",EDGE,"E6.6.0.3"),sQuery(id+"F0.wireOp",EDGE,"E6.7.0.0"),sQuery(id+"F0.wireOp",EDGE,"E6.7.0.1"),sQuery(id+"F0.wireOp",EDGE,"E6.7.0.2"),sQuery(id+"F0.wireOp",EDGE,"E6.7.0.3"),sQuery(id+"F0.wireOp",EDGE,"E6.8.0.0"),sQuery(id+"F0.wireOp",EDGE,"E6.8.0.1"),sQuery(id+"F0.wireOp",EDGE,"E6.8.0.2"),sQuery(id+"F0.wireOp",EDGE,"E6.8.0.3"),sQuery(id+"F0.wireOp",EDGE,"E6.9.0.0"),sQuery(id+"F0.wireOp",EDGE,"E6.9.0.1"),sQuery(id+"F0.wireOp",EDGE,"E6.9.0.2"),sQuery(id+"F0.wireOp",EDGE,"E6.9.0.3"),sQuery(id+"F0.wireOp",EDGE,"E6.10.0.0"),sQuery(id+"F0.wireOp",EDGE,"E6.10.0.1"),sQuery(id+"F0.wireOp",EDGE,"E6.10.0.2"),sQuery(id+"F0.wireOp",EDGE,"E6.10.0.3"),sQuery(id+"F0.wireOp",EDGE,"E6.11.0.0"),sQuery(id+"F0.wireOp",EDGE,"E6.11.0.1"),sQuery(id+"F0.wireOp",EDGE,"E6.11.0.2"),sQuery(id+"F0.wireOp",EDGE,"E6.11.0.3"),sQuery(id+"F0.wireOp",EDGE,"E6.12.0.0"),sQuery(id+"F0.wireOp",EDGE,"E6.12.0.1"),sQuery(id+"F0.wireOp",EDGE,"E6.12.0.2"),sQuery(id+"F0.wireOp",EDGE,"E6.12.0.3"),sQuery(id+"F0.wireOp",EDGE,"E6.13.0.0"),sQuery(id+"F0.wireOp",EDGE,"E6.13.0.1"),sQuery(id+"F0.wireOp",EDGE,"E6.13.0.2"),sQuery(id+"F0.wireOp",EDGE,"E6.13.0.3"),sQuery(id+"F0.wireOp",EDGE,"E6.14.0.0"),sQuery(id+"F0.wireOp",EDGE,"E6.14.0.1"),sQuery(id+"F0.wireOp",EDGE,"E6.14.0.2"),sQuery(id+"F0.wireOp",EDGE,"E6.14.0.3"),sQuery(id+"F0.wireOp",EDGE,"E6.15.0.0"),sQuery(id+"F0.wireOp",EDGE,"E6.15.0.1"),sQuery(id+"F0.wireOp",EDGE,"E6.15.0.2"),sQuery(id+"F0.wireOp",EDGE,"E6.15.0.3"),sQuery(id+"F0.wireOp",EDGE,"E6.16.0.0"),sQuery(id+"F0.wireOp",EDGE,"E6.16.0.1"),sQuery(id+"F0.wireOp",EDGE,"E6.16.0.2"),sQuery(id+"F0.wireOp",EDGE,"E6.16.0.3"),sQuery(id+"F0.wireOp",EDGE,"E6.17.0.0"),sQuery(id+"F0.wireOp",EDGE,"E6.17.0.1"),sQuery(id+"F0.wireOp",EDGE,"E6.17.0.2"),sQuery(id+"F0.wireOp",EDGE,"E6.17.0.3"),sQuery(id+"F0.wireOp",EDGE,"E6.18.0.0"),sQuery(id+"F0.wireOp",EDGE,"E6.18.0.1"),sQuery(id+"F0.wireOp",EDGE,"E6.18.0.2"),sQuery(id+"F0.wireOp",EDGE,"E6.18.0.3"),sQuery(id+"F0.wireOp",EDGE,"E6.19.0.0"),sQuery(id+"F0.wireOp",EDGE,"E6.19.0.1"),sQuery(id+"F0.wireOp",EDGE,"E6.19.0.2"),sQuery(id+"F0.wireOp",EDGE,"E6.19.0.3"),sQuery(id+"F0.wireOp",EDGE,"E6.20.0.0"),sQuery(id+"F0.wireOp",EDGE,"E6.20.0.1"),sQuery(id+"F0.wireOp",EDGE,"E6.20.0.2"),sQuery(id+"F0.wireOp",EDGE,"E6.20.0.3"),sQuery(id+"F0.wireOp",EDGE,"E6.21.0.0"),sQuery(id+"F0.wireOp",EDGE,"E6.21.0.1"),sQuery(id+"F0.wireOp",EDGE,"E6.21.0.2"),sQuery(id+"F0.wireOp",EDGE,"E6.21.0.3"),sQuery(id+"F0.wireOp",EDGE,"E6.22.0.0"),sQuery(id+"F0.wireOp",EDGE,"E6.22.0.1"),sQuery(id+"F0.wireOp",EDGE,"E6.22.0.2"),sQuery(id+"F0.wireOp",EDGE,"E6.22.0.3"),sQuery(id+"F0.wireOp",EDGE,"E6.23.0.0"),sQuery(id+"F0.wireOp",EDGE,"E6.23.0.1"),sQuery(id+"F0.wireOp",EDGE,"E6.23.0.2"),sQuery(id+"F0.wireOp",EDGE,"E6.23.0.3"),sQuery(id+"F0.wireOp",EDGE,"E6.24.0.0"),sQuery(id+"F0.wireOp",EDGE,"E6.24.0.1"),sQuery(id+"F0.wireOp",EDGE,"E6.24.0.2"),sQuery(id+"F0.wireOp",EDGE,"E6.24.0.3"),sQuery(id+"F0.wireOp",EDGE,"E6.25.0.0"),sQuery(id+"F0.wireOp",EDGE,"E6.25.0.1"),sQuery(id+"F0.wireOp",EDGE,"E6.25.0.2"),sQuery(id+"F0.wireOp",EDGE,"E6.25.0.3"),sQuery(id+"F0.wireOp",EDGE,"E6.26.0.0"),sQuery(id+"F0.wireOp",EDGE,"E6.26.0.1"),sQuery(id+"F0.wireOp",EDGE,"E6.26.0.2"),sQuery(id+"F0.wireOp",EDGE,"E6.26.0.3"),sQuery(id+"F0.wireOp",EDGE,"E6.27.0.0"),sQuery(id+"F0.wireOp",EDGE,"E6.27.0.1"),sQuery(id+"F0.wireOp",EDGE,"E6.27.0.2"),sQuery(id+"F0.wireOp",EDGE,"E6.27.0.3"),sQuery(id+"F0.wireOp",EDGE,"E6.28.0.0"),sQuery(id+"F0.wireOp",EDGE,"E6.28.0.1"),sQuery(id+"F0.wireOp",EDGE,"E6.28.0.2"),sQuery(id+"F0.wireOp",EDGE,"E6.28.0.3"),sQuery(id+"F0.wireOp",EDGE,"E6.29.0.0"),sQuery(id+"F0.wireOp",EDGE,"E6.29.0.1"),sQuery(id+"F0.wireOp",EDGE,"E6.29.0.2"),sQuery(id+"F0.wireOp",EDGE,"E6.29.0.3"),sQuery(id+"F0.wireOp",EDGE,"E6.30.0.0"),sQuery(id+"F0.wireOp",EDGE,"E6.30.0.1"),sQuery(id+"F0.wireOp",EDGE,"E6.30.0.2"),sQuery(id+"F0.wireOp",EDGE,"E6.30.0.3"),sQuery(id+"F0.wireOp",EDGE,"E6.31.0.0"),sQuery(id+"F0.wireOp",EDGE,"E6.31.0.1"),sQuery(id+"F0.wireOp",EDGE,"E6.31.0.2"),sQuery(id+"F0.wireOp",EDGE,"E6.31.0.3"),sQuery(id+"F0.wireOp",EDGE,"E6.32.0.0"),sQuery(id+"F0.wireOp",EDGE,"E6.32.0.1"),sQuery(id+"F0.wireOp",EDGE,"E6.32.0.2"),sQuery(id+"F0.wireOp",EDGE,"E6.32.0.3"),sQuery(id+"F0.wireOp",EDGE,"E6.33.0.0"),sQuery(id+"F0.wireOp",EDGE,"E6.33.0.1"),sQuery(id+"F0.wireOp",EDGE,"E6.33.0.2"),sQuery(id+"F0.wireOp",EDGE,"E6.33.0.3"),sQuery(id+"F0.wireOp",EDGE,"E6.34.0.0"),sQuery(id+"F0.wireOp",EDGE,"E6.34.0.1"),sQuery(id+"F0.wireOp",EDGE,"E6.34.0.2"),sQuery(id+"F0.wireOp",EDGE,"E6.34.0.3"),sQuery(id+"F0.wireOp",EDGE,"E6.35.0.0"),sQuery(id+"F0.wireOp",EDGE,"E6.35.0.1"),sQuery(id+"F0.wireOp",EDGE,"E6.35.0.2"),sQuery(id+"F0.wireOp",EDGE,"E6.35.0.3"),sQuery(id+"F0.wireOp",EDGE,"E6.36.0.0"),sQuery(id+"F0.wireOp",EDGE,"E6.36.0.1"),sQuery(id+"F0.wireOp",EDGE,"E6.36.0.2"),sQuery(id+"F0.wireOp",EDGE,"E6.36.0.3"),sQuery(id+"F0.wireOp",EDGE,"E6.37.0.0"),sQuery(id+"F0.wireOp",EDGE,"E6.37.0.1"),sQuery(id+"F0.wireOp",EDGE,"E6.37.0.2"),sQuery(id+"F0.wireOp",EDGE,"E6.37.0.3"),sQuery(id+"F0.wireOp",EDGE,"E6.38.0.0"),sQuery(id+"F0.wireOp",EDGE,"E6.38.0.1"),sQuery(id+"F0.wireOp",EDGE,"E6.38.0.2"),sQuery(id+"F0.wireOp",EDGE,"E6.38.0.3"),sQuery(id+"F0.wireOp",EDGE,"E6.39.0.0"),sQuery(id+"F0.wireOp",EDGE,"E6.39.0.1"),sQuery(id+"F0.wireOp",EDGE,"E6.39.0.2"),sQuery(id+"F0.wireOp",EDGE,"E6.39.0.3"),sQuery(id+"F0.wireOp",EDGE,"E6.40.0.0"),sQuery(id+"F0.wireOp",EDGE,"E6.40.0.1"),sQuery(id+"F0.wireOp",EDGE,"E6.40.0.2"),sQuery(id+"F0.wireOp",EDGE,"E6.40.0.3"),sQuery(id+"F0.wireOp",EDGE,"E6.41.0.0"),sQuery(id+"F0.wireOp",EDGE,"E6.41.0.1"),sQuery(id+"F0.wireOp",EDGE,"E6.41.0.2"),sQuery(id+"F0.wireOp",EDGE,"E6.41.0.3"),sQuery(id+"F0.wireOp",EDGE,"E6.42.0.0"),sQuery(id+"F0.wireOp",EDGE,"E6.42.0.1"),sQuery(id+"F0.wireOp",EDGE,"E6.42.0.2"),sQuery(id+"F0.wireOp",EDGE,"E6.42.0.3"),sQuery(id+"F0.wireOp",EDGE,"E6.43.0.0"),sQuery(id+"F0.wireOp",EDGE,"E6.43.0.1"),sQuery(id+"F0.wireOp",EDGE,"E6.43.0.2"),sQuery(id+"F0.wireOp",EDGE,"E6.43.0.3"),sQuery(id+"F0.wireOp",EDGE,"E6.44.0.0"),sQuery(id+"F0.wireOp",EDGE,"E6.44.0.1"),sQuery(id+"F0.wireOp",EDGE,"E6.44.0.2"),sQuery(id+"F0.wireOp",EDGE,"E6.44.0.3"),sQuery(id+"F0.wireOp",EDGE,"E6.45.0.0"),sQuery(id+"F0.wireOp",EDGE,"E6.45.0.1"),sQuery(id+"F0.wireOp",EDGE,"E6.45.0.2"),sQuery(id+"F0.wireOp",EDGE,"E6.45.0.3"),sQuery(id+"F0.wireOp",EDGE,"E6.46.0.0"),sQuery(id+"F0.wireOp",EDGE,"E6.46.0.1"),sQuery(id+"F0.wireOp",EDGE,"E6.46.0.2"),sQuery(id+"F0.wireOp",EDGE,"E6.46.0.3"),sQuery(id+"F0.wireOp",EDGE,"E6.47.0.0"),sQuery(id+"F0.wireOp",EDGE,"E6.47.0.1"),sQuery(id+"F0.wireOp",EDGE,"E6.47.0.2"),sQuery(id+"F0.wireOp",EDGE,"E6.47.0.3"),sQuery(id+"F0.wireOp",EDGE,"E6.48.0.0"),sQuery(id+"F0.wireOp",EDGE,"E6.48.0.1"),sQuery(id+"F0.wireOp",EDGE,"E6.48.0.2"),sQuery(id+"F0.wireOp",EDGE,"E6.48.0.3"),sQuery(id+"F0.wireOp",EDGE,"E6.49.0.0"),sQuery(id+"F0.wireOp",EDGE,"E6.49.0.1"),sQuery(id+"F0.wireOp",EDGE,"E7"),sQuery(id+"F0.wireOp",EDGE,"E8"),sQuery(id+"F0.wireOp",EDGE,"E9"),sQuery(id+"F0.wireOp",EDGE,"E10"),sQuery(id+"F0.wireOp",EDGE,"E11"),sQuery(id+"F0.wireOp",EDGE,"E12"),sQuery(id+"F0.wireOp",EDGE,"E13"),sQuery(id+"F0.wireOp",EDGE,"E14"),sQuery(id+"F0.wireOp",EDGE,"E15"),sQuery(id+"F0.wireOp",EDGE,"E16"),sQuery(id+"F0.wireOp",EDGE,"E17"),sQuery(id+"F0.wireOp",EDGE,"E18"),sQuery(id+"F0.wireOp",EDGE,"E19"),sQuery(id+"F0.wireOp",EDGE,"E20"),sQuery(id+"F0.wireOp",EDGE,"E21"),sQuery(id+"F0.wireOp",EDGE,"E22"),sQuery(id+"F0.wireOp",EDGE,"E23"),sQuery(id+"F0.wireOp",EDGE,"E24"),sQuery(id+"F0.wireOp",EDGE,"E25"),sQuery(id+"F0.wireOp",EDGE,"E26"),sQuery(id+"F0.wireOp",EDGE,"E27"),sQuery(id+"F0.wireOp",EDGE,"E28"),sQuery(id+"F0.wireOp",EDGE,"E29"),sQuery(id+"F0.wireOp",EDGE,"E30"),sQuery(id+"F0.wireOp",EDGE,"etuK1Xr9-J4i1-57WR-O4AE-Va2F9wOQP8k6"),sQuery(id+"F0.wireOp",EDGE,"9MBbQYz1-y2p6-nwSH-8az1-lH37U9JjGGAZ")])]});
            transform(context, id + "F2", {"entities" : qUnion([Q0]), "transformType" : TransformType.TRANSLATION_3D, "dx" : 0 * mm, "dy" : 89.93 * mm, "dz" : 0 * mm, "makeCopy" : true});
        }
        {
            var Q0;
            Q0=makeQuery(id+"F2.opPattern","COPY",BODY,{"derivedFrom":makeQuery(id+"F1.opExtrude","SWEPT_BODY",BODY,{"disambiguationData":[OSD([sQuery(id+"F0.wireOp",EDGE,"E1.bottom"),sQuery(id+"F0.wireOp",EDGE,"E1.left"),sQuery(id+"F0.wireOp",EDGE,"E1.right"),sQuery(id+"F0.wireOp",EDGE,"E2"),sQuery(id+"F0.wireOp",EDGE,"E3.1.0.0"),sQuery(id+"F0.wireOp",EDGE,"E3.1.0.1"),sQuery(id+"F0.wireOp",EDGE,"E3.1.0.2"),sQuery(id+"F0.wireOp",EDGE,"E3.1.0.3"),sQuery(id+"F0.wireOp",EDGE,"E3.2.0.0"),sQuery(id+"F0.wireOp",EDGE,"E3.2.0.1"),sQuery(id+"F0.wireOp",EDGE,"E3.2.0.2"),sQuery(id+"F0.wireOp",EDGE,"E3.2.0.3"),sQuery(id+"F0.wireOp",EDGE,"E3.3.0.0"),sQuery(id+"F0.wireOp",EDGE,"E3.3.0.1"),sQuery(id+"F0.wireOp",EDGE,"E3.3.0.2"),sQuery(id+"F0.wireOp",EDGE,"E3.3.0.3"),sQuery(id+"F0.wireOp",EDGE,"E3.4.0.0"),sQuery(id+"F0.wireOp",EDGE,"E3.4.0.1"),sQuery(id+"F0.wireOp",EDGE,"E3.4.0.2"),sQuery(id+"F0.wireOp",EDGE,"E3.4.0.3"),sQuery(id+"F0.wireOp",EDGE,"E3.5.0.0"),sQuery(id+"F0.wireOp",EDGE,"E3.5.0.1"),sQuery(id+"F0.wireOp",EDGE,"E3.5.0.2"),sQuery(id+"F0.wireOp",EDGE,"E3.5.0.3"),sQuery(id+"F0.wireOp",EDGE,"E3.6.0.0"),sQuery(id+"F0.wireOp",EDGE,"E3.6.0.1"),sQuery(id+"F0.wireOp",EDGE,"E3.6.0.2"),sQuery(id+"F0.wireOp",EDGE,"E3.6.0.3"),sQuery(id+"F0.wireOp",EDGE,"E3.7.0.0"),sQuery(id+"F0.wireOp",EDGE,"E3.7.0.1"),sQuery(id+"F0.wireOp",EDGE,"E3.7.0.2"),sQuery(id+"F0.wireOp",EDGE,"E3.7.0.3"),sQuery(id+"F0.wireOp",EDGE,"E3.8.0.0"),sQuery(id+"F0.wireOp",EDGE,"E3.8.0.1"),sQuery(id+"F0.wireOp",EDGE,"E3.8.0.2"),sQuery(id+"F0.wireOp",EDGE,"E3.8.0.3"),sQuery(id+"F0.wireOp",EDGE,"E3.9.0.0"),sQuery(id+"F0.wireOp",EDGE,"E3.9.0.1"),sQuery(id+"F0.wireOp",EDGE,"E3.9.0.2"),sQuery(id+"F0.wireOp",EDGE,"E3.9.0.3"),sQuery(id+"F0.wireOp",EDGE,"E3.10.0.0"),sQuery(id+"F0.wireOp",EDGE,"E3.10.0.1"),sQuery(id+"F0.wireOp",EDGE,"E3.10.0.2"),sQuery(id+"F0.wireOp",EDGE,"E3.10.0.3"),sQuery(id+"F0.wireOp",EDGE,"E3.11.0.0"),sQuery(id+"F0.wireOp",EDGE,"E3.11.0.1"),sQuery(id+"F0.wireOp",EDGE,"E3.11.0.2"),sQuery(id+"F0.wireOp",EDGE,"E3.11.0.3"),sQuery(id+"F0.wireOp",EDGE,"E3.12.0.0"),sQuery(id+"F0.wireOp",EDGE,"E3.12.0.1"),sQuery(id+"F0.wireOp",EDGE,"E3.12.0.2"),sQuery(id+"F0.wireOp",EDGE,"E3.12.0.3"),sQuery(id+"F0.wireOp",EDGE,"E3.13.0.0"),sQuery(id+"F0.wireOp",EDGE,"E3.13.0.1"),sQuery(id+"F0.wireOp",EDGE,"E3.13.0.2"),sQuery(id+"F0.wireOp",EDGE,"E3.13.0.3"),sQuery(id+"F0.wireOp",EDGE,"E3.14.0.0"),sQuery(id+"F0.wireOp",EDGE,"E3.14.0.1"),sQuery(id+"F0.wireOp",EDGE,"E3.14.0.2"),sQuery(id+"F0.wireOp",EDGE,"E3.14.0.3"),sQuery(id+"F0.wireOp",EDGE,"E3.15.0.0"),sQuery(id+"F0.wireOp",EDGE,"E3.15.0.1"),sQuery(id+"F0.wireOp",EDGE,"E3.15.0.2"),sQuery(id+"F0.wireOp",EDGE,"E3.15.0.3"),sQuery(id+"F0.wireOp",EDGE,"E3.16.0.0"),sQuery(id+"F0.wireOp",EDGE,"E3.16.0.1"),sQuery(id+"F0.wireOp",EDGE,"E3.16.0.2"),sQuery(id+"F0.wireOp",EDGE,"E3.16.0.3"),sQuery(id+"F0.wireOp",EDGE,"E3.17.0.0"),sQuery(id+"F0.wireOp",EDGE,"E3.17.0.1"),sQuery(id+"F0.wireOp",EDGE,"E3.17.0.2"),sQuery(id+"F0.wireOp",EDGE,"E3.17.0.3"),sQuery(id+"F0.wireOp",EDGE,"E3.18.0.0"),sQuery(id+"F0.wireOp",EDGE,"E3.18.0.1"),sQuery(id+"F0.wireOp",EDGE,"E3.18.0.2"),sQuery(id+"F0.wireOp",EDGE,"E3.18.0.3"),sQuery(id+"F0.wireOp",EDGE,"E3.19.0.0"),sQuery(id+"F0.wireOp",EDGE,"E3.19.0.1"),sQuery(id+"F0.wireOp",EDGE,"E3.19.0.2"),sQuery(id+"F0.wireOp",EDGE,"E3.19.0.3"),sQuery(id+"F0.wireOp",EDGE,"E3.20.0.0"),sQuery(id+"F0.wireOp",EDGE,"E3.20.0.1"),sQuery(id+"F0.wireOp",EDGE,"E3.20.0.2"),sQuery(id+"F0.wireOp",EDGE,"E3.20.0.3"),sQuery(id+"F0.wireOp",EDGE,"E3.21.0.0"),sQuery(id+"F0.wireOp",EDGE,"E3.21.0.1"),sQuery(id+"F0.wireOp",EDGE,"E3.21.0.2"),sQuery(id+"F0.wireOp",EDGE,"E3.21.0.3"),sQuery(id+"F0.wireOp",EDGE,"E3.22.0.0"),sQuery(id+"F0.wireOp",EDGE,"E3.22.0.1"),sQuery(id+"F0.wireOp",EDGE,"E3.22.0.2"),sQuery(id+"F0.wireOp",EDGE,"E3.22.0.3"),sQuery(id+"F0.wireOp",EDGE,"E3.23.0.0"),sQuery(id+"F0.wireOp",EDGE,"E3.23.0.1"),sQuery(id+"F0.wireOp",EDGE,"E3.23.0.2"),sQuery(id+"F0.wireOp",EDGE,"E3.23.0.3"),sQuery(id+"F0.wireOp",EDGE,"E3.24.0.0"),sQuery(id+"F0.wireOp",EDGE,"E3.24.0.1"),sQuery(id+"F0.wireOp",EDGE,"E3.24.0.2"),sQuery(id+"F0.wireOp",EDGE,"E3.24.0.3"),sQuery(id+"F0.wireOp",EDGE,"E3.25.0.0"),sQuery(id+"F0.wireOp",EDGE,"E3.25.0.1"),sQuery(id+"F0.wireOp",EDGE,"E3.25.0.2"),sQuery(id+"F0.wireOp",EDGE,"E3.25.0.3"),sQuery(id+"F0.wireOp",EDGE,"E3.26.0.0"),sQuery(id+"F0.wireOp",EDGE,"E3.26.0.1"),sQuery(id+"F0.wireOp",EDGE,"E3.26.0.2"),sQuery(id+"F0.wireOp",EDGE,"E3.26.0.3"),sQuery(id+"F0.wireOp",EDGE,"E3.27.0.0"),sQuery(id+"F0.wireOp",EDGE,"E3.27.0.1"),sQuery(id+"F0.wireOp",EDGE,"E3.27.0.2"),sQuery(id+"F0.wireOp",EDGE,"E3.27.0.3"),sQuery(id+"F0.wireOp",EDGE,"E3.28.0.0"),sQuery(id+"F0.wireOp",EDGE,"E3.28.0.1"),sQuery(id+"F0.wireOp",EDGE,"E3.28.0.2"),sQuery(id+"F0.wireOp",EDGE,"E3.28.0.3"),sQuery(id+"F0.wireOp",EDGE,"E3.29.0.0"),sQuery(id+"F0.wireOp",EDGE,"E3.29.0.1"),sQuery(id+"F0.wireOp",EDGE,"E3.29.0.2"),sQuery(id+"F0.wireOp",EDGE,"E3.29.0.3"),sQuery(id+"F0.wireOp",EDGE,"E3.30.0.0"),sQuery(id+"F0.wireOp",EDGE,"E3.30.0.1"),sQuery(id+"F0.wireOp",EDGE,"E3.30.0.2"),sQuery(id+"F0.wireOp",EDGE,"E3.30.0.3"),sQuery(id+"F0.wireOp",EDGE,"E3.31.0.0"),sQuery(id+"F0.wireOp",EDGE,"E3.31.0.1"),sQuery(id+"F0.wireOp",EDGE,"E3.31.0.2"),sQuery(id+"F0.wireOp",EDGE,"E3.31.0.3"),sQuery(id+"F0.wireOp",EDGE,"E3.32.0.0"),sQuery(id+"F0.wireOp",EDGE,"E3.32.0.1"),sQuery(id+"F0.wireOp",EDGE,"E3.32.0.2"),sQuery(id+"F0.wireOp",EDGE,"E3.32.0.3"),sQuery(id+"F0.wireOp",EDGE,"E3.33.0.0"),sQuery(id+"F0.wireOp",EDGE,"E3.33.0.1"),sQuery(id+"F0.wireOp",EDGE,"E3.33.0.2"),sQuery(id+"F0.wireOp",EDGE,"E3.33.0.3"),sQuery(id+"F0.wireOp",EDGE,"E3.34.0.0"),sQuery(id+"F0.wireOp",EDGE,"E3.34.0.1"),sQuery(id+"F0.wireOp",EDGE,"E3.34.0.2"),sQuery(id+"F0.wireOp",EDGE,"E3.34.0.3"),sQuery(id+"F0.wireOp",EDGE,"E3.35.0.0"),sQuery(id+"F0.wireOp",EDGE,"E3.35.0.1"),sQuery(id+"F0.wireOp",EDGE,"E3.35.0.2"),sQuery(id+"F0.wireOp",EDGE,"E3.35.0.3"),sQuery(id+"F0.wireOp",EDGE,"E3.36.0.0"),sQuery(id+"F0.wireOp",EDGE,"E3.36.0.1"),sQuery(id+"F0.wireOp",EDGE,"E3.36.0.2"),sQuery(id+"F0.wireOp",EDGE,"E3.36.0.3"),sQuery(id+"F0.wireOp",EDGE,"E3.37.0.0"),sQuery(id+"F0.wireOp",EDGE,"E3.37.0.1"),sQuery(id+"F0.wireOp",EDGE,"E3.37.0.2"),sQuery(id+"F0.wireOp",EDGE,"E3.37.0.3"),sQuery(id+"F0.wireOp",EDGE,"E3.38.0.0"),sQuery(id+"F0.wireOp",EDGE,"E3.38.0.1"),sQuery(id+"F0.wireOp",EDGE,"E3.38.0.2"),sQuery(id+"F0.wireOp",EDGE,"E3.38.0.3"),sQuery(id+"F0.wireOp",EDGE,"E3.39.0.0"),sQuery(id+"F0.wireOp",EDGE,"E3.39.0.1"),sQuery(id+"F0.wireOp",EDGE,"E3.39.0.2"),sQuery(id+"F0.wireOp",EDGE,"E3.39.0.3"),sQuery(id+"F0.wireOp",EDGE,"E3.40.0.0"),sQuery(id+"F0.wireOp",EDGE,"E3.40.0.1"),sQuery(id+"F0.wireOp",EDGE,"E3.40.0.2"),sQuery(id+"F0.wireOp",EDGE,"E3.40.0.3"),sQuery(id+"F0.wireOp",EDGE,"E3.41.0.0"),sQuery(id+"F0.wireOp",EDGE,"E3.41.0.1"),sQuery(id+"F0.wireOp",EDGE,"E3.41.0.2"),sQuery(id+"F0.wireOp",EDGE,"E3.41.0.3"),sQuery(id+"F0.wireOp",EDGE,"E3.42.0.0"),sQuery(id+"F0.wireOp",EDGE,"E3.42.0.1"),sQuery(id+"F0.wireOp",EDGE,"E3.42.0.2"),sQuery(id+"F0.wireOp",EDGE,"E3.42.0.3"),sQuery(id+"F0.wireOp",EDGE,"E3.43.0.0"),sQuery(id+"F0.wireOp",EDGE,"E3.43.0.1"),sQuery(id+"F0.wireOp",EDGE,"E3.43.0.2"),sQuery(id+"F0.wireOp",EDGE,"E3.43.0.3"),sQuery(id+"F0.wireOp",EDGE,"E3.44.0.0"),sQuery(id+"F0.wireOp",EDGE,"E3.44.0.1"),sQuery(id+"F0.wireOp",EDGE,"E3.44.0.2"),sQuery(id+"F0.wireOp",EDGE,"E3.44.0.3"),sQuery(id+"F0.wireOp",EDGE,"E3.45.0.0"),sQuery(id+"F0.wireOp",EDGE,"E3.45.0.1"),sQuery(id+"F0.wireOp",EDGE,"E3.45.0.2"),sQuery(id+"F0.wireOp",EDGE,"E3.45.0.3"),sQuery(id+"F0.wireOp",EDGE,"E3.46.0.0"),sQuery(id+"F0.wireOp",EDGE,"E3.46.0.1"),sQuery(id+"F0.wireOp",EDGE,"E3.46.0.2"),sQuery(id+"F0.wireOp",EDGE,"E3.46.0.3"),sQuery(id+"F0.wireOp",EDGE,"E3.47.0.0"),sQuery(id+"F0.wireOp",EDGE,"E3.47.0.1"),sQuery(id+"F0.wireOp",EDGE,"E3.47.0.2"),sQuery(id+"F0.wireOp",EDGE,"E3.47.0.3"),sQuery(id+"F0.wireOp",EDGE,"E3.48.0.0"),sQuery(id+"F0.wireOp",EDGE,"E3.48.0.1"),sQuery(id+"F0.wireOp",EDGE,"E3.48.0.2"),sQuery(id+"F0.wireOp",EDGE,"E3.48.0.3"),sQuery(id+"F0.wireOp",EDGE,"E3.49.0.0"),sQuery(id+"F0.wireOp",EDGE,"E3.49.0.1"),sQuery(id+"F0.wireOp",EDGE,"E3.49.0.2"),sQuery(id+"F0.wireOp",EDGE,"E4.bottom"),sQuery(id+"F0.wireOp",EDGE,"E4.left"),sQuery(id+"F0.wireOp",EDGE,"E4.right"),sQuery(id+"F0.wireOp",EDGE,"E5"),sQuery(id+"F0.wireOp",EDGE,"E6.1.0.0"),sQuery(id+"F0.wireOp",EDGE,"E6.1.0.1"),sQuery(id+"F0.wireOp",EDGE,"E6.1.0.2"),sQuery(id+"F0.wireOp",EDGE,"E6.1.0.3"),sQuery(id+"F0.wireOp",EDGE,"E6.2.0.0"),sQuery(id+"F0.wireOp",EDGE,"E6.2.0.1"),sQuery(id+"F0.wireOp",EDGE,"E6.2.0.2"),sQuery(id+"F0.wireOp",EDGE,"E6.2.0.3"),sQuery(id+"F0.wireOp",EDGE,"E6.3.0.0"),sQuery(id+"F0.wireOp",EDGE,"E6.3.0.1"),sQuery(id+"F0.wireOp",EDGE,"E6.3.0.2"),sQuery(id+"F0.wireOp",EDGE,"E6.3.0.3"),sQuery(id+"F0.wireOp",EDGE,"E6.4.0.0"),sQuery(id+"F0.wireOp",EDGE,"E6.4.0.1"),sQuery(id+"F0.wireOp",EDGE,"E6.4.0.2"),sQuery(id+"F0.wireOp",EDGE,"E6.4.0.3"),sQuery(id+"F0.wireOp",EDGE,"E6.5.0.0"),sQuery(id+"F0.wireOp",EDGE,"E6.5.0.1"),sQuery(id+"F0.wireOp",EDGE,"E6.5.0.2"),sQuery(id+"F0.wireOp",EDGE,"E6.5.0.3"),sQuery(id+"F0.wireOp",EDGE,"E6.6.0.0"),sQuery(id+"F0.wireOp",EDGE,"E6.6.0.1"),sQuery(id+"F0.wireOp",EDGE,"E6.6.0.2"),sQuery(id+"F0.wireOp",EDGE,"E6.6.0.3"),sQuery(id+"F0.wireOp",EDGE,"E6.7.0.0"),sQuery(id+"F0.wireOp",EDGE,"E6.7.0.1"),sQuery(id+"F0.wireOp",EDGE,"E6.7.0.2"),sQuery(id+"F0.wireOp",EDGE,"E6.7.0.3"),sQuery(id+"F0.wireOp",EDGE,"E6.8.0.0"),sQuery(id+"F0.wireOp",EDGE,"E6.8.0.1"),sQuery(id+"F0.wireOp",EDGE,"E6.8.0.2"),sQuery(id+"F0.wireOp",EDGE,"E6.8.0.3"),sQuery(id+"F0.wireOp",EDGE,"E6.9.0.0"),sQuery(id+"F0.wireOp",EDGE,"E6.9.0.1"),sQuery(id+"F0.wireOp",EDGE,"E6.9.0.2"),sQuery(id+"F0.wireOp",EDGE,"E6.9.0.3"),sQuery(id+"F0.wireOp",EDGE,"E6.10.0.0"),sQuery(id+"F0.wireOp",EDGE,"E6.10.0.1"),sQuery(id+"F0.wireOp",EDGE,"E6.10.0.2"),sQuery(id+"F0.wireOp",EDGE,"E6.10.0.3"),sQuery(id+"F0.wireOp",EDGE,"E6.11.0.0"),sQuery(id+"F0.wireOp",EDGE,"E6.11.0.1"),sQuery(id+"F0.wireOp",EDGE,"E6.11.0.2"),sQuery(id+"F0.wireOp",EDGE,"E6.11.0.3"),sQuery(id+"F0.wireOp",EDGE,"E6.12.0.0"),sQuery(id+"F0.wireOp",EDGE,"E6.12.0.1"),sQuery(id+"F0.wireOp",EDGE,"E6.12.0.2"),sQuery(id+"F0.wireOp",EDGE,"E6.12.0.3"),sQuery(id+"F0.wireOp",EDGE,"E6.13.0.0"),sQuery(id+"F0.wireOp",EDGE,"E6.13.0.1"),sQuery(id+"F0.wireOp",EDGE,"E6.13.0.2"),sQuery(id+"F0.wireOp",EDGE,"E6.13.0.3"),sQuery(id+"F0.wireOp",EDGE,"E6.14.0.0"),sQuery(id+"F0.wireOp",EDGE,"E6.14.0.1"),sQuery(id+"F0.wireOp",EDGE,"E6.14.0.2"),sQuery(id+"F0.wireOp",EDGE,"E6.14.0.3"),sQuery(id+"F0.wireOp",EDGE,"E6.15.0.0"),sQuery(id+"F0.wireOp",EDGE,"E6.15.0.1"),sQuery(id+"F0.wireOp",EDGE,"E6.15.0.2"),sQuery(id+"F0.wireOp",EDGE,"E6.15.0.3"),sQuery(id+"F0.wireOp",EDGE,"E6.16.0.0"),sQuery(id+"F0.wireOp",EDGE,"E6.16.0.1"),sQuery(id+"F0.wireOp",EDGE,"E6.16.0.2"),sQuery(id+"F0.wireOp",EDGE,"E6.16.0.3"),sQuery(id+"F0.wireOp",EDGE,"E6.17.0.0"),sQuery(id+"F0.wireOp",EDGE,"E6.17.0.1"),sQuery(id+"F0.wireOp",EDGE,"E6.17.0.2"),sQuery(id+"F0.wireOp",EDGE,"E6.17.0.3"),sQuery(id+"F0.wireOp",EDGE,"E6.18.0.0"),sQuery(id+"F0.wireOp",EDGE,"E6.18.0.1"),sQuery(id+"F0.wireOp",EDGE,"E6.18.0.2"),sQuery(id+"F0.wireOp",EDGE,"E6.18.0.3"),sQuery(id+"F0.wireOp",EDGE,"E6.19.0.0"),sQuery(id+"F0.wireOp",EDGE,"E6.19.0.1"),sQuery(id+"F0.wireOp",EDGE,"E6.19.0.2"),sQuery(id+"F0.wireOp",EDGE,"E6.19.0.3"),sQuery(id+"F0.wireOp",EDGE,"E6.20.0.0"),sQuery(id+"F0.wireOp",EDGE,"E6.20.0.1"),sQuery(id+"F0.wireOp",EDGE,"E6.20.0.2"),sQuery(id+"F0.wireOp",EDGE,"E6.20.0.3"),sQuery(id+"F0.wireOp",EDGE,"E6.21.0.0"),sQuery(id+"F0.wireOp",EDGE,"E6.21.0.1"),sQuery(id+"F0.wireOp",EDGE,"E6.21.0.2"),sQuery(id+"F0.wireOp",EDGE,"E6.21.0.3"),sQuery(id+"F0.wireOp",EDGE,"E6.22.0.0"),sQuery(id+"F0.wireOp",EDGE,"E6.22.0.1"),sQuery(id+"F0.wireOp",EDGE,"E6.22.0.2"),sQuery(id+"F0.wireOp",EDGE,"E6.22.0.3"),sQuery(id+"F0.wireOp",EDGE,"E6.23.0.0"),sQuery(id+"F0.wireOp",EDGE,"E6.23.0.1"),sQuery(id+"F0.wireOp",EDGE,"E6.23.0.2"),sQuery(id+"F0.wireOp",EDGE,"E6.23.0.3"),sQuery(id+"F0.wireOp",EDGE,"E6.24.0.0"),sQuery(id+"F0.wireOp",EDGE,"E6.24.0.1"),sQuery(id+"F0.wireOp",EDGE,"E6.24.0.2"),sQuery(id+"F0.wireOp",EDGE,"E6.24.0.3"),sQuery(id+"F0.wireOp",EDGE,"E6.25.0.0"),sQuery(id+"F0.wireOp",EDGE,"E6.25.0.1"),sQuery(id+"F0.wireOp",EDGE,"E6.25.0.2"),sQuery(id+"F0.wireOp",EDGE,"E6.25.0.3"),sQuery(id+"F0.wireOp",EDGE,"E6.26.0.0"),sQuery(id+"F0.wireOp",EDGE,"E6.26.0.1"),sQuery(id+"F0.wireOp",EDGE,"E6.26.0.2"),sQuery(id+"F0.wireOp",EDGE,"E6.26.0.3"),sQuery(id+"F0.wireOp",EDGE,"E6.27.0.0"),sQuery(id+"F0.wireOp",EDGE,"E6.27.0.1"),sQuery(id+"F0.wireOp",EDGE,"E6.27.0.2"),sQuery(id+"F0.wireOp",EDGE,"E6.27.0.3"),sQuery(id+"F0.wireOp",EDGE,"E6.28.0.0"),sQuery(id+"F0.wireOp",EDGE,"E6.28.0.1"),sQuery(id+"F0.wireOp",EDGE,"E6.28.0.2"),sQuery(id+"F0.wireOp",EDGE,"E6.28.0.3"),sQuery(id+"F0.wireOp",EDGE,"E6.29.0.0"),sQuery(id+"F0.wireOp",EDGE,"E6.29.0.1"),sQuery(id+"F0.wireOp",EDGE,"E6.29.0.2"),sQuery(id+"F0.wireOp",EDGE,"E6.29.0.3"),sQuery(id+"F0.wireOp",EDGE,"E6.30.0.0"),sQuery(id+"F0.wireOp",EDGE,"E6.30.0.1"),sQuery(id+"F0.wireOp",EDGE,"E6.30.0.2"),sQuery(id+"F0.wireOp",EDGE,"E6.30.0.3"),sQuery(id+"F0.wireOp",EDGE,"E6.31.0.0"),sQuery(id+"F0.wireOp",EDGE,"E6.31.0.1"),sQuery(id+"F0.wireOp",EDGE,"E6.31.0.2"),sQuery(id+"F0.wireOp",EDGE,"E6.31.0.3"),sQuery(id+"F0.wireOp",EDGE,"E6.32.0.0"),sQuery(id+"F0.wireOp",EDGE,"E6.32.0.1"),sQuery(id+"F0.wireOp",EDGE,"E6.32.0.2"),sQuery(id+"F0.wireOp",EDGE,"E6.32.0.3"),sQuery(id+"F0.wireOp",EDGE,"E6.33.0.0"),sQuery(id+"F0.wireOp",EDGE,"E6.33.0.1"),sQuery(id+"F0.wireOp",EDGE,"E6.33.0.2"),sQuery(id+"F0.wireOp",EDGE,"E6.33.0.3"),sQuery(id+"F0.wireOp",EDGE,"E6.34.0.0"),sQuery(id+"F0.wireOp",EDGE,"E6.34.0.1"),sQuery(id+"F0.wireOp",EDGE,"E6.34.0.2"),sQuery(id+"F0.wireOp",EDGE,"E6.34.0.3"),sQuery(id+"F0.wireOp",EDGE,"E6.35.0.0"),sQuery(id+"F0.wireOp",EDGE,"E6.35.0.1"),sQuery(id+"F0.wireOp",EDGE,"E6.35.0.2"),sQuery(id+"F0.wireOp",EDGE,"E6.35.0.3"),sQuery(id+"F0.wireOp",EDGE,"E6.36.0.0"),sQuery(id+"F0.wireOp",EDGE,"E6.36.0.1"),sQuery(id+"F0.wireOp",EDGE,"E6.36.0.2"),sQuery(id+"F0.wireOp",EDGE,"E6.36.0.3"),sQuery(id+"F0.wireOp",EDGE,"E6.37.0.0"),sQuery(id+"F0.wireOp",EDGE,"E6.37.0.1"),sQuery(id+"F0.wireOp",EDGE,"E6.37.0.2"),sQuery(id+"F0.wireOp",EDGE,"E6.37.0.3"),sQuery(id+"F0.wireOp",EDGE,"E6.38.0.0"),sQuery(id+"F0.wireOp",EDGE,"E6.38.0.1"),sQuery(id+"F0.wireOp",EDGE,"E6.38.0.2"),sQuery(id+"F0.wireOp",EDGE,"E6.38.0.3"),sQuery(id+"F0.wireOp",EDGE,"E6.39.0.0"),sQuery(id+"F0.wireOp",EDGE,"E6.39.0.1"),sQuery(id+"F0.wireOp",EDGE,"E6.39.0.2"),sQuery(id+"F0.wireOp",EDGE,"E6.39.0.3"),sQuery(id+"F0.wireOp",EDGE,"E6.40.0.0"),sQuery(id+"F0.wireOp",EDGE,"E6.40.0.1"),sQuery(id+"F0.wireOp",EDGE,"E6.40.0.2"),sQuery(id+"F0.wireOp",EDGE,"E6.40.0.3"),sQuery(id+"F0.wireOp",EDGE,"E6.41.0.0"),sQuery(id+"F0.wireOp",EDGE,"E6.41.0.1"),sQuery(id+"F0.wireOp",EDGE,"E6.41.0.2"),sQuery(id+"F0.wireOp",EDGE,"E6.41.0.3"),sQuery(id+"F0.wireOp",EDGE,"E6.42.0.0"),sQuery(id+"F0.wireOp",EDGE,"E6.42.0.1"),sQuery(id+"F0.wireOp",EDGE,"E6.42.0.2"),sQuery(id+"F0.wireOp",EDGE,"E6.42.0.3"),sQuery(id+"F0.wireOp",EDGE,"E6.43.0.0"),sQuery(id+"F0.wireOp",EDGE,"E6.43.0.1"),sQuery(id+"F0.wireOp",EDGE,"E6.43.0.2"),sQuery(id+"F0.wireOp",EDGE,"E6.43.0.3"),sQuery(id+"F0.wireOp",EDGE,"E6.44.0.0"),sQuery(id+"F0.wireOp",EDGE,"E6.44.0.1"),sQuery(id+"F0.wireOp",EDGE,"E6.44.0.2"),sQuery(id+"F0.wireOp",EDGE,"E6.44.0.3"),sQuery(id+"F0.wireOp",EDGE,"E6.45.0.0"),sQuery(id+"F0.wireOp",EDGE,"E6.45.0.1"),sQuery(id+"F0.wireOp",EDGE,"E6.45.0.2"),sQuery(id+"F0.wireOp",EDGE,"E6.45.0.3"),sQuery(id+"F0.wireOp",EDGE,"E6.46.0.0"),sQuery(id+"F0.wireOp",EDGE,"E6.46.0.1"),sQuery(id+"F0.wireOp",EDGE,"E6.46.0.2"),sQuery(id+"F0.wireOp",EDGE,"E6.46.0.3"),sQuery(id+"F0.wireOp",EDGE,"E6.47.0.0"),sQuery(id+"F0.wireOp",EDGE,"E6.47.0.1"),sQuery(id+"F0.wireOp",EDGE,"E6.47.0.2"),sQuery(id+"F0.wireOp",EDGE,"E6.47.0.3"),sQuery(id+"F0.wireOp",EDGE,"E6.48.0.0"),sQuery(id+"F0.wireOp",EDGE,"E6.48.0.1"),sQuery(id+"F0.wireOp",EDGE,"E6.48.0.2"),sQuery(id+"F0.wireOp",EDGE,"E6.48.0.3"),sQuery(id+"F0.wireOp",EDGE,"E6.49.0.0"),sQuery(id+"F0.wireOp",EDGE,"E6.49.0.1"),sQuery(id+"F0.wireOp",EDGE,"E7"),sQuery(id+"F0.wireOp",EDGE,"E8"),sQuery(id+"F0.wireOp",EDGE,"E9"),sQuery(id+"F0.wireOp",EDGE,"E10"),sQuery(id+"F0.wireOp",EDGE,"E11"),sQuery(id+"F0.wireOp",EDGE,"E12"),sQuery(id+"F0.wireOp",EDGE,"E13"),sQuery(id+"F0.wireOp",EDGE,"E14"),sQuery(id+"F0.wireOp",EDGE,"E15"),sQuery(id+"F0.wireOp",EDGE,"E16"),sQuery(id+"F0.wireOp",EDGE,"E17"),sQuery(id+"F0.wireOp",EDGE,"E18"),sQuery(id+"F0.wireOp",EDGE,"E19"),sQuery(id+"F0.wireOp",EDGE,"E20"),sQuery(id+"F0.wireOp",EDGE,"E21"),sQuery(id+"F0.wireOp",EDGE,"E22"),sQuery(id+"F0.wireOp",EDGE,"E23"),sQuery(id+"F0.wireOp",EDGE,"E24"),sQuery(id+"F0.wireOp",EDGE,"E25"),sQuery(id+"F0.wireOp",EDGE,"E26"),sQuery(id+"F0.wireOp",EDGE,"E27"),sQuery(id+"F0.wireOp",EDGE,"E28"),sQuery(id+"F0.wireOp",EDGE,"E29"),sQuery(id+"F0.wireOp",EDGE,"E30"),sQuery(id+"F0.wireOp",EDGE,"etuK1Xr9-J4i1-57WR-O4AE-Va2F9wOQP8k6"),sQuery(id+"F0.wireOp",EDGE,"9MBbQYz1-y2p6-nwSH-8az1-lH37U9JjGGAZ")])]}),"instanceName":"1"});
            transform(context, id + "F3", {"entities" : qUnion([Q0]), "transformType" : TransformType.TRANSLATION_3D, "dx" : 0 * mm, "dy" : 70.26 * mm, "dz" : 0 * mm, "makeCopy" : true});
        }
        {
            var Q0;
            Q0=makeQuery(id+"F2.opPattern","COPY",BODY,{"derivedFrom":makeQuery(id+"F1.opExtrude","SWEPT_BODY",BODY,{"disambiguationData":[OSD([sQuery(id+"F0.wireOp",EDGE,"E1.bottom"),sQuery(id+"F0.wireOp",EDGE,"E1.left"),sQuery(id+"F0.wireOp",EDGE,"E1.right"),sQuery(id+"F0.wireOp",EDGE,"E2"),sQuery(id+"F0.wireOp",EDGE,"E3.1.0.0"),sQuery(id+"F0.wireOp",EDGE,"E3.1.0.1"),sQuery(id+"F0.wireOp",EDGE,"E3.1.0.2"),sQuery(id+"F0.wireOp",EDGE,"E3.1.0.3"),sQuery(id+"F0.wireOp",EDGE,"E3.2.0.0"),sQuery(id+"F0.wireOp",EDGE,"E3.2.0.1"),sQuery(id+"F0.wireOp",EDGE,"E3.2.0.2"),sQuery(id+"F0.wireOp",EDGE,"E3.2.0.3"),sQuery(id+"F0.wireOp",EDGE,"E3.3.0.0"),sQuery(id+"F0.wireOp",EDGE,"E3.3.0.1"),sQuery(id+"F0.wireOp",EDGE,"E3.3.0.2"),sQuery(id+"F0.wireOp",EDGE,"E3.3.0.3"),sQuery(id+"F0.wireOp",EDGE,"E3.4.0.0"),sQuery(id+"F0.wireOp",EDGE,"E3.4.0.1"),sQuery(id+"F0.wireOp",EDGE,"E3.4.0.2"),sQuery(id+"F0.wireOp",EDGE,"E3.4.0.3"),sQuery(id+"F0.wireOp",EDGE,"E3.5.0.0"),sQuery(id+"F0.wireOp",EDGE,"E3.5.0.1"),sQuery(id+"F0.wireOp",EDGE,"E3.5.0.2"),sQuery(id+"F0.wireOp",EDGE,"E3.5.0.3"),sQuery(id+"F0.wireOp",EDGE,"E3.6.0.0"),sQuery(id+"F0.wireOp",EDGE,"E3.6.0.1"),sQuery(id+"F0.wireOp",EDGE,"E3.6.0.2"),sQuery(id+"F0.wireOp",EDGE,"E3.6.0.3"),sQuery(id+"F0.wireOp",EDGE,"E3.7.0.0"),sQuery(id+"F0.wireOp",EDGE,"E3.7.0.1"),sQuery(id+"F0.wireOp",EDGE,"E3.7.0.2"),sQuery(id+"F0.wireOp",EDGE,"E3.7.0.3"),sQuery(id+"F0.wireOp",EDGE,"E3.8.0.0"),sQuery(id+"F0.wireOp",EDGE,"E3.8.0.1"),sQuery(id+"F0.wireOp",EDGE,"E3.8.0.2"),sQuery(id+"F0.wireOp",EDGE,"E3.8.0.3"),sQuery(id+"F0.wireOp",EDGE,"E3.9.0.0"),sQuery(id+"F0.wireOp",EDGE,"E3.9.0.1"),sQuery(id+"F0.wireOp",EDGE,"E3.9.0.2"),sQuery(id+"F0.wireOp",EDGE,"E3.9.0.3"),sQuery(id+"F0.wireOp",EDGE,"E3.10.0.0"),sQuery(id+"F0.wireOp",EDGE,"E3.10.0.1"),sQuery(id+"F0.wireOp",EDGE,"E3.10.0.2"),sQuery(id+"F0.wireOp",EDGE,"E3.10.0.3"),sQuery(id+"F0.wireOp",EDGE,"E3.11.0.0"),sQuery(id+"F0.wireOp",EDGE,"E3.11.0.1"),sQuery(id+"F0.wireOp",EDGE,"E3.11.0.2"),sQuery(id+"F0.wireOp",EDGE,"E3.11.0.3"),sQuery(id+"F0.wireOp",EDGE,"E3.12.0.0"),sQuery(id+"F0.wireOp",EDGE,"E3.12.0.1"),sQuery(id+"F0.wireOp",EDGE,"E3.12.0.2"),sQuery(id+"F0.wireOp",EDGE,"E3.12.0.3"),sQuery(id+"F0.wireOp",EDGE,"E3.13.0.0"),sQuery(id+"F0.wireOp",EDGE,"E3.13.0.1"),sQuery(id+"F0.wireOp",EDGE,"E3.13.0.2"),sQuery(id+"F0.wireOp",EDGE,"E3.13.0.3"),sQuery(id+"F0.wireOp",EDGE,"E3.14.0.0"),sQuery(id+"F0.wireOp",EDGE,"E3.14.0.1"),sQuery(id+"F0.wireOp",EDGE,"E3.14.0.2"),sQuery(id+"F0.wireOp",EDGE,"E3.14.0.3"),sQuery(id+"F0.wireOp",EDGE,"E3.15.0.0"),sQuery(id+"F0.wireOp",EDGE,"E3.15.0.1"),sQuery(id+"F0.wireOp",EDGE,"E3.15.0.2"),sQuery(id+"F0.wireOp",EDGE,"E3.15.0.3"),sQuery(id+"F0.wireOp",EDGE,"E3.16.0.0"),sQuery(id+"F0.wireOp",EDGE,"E3.16.0.1"),sQuery(id+"F0.wireOp",EDGE,"E3.16.0.2"),sQuery(id+"F0.wireOp",EDGE,"E3.16.0.3"),sQuery(id+"F0.wireOp",EDGE,"E3.17.0.0"),sQuery(id+"F0.wireOp",EDGE,"E3.17.0.1"),sQuery(id+"F0.wireOp",EDGE,"E3.17.0.2"),sQuery(id+"F0.wireOp",EDGE,"E3.17.0.3"),sQuery(id+"F0.wireOp",EDGE,"E3.18.0.0"),sQuery(id+"F0.wireOp",EDGE,"E3.18.0.1"),sQuery(id+"F0.wireOp",EDGE,"E3.18.0.2"),sQuery(id+"F0.wireOp",EDGE,"E3.18.0.3"),sQuery(id+"F0.wireOp",EDGE,"E3.19.0.0"),sQuery(id+"F0.wireOp",EDGE,"E3.19.0.1"),sQuery(id+"F0.wireOp",EDGE,"E3.19.0.2"),sQuery(id+"F0.wireOp",EDGE,"E3.19.0.3"),sQuery(id+"F0.wireOp",EDGE,"E3.20.0.0"),sQuery(id+"F0.wireOp",EDGE,"E3.20.0.1"),sQuery(id+"F0.wireOp",EDGE,"E3.20.0.2"),sQuery(id+"F0.wireOp",EDGE,"E3.20.0.3"),sQuery(id+"F0.wireOp",EDGE,"E3.21.0.0"),sQuery(id+"F0.wireOp",EDGE,"E3.21.0.1"),sQuery(id+"F0.wireOp",EDGE,"E3.21.0.2"),sQuery(id+"F0.wireOp",EDGE,"E3.21.0.3"),sQuery(id+"F0.wireOp",EDGE,"E3.22.0.0"),sQuery(id+"F0.wireOp",EDGE,"E3.22.0.1"),sQuery(id+"F0.wireOp",EDGE,"E3.22.0.2"),sQuery(id+"F0.wireOp",EDGE,"E3.22.0.3"),sQuery(id+"F0.wireOp",EDGE,"E3.23.0.0"),sQuery(id+"F0.wireOp",EDGE,"E3.23.0.1"),sQuery(id+"F0.wireOp",EDGE,"E3.23.0.2"),sQuery(id+"F0.wireOp",EDGE,"E3.23.0.3"),sQuery(id+"F0.wireOp",EDGE,"E3.24.0.0"),sQuery(id+"F0.wireOp",EDGE,"E3.24.0.1"),sQuery(id+"F0.wireOp",EDGE,"E3.24.0.2"),sQuery(id+"F0.wireOp",EDGE,"E3.24.0.3"),sQuery(id+"F0.wireOp",EDGE,"E3.25.0.0"),sQuery(id+"F0.wireOp",EDGE,"E3.25.0.1"),sQuery(id+"F0.wireOp",EDGE,"E3.25.0.2"),sQuery(id+"F0.wireOp",EDGE,"E3.25.0.3"),sQuery(id+"F0.wireOp",EDGE,"E3.26.0.0"),sQuery(id+"F0.wireOp",EDGE,"E3.26.0.1"),sQuery(id+"F0.wireOp",EDGE,"E3.26.0.2"),sQuery(id+"F0.wireOp",EDGE,"E3.26.0.3"),sQuery(id+"F0.wireOp",EDGE,"E3.27.0.0"),sQuery(id+"F0.wireOp",EDGE,"E3.27.0.1"),sQuery(id+"F0.wireOp",EDGE,"E3.27.0.2"),sQuery(id+"F0.wireOp",EDGE,"E3.27.0.3"),sQuery(id+"F0.wireOp",EDGE,"E3.28.0.0"),sQuery(id+"F0.wireOp",EDGE,"E3.28.0.1"),sQuery(id+"F0.wireOp",EDGE,"E3.28.0.2"),sQuery(id+"F0.wireOp",EDGE,"E3.28.0.3"),sQuery(id+"F0.wireOp",EDGE,"E3.29.0.0"),sQuery(id+"F0.wireOp",EDGE,"E3.29.0.1"),sQuery(id+"F0.wireOp",EDGE,"E3.29.0.2"),sQuery(id+"F0.wireOp",EDGE,"E3.29.0.3"),sQuery(id+"F0.wireOp",EDGE,"E3.30.0.0"),sQuery(id+"F0.wireOp",EDGE,"E3.30.0.1"),sQuery(id+"F0.wireOp",EDGE,"E3.30.0.2"),sQuery(id+"F0.wireOp",EDGE,"E3.30.0.3"),sQuery(id+"F0.wireOp",EDGE,"E3.31.0.0"),sQuery(id+"F0.wireOp",EDGE,"E3.31.0.1"),sQuery(id+"F0.wireOp",EDGE,"E3.31.0.2"),sQuery(id+"F0.wireOp",EDGE,"E3.31.0.3"),sQuery(id+"F0.wireOp",EDGE,"E3.32.0.0"),sQuery(id+"F0.wireOp",EDGE,"E3.32.0.1"),sQuery(id+"F0.wireOp",EDGE,"E3.32.0.2"),sQuery(id+"F0.wireOp",EDGE,"E3.32.0.3"),sQuery(id+"F0.wireOp",EDGE,"E3.33.0.0"),sQuery(id+"F0.wireOp",EDGE,"E3.33.0.1"),sQuery(id+"F0.wireOp",EDGE,"E3.33.0.2"),sQuery(id+"F0.wireOp",EDGE,"E3.33.0.3"),sQuery(id+"F0.wireOp",EDGE,"E3.34.0.0"),sQuery(id+"F0.wireOp",EDGE,"E3.34.0.1"),sQuery(id+"F0.wireOp",EDGE,"E3.34.0.2"),sQuery(id+"F0.wireOp",EDGE,"E3.34.0.3"),sQuery(id+"F0.wireOp",EDGE,"E3.35.0.0"),sQuery(id+"F0.wireOp",EDGE,"E3.35.0.1"),sQuery(id+"F0.wireOp",EDGE,"E3.35.0.2"),sQuery(id+"F0.wireOp",EDGE,"E3.35.0.3"),sQuery(id+"F0.wireOp",EDGE,"E3.36.0.0"),sQuery(id+"F0.wireOp",EDGE,"E3.36.0.1"),sQuery(id+"F0.wireOp",EDGE,"E3.36.0.2"),sQuery(id+"F0.wireOp",EDGE,"E3.36.0.3"),sQuery(id+"F0.wireOp",EDGE,"E3.37.0.0"),sQuery(id+"F0.wireOp",EDGE,"E3.37.0.1"),sQuery(id+"F0.wireOp",EDGE,"E3.37.0.2"),sQuery(id+"F0.wireOp",EDGE,"E3.37.0.3"),sQuery(id+"F0.wireOp",EDGE,"E3.38.0.0"),sQuery(id+"F0.wireOp",EDGE,"E3.38.0.1"),sQuery(id+"F0.wireOp",EDGE,"E3.38.0.2"),sQuery(id+"F0.wireOp",EDGE,"E3.38.0.3"),sQuery(id+"F0.wireOp",EDGE,"E3.39.0.0"),sQuery(id+"F0.wireOp",EDGE,"E3.39.0.1"),sQuery(id+"F0.wireOp",EDGE,"E3.39.0.2"),sQuery(id+"F0.wireOp",EDGE,"E3.39.0.3"),sQuery(id+"F0.wireOp",EDGE,"E3.40.0.0"),sQuery(id+"F0.wireOp",EDGE,"E3.40.0.1"),sQuery(id+"F0.wireOp",EDGE,"E3.40.0.2"),sQuery(id+"F0.wireOp",EDGE,"E3.40.0.3"),sQuery(id+"F0.wireOp",EDGE,"E3.41.0.0"),sQuery(id+"F0.wireOp",EDGE,"E3.41.0.1"),sQuery(id+"F0.wireOp",EDGE,"E3.41.0.2"),sQuery(id+"F0.wireOp",EDGE,"E3.41.0.3"),sQuery(id+"F0.wireOp",EDGE,"E3.42.0.0"),sQuery(id+"F0.wireOp",EDGE,"E3.42.0.1"),sQuery(id+"F0.wireOp",EDGE,"E3.42.0.2"),sQuery(id+"F0.wireOp",EDGE,"E3.42.0.3"),sQuery(id+"F0.wireOp",EDGE,"E3.43.0.0"),sQuery(id+"F0.wireOp",EDGE,"E3.43.0.1"),sQuery(id+"F0.wireOp",EDGE,"E3.43.0.2"),sQuery(id+"F0.wireOp",EDGE,"E3.43.0.3"),sQuery(id+"F0.wireOp",EDGE,"E3.44.0.0"),sQuery(id+"F0.wireOp",EDGE,"E3.44.0.1"),sQuery(id+"F0.wireOp",EDGE,"E3.44.0.2"),sQuery(id+"F0.wireOp",EDGE,"E3.44.0.3"),sQuery(id+"F0.wireOp",EDGE,"E3.45.0.0"),sQuery(id+"F0.wireOp",EDGE,"E3.45.0.1"),sQuery(id+"F0.wireOp",EDGE,"E3.45.0.2"),sQuery(id+"F0.wireOp",EDGE,"E3.45.0.3"),sQuery(id+"F0.wireOp",EDGE,"E3.46.0.0"),sQuery(id+"F0.wireOp",EDGE,"E3.46.0.1"),sQuery(id+"F0.wireOp",EDGE,"E3.46.0.2"),sQuery(id+"F0.wireOp",EDGE,"E3.46.0.3"),sQuery(id+"F0.wireOp",EDGE,"E3.47.0.0"),sQuery(id+"F0.wireOp",EDGE,"E3.47.0.1"),sQuery(id+"F0.wireOp",EDGE,"E3.47.0.2"),sQuery(id+"F0.wireOp",EDGE,"E3.47.0.3"),sQuery(id+"F0.wireOp",EDGE,"E3.48.0.0"),sQuery(id+"F0.wireOp",EDGE,"E3.48.0.1"),sQuery(id+"F0.wireOp",EDGE,"E3.48.0.2"),sQuery(id+"F0.wireOp",EDGE,"E3.48.0.3"),sQuery(id+"F0.wireOp",EDGE,"E3.49.0.0"),sQuery(id+"F0.wireOp",EDGE,"E3.49.0.1"),sQuery(id+"F0.wireOp",EDGE,"E3.49.0.2"),sQuery(id+"F0.wireOp",EDGE,"E4.bottom"),sQuery(id+"F0.wireOp",EDGE,"E4.left"),sQuery(id+"F0.wireOp",EDGE,"E4.right"),sQuery(id+"F0.wireOp",EDGE,"E5"),sQuery(id+"F0.wireOp",EDGE,"E6.1.0.0"),sQuery(id+"F0.wireOp",EDGE,"E6.1.0.1"),sQuery(id+"F0.wireOp",EDGE,"E6.1.0.2"),sQuery(id+"F0.wireOp",EDGE,"E6.1.0.3"),sQuery(id+"F0.wireOp",EDGE,"E6.2.0.0"),sQuery(id+"F0.wireOp",EDGE,"E6.2.0.1"),sQuery(id+"F0.wireOp",EDGE,"E6.2.0.2"),sQuery(id+"F0.wireOp",EDGE,"E6.2.0.3"),sQuery(id+"F0.wireOp",EDGE,"E6.3.0.0"),sQuery(id+"F0.wireOp",EDGE,"E6.3.0.1"),sQuery(id+"F0.wireOp",EDGE,"E6.3.0.2"),sQuery(id+"F0.wireOp",EDGE,"E6.3.0.3"),sQuery(id+"F0.wireOp",EDGE,"E6.4.0.0"),sQuery(id+"F0.wireOp",EDGE,"E6.4.0.1"),sQuery(id+"F0.wireOp",EDGE,"E6.4.0.2"),sQuery(id+"F0.wireOp",EDGE,"E6.4.0.3"),sQuery(id+"F0.wireOp",EDGE,"E6.5.0.0"),sQuery(id+"F0.wireOp",EDGE,"E6.5.0.1"),sQuery(id+"F0.wireOp",EDGE,"E6.5.0.2"),sQuery(id+"F0.wireOp",EDGE,"E6.5.0.3"),sQuery(id+"F0.wireOp",EDGE,"E6.6.0.0"),sQuery(id+"F0.wireOp",EDGE,"E6.6.0.1"),sQuery(id+"F0.wireOp",EDGE,"E6.6.0.2"),sQuery(id+"F0.wireOp",EDGE,"E6.6.0.3"),sQuery(id+"F0.wireOp",EDGE,"E6.7.0.0"),sQuery(id+"F0.wireOp",EDGE,"E6.7.0.1"),sQuery(id+"F0.wireOp",EDGE,"E6.7.0.2"),sQuery(id+"F0.wireOp",EDGE,"E6.7.0.3"),sQuery(id+"F0.wireOp",EDGE,"E6.8.0.0"),sQuery(id+"F0.wireOp",EDGE,"E6.8.0.1"),sQuery(id+"F0.wireOp",EDGE,"E6.8.0.2"),sQuery(id+"F0.wireOp",EDGE,"E6.8.0.3"),sQuery(id+"F0.wireOp",EDGE,"E6.9.0.0"),sQuery(id+"F0.wireOp",EDGE,"E6.9.0.1"),sQuery(id+"F0.wireOp",EDGE,"E6.9.0.2"),sQuery(id+"F0.wireOp",EDGE,"E6.9.0.3"),sQuery(id+"F0.wireOp",EDGE,"E6.10.0.0"),sQuery(id+"F0.wireOp",EDGE,"E6.10.0.1"),sQuery(id+"F0.wireOp",EDGE,"E6.10.0.2"),sQuery(id+"F0.wireOp",EDGE,"E6.10.0.3"),sQuery(id+"F0.wireOp",EDGE,"E6.11.0.0"),sQuery(id+"F0.wireOp",EDGE,"E6.11.0.1"),sQuery(id+"F0.wireOp",EDGE,"E6.11.0.2"),sQuery(id+"F0.wireOp",EDGE,"E6.11.0.3"),sQuery(id+"F0.wireOp",EDGE,"E6.12.0.0"),sQuery(id+"F0.wireOp",EDGE,"E6.12.0.1"),sQuery(id+"F0.wireOp",EDGE,"E6.12.0.2"),sQuery(id+"F0.wireOp",EDGE,"E6.12.0.3"),sQuery(id+"F0.wireOp",EDGE,"E6.13.0.0"),sQuery(id+"F0.wireOp",EDGE,"E6.13.0.1"),sQuery(id+"F0.wireOp",EDGE,"E6.13.0.2"),sQuery(id+"F0.wireOp",EDGE,"E6.13.0.3"),sQuery(id+"F0.wireOp",EDGE,"E6.14.0.0"),sQuery(id+"F0.wireOp",EDGE,"E6.14.0.1"),sQuery(id+"F0.wireOp",EDGE,"E6.14.0.2"),sQuery(id+"F0.wireOp",EDGE,"E6.14.0.3"),sQuery(id+"F0.wireOp",EDGE,"E6.15.0.0"),sQuery(id+"F0.wireOp",EDGE,"E6.15.0.1"),sQuery(id+"F0.wireOp",EDGE,"E6.15.0.2"),sQuery(id+"F0.wireOp",EDGE,"E6.15.0.3"),sQuery(id+"F0.wireOp",EDGE,"E6.16.0.0"),sQuery(id+"F0.wireOp",EDGE,"E6.16.0.1"),sQuery(id+"F0.wireOp",EDGE,"E6.16.0.2"),sQuery(id+"F0.wireOp",EDGE,"E6.16.0.3"),sQuery(id+"F0.wireOp",EDGE,"E6.17.0.0"),sQuery(id+"F0.wireOp",EDGE,"E6.17.0.1"),sQuery(id+"F0.wireOp",EDGE,"E6.17.0.2"),sQuery(id+"F0.wireOp",EDGE,"E6.17.0.3"),sQuery(id+"F0.wireOp",EDGE,"E6.18.0.0"),sQuery(id+"F0.wireOp",EDGE,"E6.18.0.1"),sQuery(id+"F0.wireOp",EDGE,"E6.18.0.2"),sQuery(id+"F0.wireOp",EDGE,"E6.18.0.3"),sQuery(id+"F0.wireOp",EDGE,"E6.19.0.0"),sQuery(id+"F0.wireOp",EDGE,"E6.19.0.1"),sQuery(id+"F0.wireOp",EDGE,"E6.19.0.2"),sQuery(id+"F0.wireOp",EDGE,"E6.19.0.3"),sQuery(id+"F0.wireOp",EDGE,"E6.20.0.0"),sQuery(id+"F0.wireOp",EDGE,"E6.20.0.1"),sQuery(id+"F0.wireOp",EDGE,"E6.20.0.2"),sQuery(id+"F0.wireOp",EDGE,"E6.20.0.3"),sQuery(id+"F0.wireOp",EDGE,"E6.21.0.0"),sQuery(id+"F0.wireOp",EDGE,"E6.21.0.1"),sQuery(id+"F0.wireOp",EDGE,"E6.21.0.2"),sQuery(id+"F0.wireOp",EDGE,"E6.21.0.3"),sQuery(id+"F0.wireOp",EDGE,"E6.22.0.0"),sQuery(id+"F0.wireOp",EDGE,"E6.22.0.1"),sQuery(id+"F0.wireOp",EDGE,"E6.22.0.2"),sQuery(id+"F0.wireOp",EDGE,"E6.22.0.3"),sQuery(id+"F0.wireOp",EDGE,"E6.23.0.0"),sQuery(id+"F0.wireOp",EDGE,"E6.23.0.1"),sQuery(id+"F0.wireOp",EDGE,"E6.23.0.2"),sQuery(id+"F0.wireOp",EDGE,"E6.23.0.3"),sQuery(id+"F0.wireOp",EDGE,"E6.24.0.0"),sQuery(id+"F0.wireOp",EDGE,"E6.24.0.1"),sQuery(id+"F0.wireOp",EDGE,"E6.24.0.2"),sQuery(id+"F0.wireOp",EDGE,"E6.24.0.3"),sQuery(id+"F0.wireOp",EDGE,"E6.25.0.0"),sQuery(id+"F0.wireOp",EDGE,"E6.25.0.1"),sQuery(id+"F0.wireOp",EDGE,"E6.25.0.2"),sQuery(id+"F0.wireOp",EDGE,"E6.25.0.3"),sQuery(id+"F0.wireOp",EDGE,"E6.26.0.0"),sQuery(id+"F0.wireOp",EDGE,"E6.26.0.1"),sQuery(id+"F0.wireOp",EDGE,"E6.26.0.2"),sQuery(id+"F0.wireOp",EDGE,"E6.26.0.3"),sQuery(id+"F0.wireOp",EDGE,"E6.27.0.0"),sQuery(id+"F0.wireOp",EDGE,"E6.27.0.1"),sQuery(id+"F0.wireOp",EDGE,"E6.27.0.2"),sQuery(id+"F0.wireOp",EDGE,"E6.27.0.3"),sQuery(id+"F0.wireOp",EDGE,"E6.28.0.0"),sQuery(id+"F0.wireOp",EDGE,"E6.28.0.1"),sQuery(id+"F0.wireOp",EDGE,"E6.28.0.2"),sQuery(id+"F0.wireOp",EDGE,"E6.28.0.3"),sQuery(id+"F0.wireOp",EDGE,"E6.29.0.0"),sQuery(id+"F0.wireOp",EDGE,"E6.29.0.1"),sQuery(id+"F0.wireOp",EDGE,"E6.29.0.2"),sQuery(id+"F0.wireOp",EDGE,"E6.29.0.3"),sQuery(id+"F0.wireOp",EDGE,"E6.30.0.0"),sQuery(id+"F0.wireOp",EDGE,"E6.30.0.1"),sQuery(id+"F0.wireOp",EDGE,"E6.30.0.2"),sQuery(id+"F0.wireOp",EDGE,"E6.30.0.3"),sQuery(id+"F0.wireOp",EDGE,"E6.31.0.0"),sQuery(id+"F0.wireOp",EDGE,"E6.31.0.1"),sQuery(id+"F0.wireOp",EDGE,"E6.31.0.2"),sQuery(id+"F0.wireOp",EDGE,"E6.31.0.3"),sQuery(id+"F0.wireOp",EDGE,"E6.32.0.0"),sQuery(id+"F0.wireOp",EDGE,"E6.32.0.1"),sQuery(id+"F0.wireOp",EDGE,"E6.32.0.2"),sQuery(id+"F0.wireOp",EDGE,"E6.32.0.3"),sQuery(id+"F0.wireOp",EDGE,"E6.33.0.0"),sQuery(id+"F0.wireOp",EDGE,"E6.33.0.1"),sQuery(id+"F0.wireOp",EDGE,"E6.33.0.2"),sQuery(id+"F0.wireOp",EDGE,"E6.33.0.3"),sQuery(id+"F0.wireOp",EDGE,"E6.34.0.0"),sQuery(id+"F0.wireOp",EDGE,"E6.34.0.1"),sQuery(id+"F0.wireOp",EDGE,"E6.34.0.2"),sQuery(id+"F0.wireOp",EDGE,"E6.34.0.3"),sQuery(id+"F0.wireOp",EDGE,"E6.35.0.0"),sQuery(id+"F0.wireOp",EDGE,"E6.35.0.1"),sQuery(id+"F0.wireOp",EDGE,"E6.35.0.2"),sQuery(id+"F0.wireOp",EDGE,"E6.35.0.3"),sQuery(id+"F0.wireOp",EDGE,"E6.36.0.0"),sQuery(id+"F0.wireOp",EDGE,"E6.36.0.1"),sQuery(id+"F0.wireOp",EDGE,"E6.36.0.2"),sQuery(id+"F0.wireOp",EDGE,"E6.36.0.3"),sQuery(id+"F0.wireOp",EDGE,"E6.37.0.0"),sQuery(id+"F0.wireOp",EDGE,"E6.37.0.1"),sQuery(id+"F0.wireOp",EDGE,"E6.37.0.2"),sQuery(id+"F0.wireOp",EDGE,"E6.37.0.3"),sQuery(id+"F0.wireOp",EDGE,"E6.38.0.0"),sQuery(id+"F0.wireOp",EDGE,"E6.38.0.1"),sQuery(id+"F0.wireOp",EDGE,"E6.38.0.2"),sQuery(id+"F0.wireOp",EDGE,"E6.38.0.3"),sQuery(id+"F0.wireOp",EDGE,"E6.39.0.0"),sQuery(id+"F0.wireOp",EDGE,"E6.39.0.1"),sQuery(id+"F0.wireOp",EDGE,"E6.39.0.2"),sQuery(id+"F0.wireOp",EDGE,"E6.39.0.3"),sQuery(id+"F0.wireOp",EDGE,"E6.40.0.0"),sQuery(id+"F0.wireOp",EDGE,"E6.40.0.1"),sQuery(id+"F0.wireOp",EDGE,"E6.40.0.2"),sQuery(id+"F0.wireOp",EDGE,"E6.40.0.3"),sQuery(id+"F0.wireOp",EDGE,"E6.41.0.0"),sQuery(id+"F0.wireOp",EDGE,"E6.41.0.1"),sQuery(id+"F0.wireOp",EDGE,"E6.41.0.2"),sQuery(id+"F0.wireOp",EDGE,"E6.41.0.3"),sQuery(id+"F0.wireOp",EDGE,"E6.42.0.0"),sQuery(id+"F0.wireOp",EDGE,"E6.42.0.1"),sQuery(id+"F0.wireOp",EDGE,"E6.42.0.2"),sQuery(id+"F0.wireOp",EDGE,"E6.42.0.3"),sQuery(id+"F0.wireOp",EDGE,"E6.43.0.0"),sQuery(id+"F0.wireOp",EDGE,"E6.43.0.1"),sQuery(id+"F0.wireOp",EDGE,"E6.43.0.2"),sQuery(id+"F0.wireOp",EDGE,"E6.43.0.3"),sQuery(id+"F0.wireOp",EDGE,"E6.44.0.0"),sQuery(id+"F0.wireOp",EDGE,"E6.44.0.1"),sQuery(id+"F0.wireOp",EDGE,"E6.44.0.2"),sQuery(id+"F0.wireOp",EDGE,"E6.44.0.3"),sQuery(id+"F0.wireOp",EDGE,"E6.45.0.0"),sQuery(id+"F0.wireOp",EDGE,"E6.45.0.1"),sQuery(id+"F0.wireOp",EDGE,"E6.45.0.2"),sQuery(id+"F0.wireOp",EDGE,"E6.45.0.3"),sQuery(id+"F0.wireOp",EDGE,"E6.46.0.0"),sQuery(id+"F0.wireOp",EDGE,"E6.46.0.1"),sQuery(id+"F0.wireOp",EDGE,"E6.46.0.2"),sQuery(id+"F0.wireOp",EDGE,"E6.46.0.3"),sQuery(id+"F0.wireOp",EDGE,"E6.47.0.0"),sQuery(id+"F0.wireOp",EDGE,"E6.47.0.1"),sQuery(id+"F0.wireOp",EDGE,"E6.47.0.2"),sQuery(id+"F0.wireOp",EDGE,"E6.47.0.3"),sQuery(id+"F0.wireOp",EDGE,"E6.48.0.0"),sQuery(id+"F0.wireOp",EDGE,"E6.48.0.1"),sQuery(id+"F0.wireOp",EDGE,"E6.48.0.2"),sQuery(id+"F0.wireOp",EDGE,"E6.48.0.3"),sQuery(id+"F0.wireOp",EDGE,"E6.49.0.0"),sQuery(id+"F0.wireOp",EDGE,"E6.49.0.1"),sQuery(id+"F0.wireOp",EDGE,"E7"),sQuery(id+"F0.wireOp",EDGE,"E8"),sQuery(id+"F0.wireOp",EDGE,"E9"),sQuery(id+"F0.wireOp",EDGE,"E10"),sQuery(id+"F0.wireOp",EDGE,"E11"),sQuery(id+"F0.wireOp",EDGE,"E12"),sQuery(id+"F0.wireOp",EDGE,"E13"),sQuery(id+"F0.wireOp",EDGE,"E14"),sQuery(id+"F0.wireOp",EDGE,"E15"),sQuery(id+"F0.wireOp",EDGE,"E16"),sQuery(id+"F0.wireOp",EDGE,"E17"),sQuery(id+"F0.wireOp",EDGE,"E18"),sQuery(id+"F0.wireOp",EDGE,"E19"),sQuery(id+"F0.wireOp",EDGE,"E20"),sQuery(id+"F0.wireOp",EDGE,"E21"),sQuery(id+"F0.wireOp",EDGE,"E22"),sQuery(id+"F0.wireOp",EDGE,"E23"),sQuery(id+"F0.wireOp",EDGE,"E24"),sQuery(id+"F0.wireOp",EDGE,"E25"),sQuery(id+"F0.wireOp",EDGE,"E26"),sQuery(id+"F0.wireOp",EDGE,"E27"),sQuery(id+"F0.wireOp",EDGE,"E28"),sQuery(id+"F0.wireOp",EDGE,"E29"),sQuery(id+"F0.wireOp",EDGE,"E30"),sQuery(id+"F0.wireOp",EDGE,"etuK1Xr9-J4i1-57WR-O4AE-Va2F9wOQP8k6"),sQuery(id+"F0.wireOp",EDGE,"9MBbQYz1-y2p6-nwSH-8az1-lH37U9JjGGAZ")])]}),"instanceName":"1"});
            deleteBodies(context, id + "F4", {"entities" : qUnion([Q0])});
        }
        {
            var Q0;
            Q0=makeQuery(id+"F2.opPattern","COPY",BODY,{"derivedFrom":makeQuery(id+"F1.opExtrude","SWEPT_BODY",BODY,{"disambiguationData":[OSD([sQuery(id+"F0.wireOp",EDGE,"E1.bottom"),sQuery(id+"F0.wireOp",EDGE,"E1.left"),sQuery(id+"F0.wireOp",EDGE,"E1.right"),sQuery(id+"F0.wireOp",EDGE,"E2"),sQuery(id+"F0.wireOp",EDGE,"E3.1.0.0"),sQuery(id+"F0.wireOp",EDGE,"E3.1.0.1"),sQuery(id+"F0.wireOp",EDGE,"E3.1.0.2"),sQuery(id+"F0.wireOp",EDGE,"E3.1.0.3"),sQuery(id+"F0.wireOp",EDGE,"E3.2.0.0"),sQuery(id+"F0.wireOp",EDGE,"E3.2.0.1"),sQuery(id+"F0.wireOp",EDGE,"E3.2.0.2"),sQuery(id+"F0.wireOp",EDGE,"E3.2.0.3"),sQuery(id+"F0.wireOp",EDGE,"E3.3.0.0"),sQuery(id+"F0.wireOp",EDGE,"E3.3.0.1"),sQuery(id+"F0.wireOp",EDGE,"E3.3.0.2"),sQuery(id+"F0.wireOp",EDGE,"E3.3.0.3"),sQuery(id+"F0.wireOp",EDGE,"E3.4.0.0"),sQuery(id+"F0.wireOp",EDGE,"E3.4.0.1"),sQuery(id+"F0.wireOp",EDGE,"E3.4.0.2"),sQuery(id+"F0.wireOp",EDGE,"E3.4.0.3"),sQuery(id+"F0.wireOp",EDGE,"E3.5.0.0"),sQuery(id+"F0.wireOp",EDGE,"E3.5.0.1"),sQuery(id+"F0.wireOp",EDGE,"E3.5.0.2"),sQuery(id+"F0.wireOp",EDGE,"E3.5.0.3"),sQuery(id+"F0.wireOp",EDGE,"E3.6.0.0"),sQuery(id+"F0.wireOp",EDGE,"E3.6.0.1"),sQuery(id+"F0.wireOp",EDGE,"E3.6.0.2"),sQuery(id+"F0.wireOp",EDGE,"E3.6.0.3"),sQuery(id+"F0.wireOp",EDGE,"E3.7.0.0"),sQuery(id+"F0.wireOp",EDGE,"E3.7.0.1"),sQuery(id+"F0.wireOp",EDGE,"E3.7.0.2"),sQuery(id+"F0.wireOp",EDGE,"E3.7.0.3"),sQuery(id+"F0.wireOp",EDGE,"E3.8.0.0"),sQuery(id+"F0.wireOp",EDGE,"E3.8.0.1"),sQuery(id+"F0.wireOp",EDGE,"E3.8.0.2"),sQuery(id+"F0.wireOp",EDGE,"E3.8.0.3"),sQuery(id+"F0.wireOp",EDGE,"E3.9.0.0"),sQuery(id+"F0.wireOp",EDGE,"E3.9.0.1"),sQuery(id+"F0.wireOp",EDGE,"E3.9.0.2"),sQuery(id+"F0.wireOp",EDGE,"E3.9.0.3"),sQuery(id+"F0.wireOp",EDGE,"E3.10.0.0"),sQuery(id+"F0.wireOp",EDGE,"E3.10.0.1"),sQuery(id+"F0.wireOp",EDGE,"E3.10.0.2"),sQuery(id+"F0.wireOp",EDGE,"E3.10.0.3"),sQuery(id+"F0.wireOp",EDGE,"E3.11.0.0"),sQuery(id+"F0.wireOp",EDGE,"E3.11.0.1"),sQuery(id+"F0.wireOp",EDGE,"E3.11.0.2"),sQuery(id+"F0.wireOp",EDGE,"E3.11.0.3"),sQuery(id+"F0.wireOp",EDGE,"E3.12.0.0"),sQuery(id+"F0.wireOp",EDGE,"E3.12.0.1"),sQuery(id+"F0.wireOp",EDGE,"E3.12.0.2"),sQuery(id+"F0.wireOp",EDGE,"E3.12.0.3"),sQuery(id+"F0.wireOp",EDGE,"E3.13.0.0"),sQuery(id+"F0.wireOp",EDGE,"E3.13.0.1"),sQuery(id+"F0.wireOp",EDGE,"E3.13.0.2"),sQuery(id+"F0.wireOp",EDGE,"E3.13.0.3"),sQuery(id+"F0.wireOp",EDGE,"E3.14.0.0"),sQuery(id+"F0.wireOp",EDGE,"E3.14.0.1"),sQuery(id+"F0.wireOp",EDGE,"E3.14.0.2"),sQuery(id+"F0.wireOp",EDGE,"E3.14.0.3"),sQuery(id+"F0.wireOp",EDGE,"E3.15.0.0"),sQuery(id+"F0.wireOp",EDGE,"E3.15.0.1"),sQuery(id+"F0.wireOp",EDGE,"E3.15.0.2"),sQuery(id+"F0.wireOp",EDGE,"E3.15.0.3"),sQuery(id+"F0.wireOp",EDGE,"E3.16.0.0"),sQuery(id+"F0.wireOp",EDGE,"E3.16.0.1"),sQuery(id+"F0.wireOp",EDGE,"E3.16.0.2"),sQuery(id+"F0.wireOp",EDGE,"E3.16.0.3"),sQuery(id+"F0.wireOp",EDGE,"E3.17.0.0"),sQuery(id+"F0.wireOp",EDGE,"E3.17.0.1"),sQuery(id+"F0.wireOp",EDGE,"E3.17.0.2"),sQuery(id+"F0.wireOp",EDGE,"E3.17.0.3"),sQuery(id+"F0.wireOp",EDGE,"E3.18.0.0"),sQuery(id+"F0.wireOp",EDGE,"E3.18.0.1"),sQuery(id+"F0.wireOp",EDGE,"E3.18.0.2"),sQuery(id+"F0.wireOp",EDGE,"E3.18.0.3"),sQuery(id+"F0.wireOp",EDGE,"E3.19.0.0"),sQuery(id+"F0.wireOp",EDGE,"E3.19.0.1"),sQuery(id+"F0.wireOp",EDGE,"E3.19.0.2"),sQuery(id+"F0.wireOp",EDGE,"E3.19.0.3"),sQuery(id+"F0.wireOp",EDGE,"E3.20.0.0"),sQuery(id+"F0.wireOp",EDGE,"E3.20.0.1"),sQuery(id+"F0.wireOp",EDGE,"E3.20.0.2"),sQuery(id+"F0.wireOp",EDGE,"E3.20.0.3"),sQuery(id+"F0.wireOp",EDGE,"E3.21.0.0"),sQuery(id+"F0.wireOp",EDGE,"E3.21.0.1"),sQuery(id+"F0.wireOp",EDGE,"E3.21.0.2"),sQuery(id+"F0.wireOp",EDGE,"E3.21.0.3"),sQuery(id+"F0.wireOp",EDGE,"E3.22.0.0"),sQuery(id+"F0.wireOp",EDGE,"E3.22.0.1"),sQuery(id+"F0.wireOp",EDGE,"E3.22.0.2"),sQuery(id+"F0.wireOp",EDGE,"E3.22.0.3"),sQuery(id+"F0.wireOp",EDGE,"E3.23.0.0"),sQuery(id+"F0.wireOp",EDGE,"E3.23.0.1"),sQuery(id+"F0.wireOp",EDGE,"E3.23.0.2"),sQuery(id+"F0.wireOp",EDGE,"E3.23.0.3"),sQuery(id+"F0.wireOp",EDGE,"E3.24.0.0"),sQuery(id+"F0.wireOp",EDGE,"E3.24.0.1"),sQuery(id+"F0.wireOp",EDGE,"E3.24.0.2"),sQuery(id+"F0.wireOp",EDGE,"E3.24.0.3"),sQuery(id+"F0.wireOp",EDGE,"E3.25.0.0"),sQuery(id+"F0.wireOp",EDGE,"E3.25.0.1"),sQuery(id+"F0.wireOp",EDGE,"E3.25.0.2"),sQuery(id+"F0.wireOp",EDGE,"E3.25.0.3"),sQuery(id+"F0.wireOp",EDGE,"E3.26.0.0"),sQuery(id+"F0.wireOp",EDGE,"E3.26.0.1"),sQuery(id+"F0.wireOp",EDGE,"E3.26.0.2"),sQuery(id+"F0.wireOp",EDGE,"E3.26.0.3"),sQuery(id+"F0.wireOp",EDGE,"E3.27.0.0"),sQuery(id+"F0.wireOp",EDGE,"E3.27.0.1"),sQuery(id+"F0.wireOp",EDGE,"E3.27.0.2"),sQuery(id+"F0.wireOp",EDGE,"E3.27.0.3"),sQuery(id+"F0.wireOp",EDGE,"E3.28.0.0"),sQuery(id+"F0.wireOp",EDGE,"E3.28.0.1"),sQuery(id+"F0.wireOp",EDGE,"E3.28.0.2"),sQuery(id+"F0.wireOp",EDGE,"E3.28.0.3"),sQuery(id+"F0.wireOp",EDGE,"E3.29.0.0"),sQuery(id+"F0.wireOp",EDGE,"E3.29.0.1"),sQuery(id+"F0.wireOp",EDGE,"E3.29.0.2"),sQuery(id+"F0.wireOp",EDGE,"E3.29.0.3"),sQuery(id+"F0.wireOp",EDGE,"E3.30.0.0"),sQuery(id+"F0.wireOp",EDGE,"E3.30.0.1"),sQuery(id+"F0.wireOp",EDGE,"E3.30.0.2"),sQuery(id+"F0.wireOp",EDGE,"E3.30.0.3"),sQuery(id+"F0.wireOp",EDGE,"E3.31.0.0"),sQuery(id+"F0.wireOp",EDGE,"E3.31.0.1"),sQuery(id+"F0.wireOp",EDGE,"E3.31.0.2"),sQuery(id+"F0.wireOp",EDGE,"E3.31.0.3"),sQuery(id+"F0.wireOp",EDGE,"E3.32.0.0"),sQuery(id+"F0.wireOp",EDGE,"E3.32.0.1"),sQuery(id+"F0.wireOp",EDGE,"E3.32.0.2"),sQuery(id+"F0.wireOp",EDGE,"E3.32.0.3"),sQuery(id+"F0.wireOp",EDGE,"E3.33.0.0"),sQuery(id+"F0.wireOp",EDGE,"E3.33.0.1"),sQuery(id+"F0.wireOp",EDGE,"E3.33.0.2"),sQuery(id+"F0.wireOp",EDGE,"E3.33.0.3"),sQuery(id+"F0.wireOp",EDGE,"E3.34.0.0"),sQuery(id+"F0.wireOp",EDGE,"E3.34.0.1"),sQuery(id+"F0.wireOp",EDGE,"E3.34.0.2"),sQuery(id+"F0.wireOp",EDGE,"E3.34.0.3"),sQuery(id+"F0.wireOp",EDGE,"E3.35.0.0"),sQuery(id+"F0.wireOp",EDGE,"E3.35.0.1"),sQuery(id+"F0.wireOp",EDGE,"E3.35.0.2"),sQuery(id+"F0.wireOp",EDGE,"E3.35.0.3"),sQuery(id+"F0.wireOp",EDGE,"E3.36.0.0"),sQuery(id+"F0.wireOp",EDGE,"E3.36.0.1"),sQuery(id+"F0.wireOp",EDGE,"E3.36.0.2"),sQuery(id+"F0.wireOp",EDGE,"E3.36.0.3"),sQuery(id+"F0.wireOp",EDGE,"E3.37.0.0"),sQuery(id+"F0.wireOp",EDGE,"E3.37.0.1"),sQuery(id+"F0.wireOp",EDGE,"E3.37.0.2"),sQuery(id+"F0.wireOp",EDGE,"E3.37.0.3"),sQuery(id+"F0.wireOp",EDGE,"E3.38.0.0"),sQuery(id+"F0.wireOp",EDGE,"E3.38.0.1"),sQuery(id+"F0.wireOp",EDGE,"E3.38.0.2"),sQuery(id+"F0.wireOp",EDGE,"E3.38.0.3"),sQuery(id+"F0.wireOp",EDGE,"E3.39.0.0"),sQuery(id+"F0.wireOp",EDGE,"E3.39.0.1"),sQuery(id+"F0.wireOp",EDGE,"E3.39.0.2"),sQuery(id+"F0.wireOp",EDGE,"E3.39.0.3"),sQuery(id+"F0.wireOp",EDGE,"E3.40.0.0"),sQuery(id+"F0.wireOp",EDGE,"E3.40.0.1"),sQuery(id+"F0.wireOp",EDGE,"E3.40.0.2"),sQuery(id+"F0.wireOp",EDGE,"E3.40.0.3"),sQuery(id+"F0.wireOp",EDGE,"E3.41.0.0"),sQuery(id+"F0.wireOp",EDGE,"E3.41.0.1"),sQuery(id+"F0.wireOp",EDGE,"E3.41.0.2"),sQuery(id+"F0.wireOp",EDGE,"E3.41.0.3"),sQuery(id+"F0.wireOp",EDGE,"E3.42.0.0"),sQuery(id+"F0.wireOp",EDGE,"E3.42.0.1"),sQuery(id+"F0.wireOp",EDGE,"E3.42.0.2"),sQuery(id+"F0.wireOp",EDGE,"E3.42.0.3"),sQuery(id+"F0.wireOp",EDGE,"E3.43.0.0"),sQuery(id+"F0.wireOp",EDGE,"E3.43.0.1"),sQuery(id+"F0.wireOp",EDGE,"E3.43.0.2"),sQuery(id+"F0.wireOp",EDGE,"E3.43.0.3"),sQuery(id+"F0.wireOp",EDGE,"E3.44.0.0"),sQuery(id+"F0.wireOp",EDGE,"E3.44.0.1"),sQuery(id+"F0.wireOp",EDGE,"E3.44.0.2"),sQuery(id+"F0.wireOp",EDGE,"E3.44.0.3"),sQuery(id+"F0.wireOp",EDGE,"E3.45.0.0"),sQuery(id+"F0.wireOp",EDGE,"E3.45.0.1"),sQuery(id+"F0.wireOp",EDGE,"E3.45.0.2"),sQuery(id+"F0.wireOp",EDGE,"E3.45.0.3"),sQuery(id+"F0.wireOp",EDGE,"E3.46.0.0"),sQuery(id+"F0.wireOp",EDGE,"E3.46.0.1"),sQuery(id+"F0.wireOp",EDGE,"E3.46.0.2"),sQuery(id+"F0.wireOp",EDGE,"E3.46.0.3"),sQuery(id+"F0.wireOp",EDGE,"E3.47.0.0"),sQuery(id+"F0.wireOp",EDGE,"E3.47.0.1"),sQuery(id+"F0.wireOp",EDGE,"E3.47.0.2"),sQuery(id+"F0.wireOp",EDGE,"E3.47.0.3"),sQuery(id+"F0.wireOp",EDGE,"E3.48.0.0"),sQuery(id+"F0.wireOp",EDGE,"E3.48.0.1"),sQuery(id+"F0.wireOp",EDGE,"E3.48.0.2"),sQuery(id+"F0.wireOp",EDGE,"E3.48.0.3"),sQuery(id+"F0.wireOp",EDGE,"E3.49.0.0"),sQuery(id+"F0.wireOp",EDGE,"E3.49.0.1"),sQuery(id+"F0.wireOp",EDGE,"E3.49.0.2"),sQuery(id+"F0.wireOp",EDGE,"E4.bottom"),sQuery(id+"F0.wireOp",EDGE,"E4.left"),sQuery(id+"F0.wireOp",EDGE,"E4.right"),sQuery(id+"F0.wireOp",EDGE,"E5"),sQuery(id+"F0.wireOp",EDGE,"E6.1.0.0"),sQuery(id+"F0.wireOp",EDGE,"E6.1.0.1"),sQuery(id+"F0.wireOp",EDGE,"E6.1.0.2"),sQuery(id+"F0.wireOp",EDGE,"E6.1.0.3"),sQuery(id+"F0.wireOp",EDGE,"E6.2.0.0"),sQuery(id+"F0.wireOp",EDGE,"E6.2.0.1"),sQuery(id+"F0.wireOp",EDGE,"E6.2.0.2"),sQuery(id+"F0.wireOp",EDGE,"E6.2.0.3"),sQuery(id+"F0.wireOp",EDGE,"E6.3.0.0"),sQuery(id+"F0.wireOp",EDGE,"E6.3.0.1"),sQuery(id+"F0.wireOp",EDGE,"E6.3.0.2"),sQuery(id+"F0.wireOp",EDGE,"E6.3.0.3"),sQuery(id+"F0.wireOp",EDGE,"E6.4.0.0"),sQuery(id+"F0.wireOp",EDGE,"E6.4.0.1"),sQuery(id+"F0.wireOp",EDGE,"E6.4.0.2"),sQuery(id+"F0.wireOp",EDGE,"E6.4.0.3"),sQuery(id+"F0.wireOp",EDGE,"E6.5.0.0"),sQuery(id+"F0.wireOp",EDGE,"E6.5.0.1"),sQuery(id+"F0.wireOp",EDGE,"E6.5.0.2"),sQuery(id+"F0.wireOp",EDGE,"E6.5.0.3"),sQuery(id+"F0.wireOp",EDGE,"E6.6.0.0"),sQuery(id+"F0.wireOp",EDGE,"E6.6.0.1"),sQuery(id+"F0.wireOp",EDGE,"E6.6.0.2"),sQuery(id+"F0.wireOp",EDGE,"E6.6.0.3"),sQuery(id+"F0.wireOp",EDGE,"E6.7.0.0"),sQuery(id+"F0.wireOp",EDGE,"E6.7.0.1"),sQuery(id+"F0.wireOp",EDGE,"E6.7.0.2"),sQuery(id+"F0.wireOp",EDGE,"E6.7.0.3"),sQuery(id+"F0.wireOp",EDGE,"E6.8.0.0"),sQuery(id+"F0.wireOp",EDGE,"E6.8.0.1"),sQuery(id+"F0.wireOp",EDGE,"E6.8.0.2"),sQuery(id+"F0.wireOp",EDGE,"E6.8.0.3"),sQuery(id+"F0.wireOp",EDGE,"E6.9.0.0"),sQuery(id+"F0.wireOp",EDGE,"E6.9.0.1"),sQuery(id+"F0.wireOp",EDGE,"E6.9.0.2"),sQuery(id+"F0.wireOp",EDGE,"E6.9.0.3"),sQuery(id+"F0.wireOp",EDGE,"E6.10.0.0"),sQuery(id+"F0.wireOp",EDGE,"E6.10.0.1"),sQuery(id+"F0.wireOp",EDGE,"E6.10.0.2"),sQuery(id+"F0.wireOp",EDGE,"E6.10.0.3"),sQuery(id+"F0.wireOp",EDGE,"E6.11.0.0"),sQuery(id+"F0.wireOp",EDGE,"E6.11.0.1"),sQuery(id+"F0.wireOp",EDGE,"E6.11.0.2"),sQuery(id+"F0.wireOp",EDGE,"E6.11.0.3"),sQuery(id+"F0.wireOp",EDGE,"E6.12.0.0"),sQuery(id+"F0.wireOp",EDGE,"E6.12.0.1"),sQuery(id+"F0.wireOp",EDGE,"E6.12.0.2"),sQuery(id+"F0.wireOp",EDGE,"E6.12.0.3"),sQuery(id+"F0.wireOp",EDGE,"E6.13.0.0"),sQuery(id+"F0.wireOp",EDGE,"E6.13.0.1"),sQuery(id+"F0.wireOp",EDGE,"E6.13.0.2"),sQuery(id+"F0.wireOp",EDGE,"E6.13.0.3"),sQuery(id+"F0.wireOp",EDGE,"E6.14.0.0"),sQuery(id+"F0.wireOp",EDGE,"E6.14.0.1"),sQuery(id+"F0.wireOp",EDGE,"E6.14.0.2"),sQuery(id+"F0.wireOp",EDGE,"E6.14.0.3"),sQuery(id+"F0.wireOp",EDGE,"E6.15.0.0"),sQuery(id+"F0.wireOp",EDGE,"E6.15.0.1"),sQuery(id+"F0.wireOp",EDGE,"E6.15.0.2"),sQuery(id+"F0.wireOp",EDGE,"E6.15.0.3"),sQuery(id+"F0.wireOp",EDGE,"E6.16.0.0"),sQuery(id+"F0.wireOp",EDGE,"E6.16.0.1"),sQuery(id+"F0.wireOp",EDGE,"E6.16.0.2"),sQuery(id+"F0.wireOp",EDGE,"E6.16.0.3"),sQuery(id+"F0.wireOp",EDGE,"E6.17.0.0"),sQuery(id+"F0.wireOp",EDGE,"E6.17.0.1"),sQuery(id+"F0.wireOp",EDGE,"E6.17.0.2"),sQuery(id+"F0.wireOp",EDGE,"E6.17.0.3"),sQuery(id+"F0.wireOp",EDGE,"E6.18.0.0"),sQuery(id+"F0.wireOp",EDGE,"E6.18.0.1"),sQuery(id+"F0.wireOp",EDGE,"E6.18.0.2"),sQuery(id+"F0.wireOp",EDGE,"E6.18.0.3"),sQuery(id+"F0.wireOp",EDGE,"E6.19.0.0"),sQuery(id+"F0.wireOp",EDGE,"E6.19.0.1"),sQuery(id+"F0.wireOp",EDGE,"E6.19.0.2"),sQuery(id+"F0.wireOp",EDGE,"E6.19.0.3"),sQuery(id+"F0.wireOp",EDGE,"E6.20.0.0"),sQuery(id+"F0.wireOp",EDGE,"E6.20.0.1"),sQuery(id+"F0.wireOp",EDGE,"E6.20.0.2"),sQuery(id+"F0.wireOp",EDGE,"E6.20.0.3"),sQuery(id+"F0.wireOp",EDGE,"E6.21.0.0"),sQuery(id+"F0.wireOp",EDGE,"E6.21.0.1"),sQuery(id+"F0.wireOp",EDGE,"E6.21.0.2"),sQuery(id+"F0.wireOp",EDGE,"E6.21.0.3"),sQuery(id+"F0.wireOp",EDGE,"E6.22.0.0"),sQuery(id+"F0.wireOp",EDGE,"E6.22.0.1"),sQuery(id+"F0.wireOp",EDGE,"E6.22.0.2"),sQuery(id+"F0.wireOp",EDGE,"E6.22.0.3"),sQuery(id+"F0.wireOp",EDGE,"E6.23.0.0"),sQuery(id+"F0.wireOp",EDGE,"E6.23.0.1"),sQuery(id+"F0.wireOp",EDGE,"E6.23.0.2"),sQuery(id+"F0.wireOp",EDGE,"E6.23.0.3"),sQuery(id+"F0.wireOp",EDGE,"E6.24.0.0"),sQuery(id+"F0.wireOp",EDGE,"E6.24.0.1"),sQuery(id+"F0.wireOp",EDGE,"E6.24.0.2"),sQuery(id+"F0.wireOp",EDGE,"E6.24.0.3"),sQuery(id+"F0.wireOp",EDGE,"E6.25.0.0"),sQuery(id+"F0.wireOp",EDGE,"E6.25.0.1"),sQuery(id+"F0.wireOp",EDGE,"E6.25.0.2"),sQuery(id+"F0.wireOp",EDGE,"E6.25.0.3"),sQuery(id+"F0.wireOp",EDGE,"E6.26.0.0"),sQuery(id+"F0.wireOp",EDGE,"E6.26.0.1"),sQuery(id+"F0.wireOp",EDGE,"E6.26.0.2"),sQuery(id+"F0.wireOp",EDGE,"E6.26.0.3"),sQuery(id+"F0.wireOp",EDGE,"E6.27.0.0"),sQuery(id+"F0.wireOp",EDGE,"E6.27.0.1"),sQuery(id+"F0.wireOp",EDGE,"E6.27.0.2"),sQuery(id+"F0.wireOp",EDGE,"E6.27.0.3"),sQuery(id+"F0.wireOp",EDGE,"E6.28.0.0"),sQuery(id+"F0.wireOp",EDGE,"E6.28.0.1"),sQuery(id+"F0.wireOp",EDGE,"E6.28.0.2"),sQuery(id+"F0.wireOp",EDGE,"E6.28.0.3"),sQuery(id+"F0.wireOp",EDGE,"E6.29.0.0"),sQuery(id+"F0.wireOp",EDGE,"E6.29.0.1"),sQuery(id+"F0.wireOp",EDGE,"E6.29.0.2"),sQuery(id+"F0.wireOp",EDGE,"E6.29.0.3"),sQuery(id+"F0.wireOp",EDGE,"E6.30.0.0"),sQuery(id+"F0.wireOp",EDGE,"E6.30.0.1"),sQuery(id+"F0.wireOp",EDGE,"E6.30.0.2"),sQuery(id+"F0.wireOp",EDGE,"E6.30.0.3"),sQuery(id+"F0.wireOp",EDGE,"E6.31.0.0"),sQuery(id+"F0.wireOp",EDGE,"E6.31.0.1"),sQuery(id+"F0.wireOp",EDGE,"E6.31.0.2"),sQuery(id+"F0.wireOp",EDGE,"E6.31.0.3"),sQuery(id+"F0.wireOp",EDGE,"E6.32.0.0"),sQuery(id+"F0.wireOp",EDGE,"E6.32.0.1"),sQuery(id+"F0.wireOp",EDGE,"E6.32.0.2"),sQuery(id+"F0.wireOp",EDGE,"E6.32.0.3"),sQuery(id+"F0.wireOp",EDGE,"E6.33.0.0"),sQuery(id+"F0.wireOp",EDGE,"E6.33.0.1"),sQuery(id+"F0.wireOp",EDGE,"E6.33.0.2"),sQuery(id+"F0.wireOp",EDGE,"E6.33.0.3"),sQuery(id+"F0.wireOp",EDGE,"E6.34.0.0"),sQuery(id+"F0.wireOp",EDGE,"E6.34.0.1"),sQuery(id+"F0.wireOp",EDGE,"E6.34.0.2"),sQuery(id+"F0.wireOp",EDGE,"E6.34.0.3"),sQuery(id+"F0.wireOp",EDGE,"E6.35.0.0"),sQuery(id+"F0.wireOp",EDGE,"E6.35.0.1"),sQuery(id+"F0.wireOp",EDGE,"E6.35.0.2"),sQuery(id+"F0.wireOp",EDGE,"E6.35.0.3"),sQuery(id+"F0.wireOp",EDGE,"E6.36.0.0"),sQuery(id+"F0.wireOp",EDGE,"E6.36.0.1"),sQuery(id+"F0.wireOp",EDGE,"E6.36.0.2"),sQuery(id+"F0.wireOp",EDGE,"E6.36.0.3"),sQuery(id+"F0.wireOp",EDGE,"E6.37.0.0"),sQuery(id+"F0.wireOp",EDGE,"E6.37.0.1"),sQuery(id+"F0.wireOp",EDGE,"E6.37.0.2"),sQuery(id+"F0.wireOp",EDGE,"E6.37.0.3"),sQuery(id+"F0.wireOp",EDGE,"E6.38.0.0"),sQuery(id+"F0.wireOp",EDGE,"E6.38.0.1"),sQuery(id+"F0.wireOp",EDGE,"E6.38.0.2"),sQuery(id+"F0.wireOp",EDGE,"E6.38.0.3"),sQuery(id+"F0.wireOp",EDGE,"E6.39.0.0"),sQuery(id+"F0.wireOp",EDGE,"E6.39.0.1"),sQuery(id+"F0.wireOp",EDGE,"E6.39.0.2"),sQuery(id+"F0.wireOp",EDGE,"E6.39.0.3"),sQuery(id+"F0.wireOp",EDGE,"E6.40.0.0"),sQuery(id+"F0.wireOp",EDGE,"E6.40.0.1"),sQuery(id+"F0.wireOp",EDGE,"E6.40.0.2"),sQuery(id+"F0.wireOp",EDGE,"E6.40.0.3"),sQuery(id+"F0.wireOp",EDGE,"E6.41.0.0"),sQuery(id+"F0.wireOp",EDGE,"E6.41.0.1"),sQuery(id+"F0.wireOp",EDGE,"E6.41.0.2"),sQuery(id+"F0.wireOp",EDGE,"E6.41.0.3"),sQuery(id+"F0.wireOp",EDGE,"E6.42.0.0"),sQuery(id+"F0.wireOp",EDGE,"E6.42.0.1"),sQuery(id+"F0.wireOp",EDGE,"E6.42.0.2"),sQuery(id+"F0.wireOp",EDGE,"E6.42.0.3"),sQuery(id+"F0.wireOp",EDGE,"E6.43.0.0"),sQuery(id+"F0.wireOp",EDGE,"E6.43.0.1"),sQuery(id+"F0.wireOp",EDGE,"E6.43.0.2"),sQuery(id+"F0.wireOp",EDGE,"E6.43.0.3"),sQuery(id+"F0.wireOp",EDGE,"E6.44.0.0"),sQuery(id+"F0.wireOp",EDGE,"E6.44.0.1"),sQuery(id+"F0.wireOp",EDGE,"E6.44.0.2"),sQuery(id+"F0.wireOp",EDGE,"E6.44.0.3"),sQuery(id+"F0.wireOp",EDGE,"E6.45.0.0"),sQuery(id+"F0.wireOp",EDGE,"E6.45.0.1"),sQuery(id+"F0.wireOp",EDGE,"E6.45.0.2"),sQuery(id+"F0.wireOp",EDGE,"E6.45.0.3"),sQuery(id+"F0.wireOp",EDGE,"E6.46.0.0"),sQuery(id+"F0.wireOp",EDGE,"E6.46.0.1"),sQuery(id+"F0.wireOp",EDGE,"E6.46.0.2"),sQuery(id+"F0.wireOp",EDGE,"E6.46.0.3"),sQuery(id+"F0.wireOp",EDGE,"E6.47.0.0"),sQuery(id+"F0.wireOp",EDGE,"E6.47.0.1"),sQuery(id+"F0.wireOp",EDGE,"E6.47.0.2"),sQuery(id+"F0.wireOp",EDGE,"E6.47.0.3"),sQuery(id+"F0.wireOp",EDGE,"E6.48.0.0"),sQuery(id+"F0.wireOp",EDGE,"E6.48.0.1"),sQuery(id+"F0.wireOp",EDGE,"E6.48.0.2"),sQuery(id+"F0.wireOp",EDGE,"E6.48.0.3"),sQuery(id+"F0.wireOp",EDGE,"E6.49.0.0"),sQuery(id+"F0.wireOp",EDGE,"E6.49.0.1"),sQuery(id+"F0.wireOp",EDGE,"E7"),sQuery(id+"F0.wireOp",EDGE,"E8"),sQuery(id+"F0.wireOp",EDGE,"E9"),sQuery(id+"F0.wireOp",EDGE,"E10"),sQuery(id+"F0.wireOp",EDGE,"E11"),sQuery(id+"F0.wireOp",EDGE,"E12"),sQuery(id+"F0.wireOp",EDGE,"E13"),sQuery(id+"F0.wireOp",EDGE,"E14"),sQuery(id+"F0.wireOp",EDGE,"E15"),sQuery(id+"F0.wireOp",EDGE,"E16"),sQuery(id+"F0.wireOp",EDGE,"E17"),sQuery(id+"F0.wireOp",EDGE,"E18"),sQuery(id+"F0.wireOp",EDGE,"E19"),sQuery(id+"F0.wireOp",EDGE,"E20"),sQuery(id+"F0.wireOp",EDGE,"E21"),sQuery(id+"F0.wireOp",EDGE,"E22"),sQuery(id+"F0.wireOp",EDGE,"E23"),sQuery(id+"F0.wireOp",EDGE,"E24"),sQuery(id+"F0.wireOp",EDGE,"E25"),sQuery(id+"F0.wireOp",EDGE,"E26"),sQuery(id+"F0.wireOp",EDGE,"E27"),sQuery(id+"F0.wireOp",EDGE,"E28"),sQuery(id+"F0.wireOp",EDGE,"E29"),sQuery(id+"F0.wireOp",EDGE,"E30"),sQuery(id+"F0.wireOp",EDGE,"etuK1Xr9-J4i1-57WR-O4AE-Va2F9wOQP8k6"),sQuery(id+"F0.wireOp",EDGE,"9MBbQYz1-y2p6-nwSH-8az1-lH37U9JjGGAZ")])]}),"instanceName":"1"});
            var Q1;
            Q1=makeQuery(id+"F3.opPattern","COPY",BODY,{"derivedFrom":makeQuery(id+"F2.opPattern","COPY",BODY,{"derivedFrom":makeQuery(id+"F1.opExtrude","SWEPT_BODY",BODY,{"disambiguationData":[OSD([sQuery(id+"F0.wireOp",EDGE,"E1.bottom"),sQuery(id+"F0.wireOp",EDGE,"E1.left"),sQuery(id+"F0.wireOp",EDGE,"E1.right"),sQuery(id+"F0.wireOp",EDGE,"E2"),sQuery(id+"F0.wireOp",EDGE,"E3.1.0.0"),sQuery(id+"F0.wireOp",EDGE,"E3.1.0.1"),sQuery(id+"F0.wireOp",EDGE,"E3.1.0.2"),sQuery(id+"F0.wireOp",EDGE,"E3.1.0.3"),sQuery(id+"F0.wireOp",EDGE,"E3.2.0.0"),sQuery(id+"F0.wireOp",EDGE,"E3.2.0.1"),sQuery(id+"F0.wireOp",EDGE,"E3.2.0.2"),sQuery(id+"F0.wireOp",EDGE,"E3.2.0.3"),sQuery(id+"F0.wireOp",EDGE,"E3.3.0.0"),sQuery(id+"F0.wireOp",EDGE,"E3.3.0.1"),sQuery(id+"F0.wireOp",EDGE,"E3.3.0.2"),sQuery(id+"F0.wireOp",EDGE,"E3.3.0.3"),sQuery(id+"F0.wireOp",EDGE,"E3.4.0.0"),sQuery(id+"F0.wireOp",EDGE,"E3.4.0.1"),sQuery(id+"F0.wireOp",EDGE,"E3.4.0.2"),sQuery(id+"F0.wireOp",EDGE,"E3.4.0.3"),sQuery(id+"F0.wireOp",EDGE,"E3.5.0.0"),sQuery(id+"F0.wireOp",EDGE,"E3.5.0.1"),sQuery(id+"F0.wireOp",EDGE,"E3.5.0.2"),sQuery(id+"F0.wireOp",EDGE,"E3.5.0.3"),sQuery(id+"F0.wireOp",EDGE,"E3.6.0.0"),sQuery(id+"F0.wireOp",EDGE,"E3.6.0.1"),sQuery(id+"F0.wireOp",EDGE,"E3.6.0.2"),sQuery(id+"F0.wireOp",EDGE,"E3.6.0.3"),sQuery(id+"F0.wireOp",EDGE,"E3.7.0.0"),sQuery(id+"F0.wireOp",EDGE,"E3.7.0.1"),sQuery(id+"F0.wireOp",EDGE,"E3.7.0.2"),sQuery(id+"F0.wireOp",EDGE,"E3.7.0.3"),sQuery(id+"F0.wireOp",EDGE,"E3.8.0.0"),sQuery(id+"F0.wireOp",EDGE,"E3.8.0.1"),sQuery(id+"F0.wireOp",EDGE,"E3.8.0.2"),sQuery(id+"F0.wireOp",EDGE,"E3.8.0.3"),sQuery(id+"F0.wireOp",EDGE,"E3.9.0.0"),sQuery(id+"F0.wireOp",EDGE,"E3.9.0.1"),sQuery(id+"F0.wireOp",EDGE,"E3.9.0.2"),sQuery(id+"F0.wireOp",EDGE,"E3.9.0.3"),sQuery(id+"F0.wireOp",EDGE,"E3.10.0.0"),sQuery(id+"F0.wireOp",EDGE,"E3.10.0.1"),sQuery(id+"F0.wireOp",EDGE,"E3.10.0.2"),sQuery(id+"F0.wireOp",EDGE,"E3.10.0.3"),sQuery(id+"F0.wireOp",EDGE,"E3.11.0.0"),sQuery(id+"F0.wireOp",EDGE,"E3.11.0.1"),sQuery(id+"F0.wireOp",EDGE,"E3.11.0.2"),sQuery(id+"F0.wireOp",EDGE,"E3.11.0.3"),sQuery(id+"F0.wireOp",EDGE,"E3.12.0.0"),sQuery(id+"F0.wireOp",EDGE,"E3.12.0.1"),sQuery(id+"F0.wireOp",EDGE,"E3.12.0.2"),sQuery(id+"F0.wireOp",EDGE,"E3.12.0.3"),sQuery(id+"F0.wireOp",EDGE,"E3.13.0.0"),sQuery(id+"F0.wireOp",EDGE,"E3.13.0.1"),sQuery(id+"F0.wireOp",EDGE,"E3.13.0.2"),sQuery(id+"F0.wireOp",EDGE,"E3.13.0.3"),sQuery(id+"F0.wireOp",EDGE,"E3.14.0.0"),sQuery(id+"F0.wireOp",EDGE,"E3.14.0.1"),sQuery(id+"F0.wireOp",EDGE,"E3.14.0.2"),sQuery(id+"F0.wireOp",EDGE,"E3.14.0.3"),sQuery(id+"F0.wireOp",EDGE,"E3.15.0.0"),sQuery(id+"F0.wireOp",EDGE,"E3.15.0.1"),sQuery(id+"F0.wireOp",EDGE,"E3.15.0.2"),sQuery(id+"F0.wireOp",EDGE,"E3.15.0.3"),sQuery(id+"F0.wireOp",EDGE,"E3.16.0.0"),sQuery(id+"F0.wireOp",EDGE,"E3.16.0.1"),sQuery(id+"F0.wireOp",EDGE,"E3.16.0.2"),sQuery(id+"F0.wireOp",EDGE,"E3.16.0.3"),sQuery(id+"F0.wireOp",EDGE,"E3.17.0.0"),sQuery(id+"F0.wireOp",EDGE,"E3.17.0.1"),sQuery(id+"F0.wireOp",EDGE,"E3.17.0.2"),sQuery(id+"F0.wireOp",EDGE,"E3.17.0.3"),sQuery(id+"F0.wireOp",EDGE,"E3.18.0.0"),sQuery(id+"F0.wireOp",EDGE,"E3.18.0.1"),sQuery(id+"F0.wireOp",EDGE,"E3.18.0.2"),sQuery(id+"F0.wireOp",EDGE,"E3.18.0.3"),sQuery(id+"F0.wireOp",EDGE,"E3.19.0.0"),sQuery(id+"F0.wireOp",EDGE,"E3.19.0.1"),sQuery(id+"F0.wireOp",EDGE,"E3.19.0.2"),sQuery(id+"F0.wireOp",EDGE,"E3.19.0.3"),sQuery(id+"F0.wireOp",EDGE,"E3.20.0.0"),sQuery(id+"F0.wireOp",EDGE,"E3.20.0.1"),sQuery(id+"F0.wireOp",EDGE,"E3.20.0.2"),sQuery(id+"F0.wireOp",EDGE,"E3.20.0.3"),sQuery(id+"F0.wireOp",EDGE,"E3.21.0.0"),sQuery(id+"F0.wireOp",EDGE,"E3.21.0.1"),sQuery(id+"F0.wireOp",EDGE,"E3.21.0.2"),sQuery(id+"F0.wireOp",EDGE,"E3.21.0.3"),sQuery(id+"F0.wireOp",EDGE,"E3.22.0.0"),sQuery(id+"F0.wireOp",EDGE,"E3.22.0.1"),sQuery(id+"F0.wireOp",EDGE,"E3.22.0.2"),sQuery(id+"F0.wireOp",EDGE,"E3.22.0.3"),sQuery(id+"F0.wireOp",EDGE,"E3.23.0.0"),sQuery(id+"F0.wireOp",EDGE,"E3.23.0.1"),sQuery(id+"F0.wireOp",EDGE,"E3.23.0.2"),sQuery(id+"F0.wireOp",EDGE,"E3.23.0.3"),sQuery(id+"F0.wireOp",EDGE,"E3.24.0.0"),sQuery(id+"F0.wireOp",EDGE,"E3.24.0.1"),sQuery(id+"F0.wireOp",EDGE,"E3.24.0.2"),sQuery(id+"F0.wireOp",EDGE,"E3.24.0.3"),sQuery(id+"F0.wireOp",EDGE,"E3.25.0.0"),sQuery(id+"F0.wireOp",EDGE,"E3.25.0.1"),sQuery(id+"F0.wireOp",EDGE,"E3.25.0.2"),sQuery(id+"F0.wireOp",EDGE,"E3.25.0.3"),sQuery(id+"F0.wireOp",EDGE,"E3.26.0.0"),sQuery(id+"F0.wireOp",EDGE,"E3.26.0.1"),sQuery(id+"F0.wireOp",EDGE,"E3.26.0.2"),sQuery(id+"F0.wireOp",EDGE,"E3.26.0.3"),sQuery(id+"F0.wireOp",EDGE,"E3.27.0.0"),sQuery(id+"F0.wireOp",EDGE,"E3.27.0.1"),sQuery(id+"F0.wireOp",EDGE,"E3.27.0.2"),sQuery(id+"F0.wireOp",EDGE,"E3.27.0.3"),sQuery(id+"F0.wireOp",EDGE,"E3.28.0.0"),sQuery(id+"F0.wireOp",EDGE,"E3.28.0.1"),sQuery(id+"F0.wireOp",EDGE,"E3.28.0.2"),sQuery(id+"F0.wireOp",EDGE,"E3.28.0.3"),sQuery(id+"F0.wireOp",EDGE,"E3.29.0.0"),sQuery(id+"F0.wireOp",EDGE,"E3.29.0.1"),sQuery(id+"F0.wireOp",EDGE,"E3.29.0.2"),sQuery(id+"F0.wireOp",EDGE,"E3.29.0.3"),sQuery(id+"F0.wireOp",EDGE,"E3.30.0.0"),sQuery(id+"F0.wireOp",EDGE,"E3.30.0.1"),sQuery(id+"F0.wireOp",EDGE,"E3.30.0.2"),sQuery(id+"F0.wireOp",EDGE,"E3.30.0.3"),sQuery(id+"F0.wireOp",EDGE,"E3.31.0.0"),sQuery(id+"F0.wireOp",EDGE,"E3.31.0.1"),sQuery(id+"F0.wireOp",EDGE,"E3.31.0.2"),sQuery(id+"F0.wireOp",EDGE,"E3.31.0.3"),sQuery(id+"F0.wireOp",EDGE,"E3.32.0.0"),sQuery(id+"F0.wireOp",EDGE,"E3.32.0.1"),sQuery(id+"F0.wireOp",EDGE,"E3.32.0.2"),sQuery(id+"F0.wireOp",EDGE,"E3.32.0.3"),sQuery(id+"F0.wireOp",EDGE,"E3.33.0.0"),sQuery(id+"F0.wireOp",EDGE,"E3.33.0.1"),sQuery(id+"F0.wireOp",EDGE,"E3.33.0.2"),sQuery(id+"F0.wireOp",EDGE,"E3.33.0.3"),sQuery(id+"F0.wireOp",EDGE,"E3.34.0.0"),sQuery(id+"F0.wireOp",EDGE,"E3.34.0.1"),sQuery(id+"F0.wireOp",EDGE,"E3.34.0.2"),sQuery(id+"F0.wireOp",EDGE,"E3.34.0.3"),sQuery(id+"F0.wireOp",EDGE,"E3.35.0.0"),sQuery(id+"F0.wireOp",EDGE,"E3.35.0.1"),sQuery(id+"F0.wireOp",EDGE,"E3.35.0.2"),sQuery(id+"F0.wireOp",EDGE,"E3.35.0.3"),sQuery(id+"F0.wireOp",EDGE,"E3.36.0.0"),sQuery(id+"F0.wireOp",EDGE,"E3.36.0.1"),sQuery(id+"F0.wireOp",EDGE,"E3.36.0.2"),sQuery(id+"F0.wireOp",EDGE,"E3.36.0.3"),sQuery(id+"F0.wireOp",EDGE,"E3.37.0.0"),sQuery(id+"F0.wireOp",EDGE,"E3.37.0.1"),sQuery(id+"F0.wireOp",EDGE,"E3.37.0.2"),sQuery(id+"F0.wireOp",EDGE,"E3.37.0.3"),sQuery(id+"F0.wireOp",EDGE,"E3.38.0.0"),sQuery(id+"F0.wireOp",EDGE,"E3.38.0.1"),sQuery(id+"F0.wireOp",EDGE,"E3.38.0.2"),sQuery(id+"F0.wireOp",EDGE,"E3.38.0.3"),sQuery(id+"F0.wireOp",EDGE,"E3.39.0.0"),sQuery(id+"F0.wireOp",EDGE,"E3.39.0.1"),sQuery(id+"F0.wireOp",EDGE,"E3.39.0.2"),sQuery(id+"F0.wireOp",EDGE,"E3.39.0.3"),sQuery(id+"F0.wireOp",EDGE,"E3.40.0.0"),sQuery(id+"F0.wireOp",EDGE,"E3.40.0.1"),sQuery(id+"F0.wireOp",EDGE,"E3.40.0.2"),sQuery(id+"F0.wireOp",EDGE,"E3.40.0.3"),sQuery(id+"F0.wireOp",EDGE,"E3.41.0.0"),sQuery(id+"F0.wireOp",EDGE,"E3.41.0.1"),sQuery(id+"F0.wireOp",EDGE,"E3.41.0.2"),sQuery(id+"F0.wireOp",EDGE,"E3.41.0.3"),sQuery(id+"F0.wireOp",EDGE,"E3.42.0.0"),sQuery(id+"F0.wireOp",EDGE,"E3.42.0.1"),sQuery(id+"F0.wireOp",EDGE,"E3.42.0.2"),sQuery(id+"F0.wireOp",EDGE,"E3.42.0.3"),sQuery(id+"F0.wireOp",EDGE,"E3.43.0.0"),sQuery(id+"F0.wireOp",EDGE,"E3.43.0.1"),sQuery(id+"F0.wireOp",EDGE,"E3.43.0.2"),sQuery(id+"F0.wireOp",EDGE,"E3.43.0.3"),sQuery(id+"F0.wireOp",EDGE,"E3.44.0.0"),sQuery(id+"F0.wireOp",EDGE,"E3.44.0.1"),sQuery(id+"F0.wireOp",EDGE,"E3.44.0.2"),sQuery(id+"F0.wireOp",EDGE,"E3.44.0.3"),sQuery(id+"F0.wireOp",EDGE,"E3.45.0.0"),sQuery(id+"F0.wireOp",EDGE,"E3.45.0.1"),sQuery(id+"F0.wireOp",EDGE,"E3.45.0.2"),sQuery(id+"F0.wireOp",EDGE,"E3.45.0.3"),sQuery(id+"F0.wireOp",EDGE,"E3.46.0.0"),sQuery(id+"F0.wireOp",EDGE,"E3.46.0.1"),sQuery(id+"F0.wireOp",EDGE,"E3.46.0.2"),sQuery(id+"F0.wireOp",EDGE,"E3.46.0.3"),sQuery(id+"F0.wireOp",EDGE,"E3.47.0.0"),sQuery(id+"F0.wireOp",EDGE,"E3.47.0.1"),sQuery(id+"F0.wireOp",EDGE,"E3.47.0.2"),sQuery(id+"F0.wireOp",EDGE,"E3.47.0.3"),sQuery(id+"F0.wireOp",EDGE,"E3.48.0.0"),sQuery(id+"F0.wireOp",EDGE,"E3.48.0.1"),sQuery(id+"F0.wireOp",EDGE,"E3.48.0.2"),sQuery(id+"F0.wireOp",EDGE,"E3.48.0.3"),sQuery(id+"F0.wireOp",EDGE,"E3.49.0.0"),sQuery(id+"F0.wireOp",EDGE,"E3.49.0.1"),sQuery(id+"F0.wireOp",EDGE,"E3.49.0.2"),sQuery(id+"F0.wireOp",EDGE,"E4.bottom"),sQuery(id+"F0.wireOp",EDGE,"E4.left"),sQuery(id+"F0.wireOp",EDGE,"E4.right"),sQuery(id+"F0.wireOp",EDGE,"E5"),sQuery(id+"F0.wireOp",EDGE,"E6.1.0.0"),sQuery(id+"F0.wireOp",EDGE,"E6.1.0.1"),sQuery(id+"F0.wireOp",EDGE,"E6.1.0.2"),sQuery(id+"F0.wireOp",EDGE,"E6.1.0.3"),sQuery(id+"F0.wireOp",EDGE,"E6.2.0.0"),sQuery(id+"F0.wireOp",EDGE,"E6.2.0.1"),sQuery(id+"F0.wireOp",EDGE,"E6.2.0.2"),sQuery(id+"F0.wireOp",EDGE,"E6.2.0.3"),sQuery(id+"F0.wireOp",EDGE,"E6.3.0.0"),sQuery(id+"F0.wireOp",EDGE,"E6.3.0.1"),sQuery(id+"F0.wireOp",EDGE,"E6.3.0.2"),sQuery(id+"F0.wireOp",EDGE,"E6.3.0.3"),sQuery(id+"F0.wireOp",EDGE,"E6.4.0.0"),sQuery(id+"F0.wireOp",EDGE,"E6.4.0.1"),sQuery(id+"F0.wireOp",EDGE,"E6.4.0.2"),sQuery(id+"F0.wireOp",EDGE,"E6.4.0.3"),sQuery(id+"F0.wireOp",EDGE,"E6.5.0.0"),sQuery(id+"F0.wireOp",EDGE,"E6.5.0.1"),sQuery(id+"F0.wireOp",EDGE,"E6.5.0.2"),sQuery(id+"F0.wireOp",EDGE,"E6.5.0.3"),sQuery(id+"F0.wireOp",EDGE,"E6.6.0.0"),sQuery(id+"F0.wireOp",EDGE,"E6.6.0.1"),sQuery(id+"F0.wireOp",EDGE,"E6.6.0.2"),sQuery(id+"F0.wireOp",EDGE,"E6.6.0.3"),sQuery(id+"F0.wireOp",EDGE,"E6.7.0.0"),sQuery(id+"F0.wireOp",EDGE,"E6.7.0.1"),sQuery(id+"F0.wireOp",EDGE,"E6.7.0.2"),sQuery(id+"F0.wireOp",EDGE,"E6.7.0.3"),sQuery(id+"F0.wireOp",EDGE,"E6.8.0.0"),sQuery(id+"F0.wireOp",EDGE,"E6.8.0.1"),sQuery(id+"F0.wireOp",EDGE,"E6.8.0.2"),sQuery(id+"F0.wireOp",EDGE,"E6.8.0.3"),sQuery(id+"F0.wireOp",EDGE,"E6.9.0.0"),sQuery(id+"F0.wireOp",EDGE,"E6.9.0.1"),sQuery(id+"F0.wireOp",EDGE,"E6.9.0.2"),sQuery(id+"F0.wireOp",EDGE,"E6.9.0.3"),sQuery(id+"F0.wireOp",EDGE,"E6.10.0.0"),sQuery(id+"F0.wireOp",EDGE,"E6.10.0.1"),sQuery(id+"F0.wireOp",EDGE,"E6.10.0.2"),sQuery(id+"F0.wireOp",EDGE,"E6.10.0.3"),sQuery(id+"F0.wireOp",EDGE,"E6.11.0.0"),sQuery(id+"F0.wireOp",EDGE,"E6.11.0.1"),sQuery(id+"F0.wireOp",EDGE,"E6.11.0.2"),sQuery(id+"F0.wireOp",EDGE,"E6.11.0.3"),sQuery(id+"F0.wireOp",EDGE,"E6.12.0.0"),sQuery(id+"F0.wireOp",EDGE,"E6.12.0.1"),sQuery(id+"F0.wireOp",EDGE,"E6.12.0.2"),sQuery(id+"F0.wireOp",EDGE,"E6.12.0.3"),sQuery(id+"F0.wireOp",EDGE,"E6.13.0.0"),sQuery(id+"F0.wireOp",EDGE,"E6.13.0.1"),sQuery(id+"F0.wireOp",EDGE,"E6.13.0.2"),sQuery(id+"F0.wireOp",EDGE,"E6.13.0.3"),sQuery(id+"F0.wireOp",EDGE,"E6.14.0.0"),sQuery(id+"F0.wireOp",EDGE,"E6.14.0.1"),sQuery(id+"F0.wireOp",EDGE,"E6.14.0.2"),sQuery(id+"F0.wireOp",EDGE,"E6.14.0.3"),sQuery(id+"F0.wireOp",EDGE,"E6.15.0.0"),sQuery(id+"F0.wireOp",EDGE,"E6.15.0.1"),sQuery(id+"F0.wireOp",EDGE,"E6.15.0.2"),sQuery(id+"F0.wireOp",EDGE,"E6.15.0.3"),sQuery(id+"F0.wireOp",EDGE,"E6.16.0.0"),sQuery(id+"F0.wireOp",EDGE,"E6.16.0.1"),sQuery(id+"F0.wireOp",EDGE,"E6.16.0.2"),sQuery(id+"F0.wireOp",EDGE,"E6.16.0.3"),sQuery(id+"F0.wireOp",EDGE,"E6.17.0.0"),sQuery(id+"F0.wireOp",EDGE,"E6.17.0.1"),sQuery(id+"F0.wireOp",EDGE,"E6.17.0.2"),sQuery(id+"F0.wireOp",EDGE,"E6.17.0.3"),sQuery(id+"F0.wireOp",EDGE,"E6.18.0.0"),sQuery(id+"F0.wireOp",EDGE,"E6.18.0.1"),sQuery(id+"F0.wireOp",EDGE,"E6.18.0.2"),sQuery(id+"F0.wireOp",EDGE,"E6.18.0.3"),sQuery(id+"F0.wireOp",EDGE,"E6.19.0.0"),sQuery(id+"F0.wireOp",EDGE,"E6.19.0.1"),sQuery(id+"F0.wireOp",EDGE,"E6.19.0.2"),sQuery(id+"F0.wireOp",EDGE,"E6.19.0.3"),sQuery(id+"F0.wireOp",EDGE,"E6.20.0.0"),sQuery(id+"F0.wireOp",EDGE,"E6.20.0.1"),sQuery(id+"F0.wireOp",EDGE,"E6.20.0.2"),sQuery(id+"F0.wireOp",EDGE,"E6.20.0.3"),sQuery(id+"F0.wireOp",EDGE,"E6.21.0.0"),sQuery(id+"F0.wireOp",EDGE,"E6.21.0.1"),sQuery(id+"F0.wireOp",EDGE,"E6.21.0.2"),sQuery(id+"F0.wireOp",EDGE,"E6.21.0.3"),sQuery(id+"F0.wireOp",EDGE,"E6.22.0.0"),sQuery(id+"F0.wireOp",EDGE,"E6.22.0.1"),sQuery(id+"F0.wireOp",EDGE,"E6.22.0.2"),sQuery(id+"F0.wireOp",EDGE,"E6.22.0.3"),sQuery(id+"F0.wireOp",EDGE,"E6.23.0.0"),sQuery(id+"F0.wireOp",EDGE,"E6.23.0.1"),sQuery(id+"F0.wireOp",EDGE,"E6.23.0.2"),sQuery(id+"F0.wireOp",EDGE,"E6.23.0.3"),sQuery(id+"F0.wireOp",EDGE,"E6.24.0.0"),sQuery(id+"F0.wireOp",EDGE,"E6.24.0.1"),sQuery(id+"F0.wireOp",EDGE,"E6.24.0.2"),sQuery(id+"F0.wireOp",EDGE,"E6.24.0.3"),sQuery(id+"F0.wireOp",EDGE,"E6.25.0.0"),sQuery(id+"F0.wireOp",EDGE,"E6.25.0.1"),sQuery(id+"F0.wireOp",EDGE,"E6.25.0.2"),sQuery(id+"F0.wireOp",EDGE,"E6.25.0.3"),sQuery(id+"F0.wireOp",EDGE,"E6.26.0.0"),sQuery(id+"F0.wireOp",EDGE,"E6.26.0.1"),sQuery(id+"F0.wireOp",EDGE,"E6.26.0.2"),sQuery(id+"F0.wireOp",EDGE,"E6.26.0.3"),sQuery(id+"F0.wireOp",EDGE,"E6.27.0.0"),sQuery(id+"F0.wireOp",EDGE,"E6.27.0.1"),sQuery(id+"F0.wireOp",EDGE,"E6.27.0.2"),sQuery(id+"F0.wireOp",EDGE,"E6.27.0.3"),sQuery(id+"F0.wireOp",EDGE,"E6.28.0.0"),sQuery(id+"F0.wireOp",EDGE,"E6.28.0.1"),sQuery(id+"F0.wireOp",EDGE,"E6.28.0.2"),sQuery(id+"F0.wireOp",EDGE,"E6.28.0.3"),sQuery(id+"F0.wireOp",EDGE,"E6.29.0.0"),sQuery(id+"F0.wireOp",EDGE,"E6.29.0.1"),sQuery(id+"F0.wireOp",EDGE,"E6.29.0.2"),sQuery(id+"F0.wireOp",EDGE,"E6.29.0.3"),sQuery(id+"F0.wireOp",EDGE,"E6.30.0.0"),sQuery(id+"F0.wireOp",EDGE,"E6.30.0.1"),sQuery(id+"F0.wireOp",EDGE,"E6.30.0.2"),sQuery(id+"F0.wireOp",EDGE,"E6.30.0.3"),sQuery(id+"F0.wireOp",EDGE,"E6.31.0.0"),sQuery(id+"F0.wireOp",EDGE,"E6.31.0.1"),sQuery(id+"F0.wireOp",EDGE,"E6.31.0.2"),sQuery(id+"F0.wireOp",EDGE,"E6.31.0.3"),sQuery(id+"F0.wireOp",EDGE,"E6.32.0.0"),sQuery(id+"F0.wireOp",EDGE,"E6.32.0.1"),sQuery(id+"F0.wireOp",EDGE,"E6.32.0.2"),sQuery(id+"F0.wireOp",EDGE,"E6.32.0.3"),sQuery(id+"F0.wireOp",EDGE,"E6.33.0.0"),sQuery(id+"F0.wireOp",EDGE,"E6.33.0.1"),sQuery(id+"F0.wireOp",EDGE,"E6.33.0.2"),sQuery(id+"F0.wireOp",EDGE,"E6.33.0.3"),sQuery(id+"F0.wireOp",EDGE,"E6.34.0.0"),sQuery(id+"F0.wireOp",EDGE,"E6.34.0.1"),sQuery(id+"F0.wireOp",EDGE,"E6.34.0.2"),sQuery(id+"F0.wireOp",EDGE,"E6.34.0.3"),sQuery(id+"F0.wireOp",EDGE,"E6.35.0.0"),sQuery(id+"F0.wireOp",EDGE,"E6.35.0.1"),sQuery(id+"F0.wireOp",EDGE,"E6.35.0.2"),sQuery(id+"F0.wireOp",EDGE,"E6.35.0.3"),sQuery(id+"F0.wireOp",EDGE,"E6.36.0.0"),sQuery(id+"F0.wireOp",EDGE,"E6.36.0.1"),sQuery(id+"F0.wireOp",EDGE,"E6.36.0.2"),sQuery(id+"F0.wireOp",EDGE,"E6.36.0.3"),sQuery(id+"F0.wireOp",EDGE,"E6.37.0.0"),sQuery(id+"F0.wireOp",EDGE,"E6.37.0.1"),sQuery(id+"F0.wireOp",EDGE,"E6.37.0.2"),sQuery(id+"F0.wireOp",EDGE,"E6.37.0.3"),sQuery(id+"F0.wireOp",EDGE,"E6.38.0.0"),sQuery(id+"F0.wireOp",EDGE,"E6.38.0.1"),sQuery(id+"F0.wireOp",EDGE,"E6.38.0.2"),sQuery(id+"F0.wireOp",EDGE,"E6.38.0.3"),sQuery(id+"F0.wireOp",EDGE,"E6.39.0.0"),sQuery(id+"F0.wireOp",EDGE,"E6.39.0.1"),sQuery(id+"F0.wireOp",EDGE,"E6.39.0.2"),sQuery(id+"F0.wireOp",EDGE,"E6.39.0.3"),sQuery(id+"F0.wireOp",EDGE,"E6.40.0.0"),sQuery(id+"F0.wireOp",EDGE,"E6.40.0.1"),sQuery(id+"F0.wireOp",EDGE,"E6.40.0.2"),sQuery(id+"F0.wireOp",EDGE,"E6.40.0.3"),sQuery(id+"F0.wireOp",EDGE,"E6.41.0.0"),sQuery(id+"F0.wireOp",EDGE,"E6.41.0.1"),sQuery(id+"F0.wireOp",EDGE,"E6.41.0.2"),sQuery(id+"F0.wireOp",EDGE,"E6.41.0.3"),sQuery(id+"F0.wireOp",EDGE,"E6.42.0.0"),sQuery(id+"F0.wireOp",EDGE,"E6.42.0.1"),sQuery(id+"F0.wireOp",EDGE,"E6.42.0.2"),sQuery(id+"F0.wireOp",EDGE,"E6.42.0.3"),sQuery(id+"F0.wireOp",EDGE,"E6.43.0.0"),sQuery(id+"F0.wireOp",EDGE,"E6.43.0.1"),sQuery(id+"F0.wireOp",EDGE,"E6.43.0.2"),sQuery(id+"F0.wireOp",EDGE,"E6.43.0.3"),sQuery(id+"F0.wireOp",EDGE,"E6.44.0.0"),sQuery(id+"F0.wireOp",EDGE,"E6.44.0.1"),sQuery(id+"F0.wireOp",EDGE,"E6.44.0.2"),sQuery(id+"F0.wireOp",EDGE,"E6.44.0.3"),sQuery(id+"F0.wireOp",EDGE,"E6.45.0.0"),sQuery(id+"F0.wireOp",EDGE,"E6.45.0.1"),sQuery(id+"F0.wireOp",EDGE,"E6.45.0.2"),sQuery(id+"F0.wireOp",EDGE,"E6.45.0.3"),sQuery(id+"F0.wireOp",EDGE,"E6.46.0.0"),sQuery(id+"F0.wireOp",EDGE,"E6.46.0.1"),sQuery(id+"F0.wireOp",EDGE,"E6.46.0.2"),sQuery(id+"F0.wireOp",EDGE,"E6.46.0.3"),sQuery(id+"F0.wireOp",EDGE,"E6.47.0.0"),sQuery(id+"F0.wireOp",EDGE,"E6.47.0.1"),sQuery(id+"F0.wireOp",EDGE,"E6.47.0.2"),sQuery(id+"F0.wireOp",EDGE,"E6.47.0.3"),sQuery(id+"F0.wireOp",EDGE,"E6.48.0.0"),sQuery(id+"F0.wireOp",EDGE,"E6.48.0.1"),sQuery(id+"F0.wireOp",EDGE,"E6.48.0.2"),sQuery(id+"F0.wireOp",EDGE,"E6.48.0.3"),sQuery(id+"F0.wireOp",EDGE,"E6.49.0.0"),sQuery(id+"F0.wireOp",EDGE,"E6.49.0.1"),sQuery(id+"F0.wireOp",EDGE,"E7"),sQuery(id+"F0.wireOp",EDGE,"E8"),sQuery(id+"F0.wireOp",EDGE,"E9"),sQuery(id+"F0.wireOp",EDGE,"E10"),sQuery(id+"F0.wireOp",EDGE,"E11"),sQuery(id+"F0.wireOp",EDGE,"E12"),sQuery(id+"F0.wireOp",EDGE,"E13"),sQuery(id+"F0.wireOp",EDGE,"E14"),sQuery(id+"F0.wireOp",EDGE,"E15"),sQuery(id+"F0.wireOp",EDGE,"E16"),sQuery(id+"F0.wireOp",EDGE,"E17"),sQuery(id+"F0.wireOp",EDGE,"E18"),sQuery(id+"F0.wireOp",EDGE,"E19"),sQuery(id+"F0.wireOp",EDGE,"E20"),sQuery(id+"F0.wireOp",EDGE,"E21"),sQuery(id+"F0.wireOp",EDGE,"E22"),sQuery(id+"F0.wireOp",EDGE,"E23"),sQuery(id+"F0.wireOp",EDGE,"E24"),sQuery(id+"F0.wireOp",EDGE,"E25"),sQuery(id+"F0.wireOp",EDGE,"E26"),sQuery(id+"F0.wireOp",EDGE,"E27"),sQuery(id+"F0.wireOp",EDGE,"E28"),sQuery(id+"F0.wireOp",EDGE,"E29"),sQuery(id+"F0.wireOp",EDGE,"E30"),sQuery(id+"F0.wireOp",EDGE,"etuK1Xr9-J4i1-57WR-O4AE-Va2F9wOQP8k6"),sQuery(id+"F0.wireOp",EDGE,"9MBbQYz1-y2p6-nwSH-8az1-lH37U9JjGGAZ")])]}),"instanceName":"1"}),"instanceName":"1"});
            deleteBodies(context, id + "F5", {"entities" : qUnion([Q0, Q1])});
        }
        {
            var Q0;
            Q0=makeQuery(id+"F0.imprint","IMPRINT",FACE,{"disambiguationData":[TD([[makeQuery(id+"F0.imprint","IMPRINT",EDGE,{"derivedFrom":sQuery(id+"F0.wireOp",EDGE,"E4.bottom")}),-1.0]])]});
            extrude(context, id + "F6", {"entities" : qUnion([Q0]), "depth" : 5.08 * mm});
        }
    });
